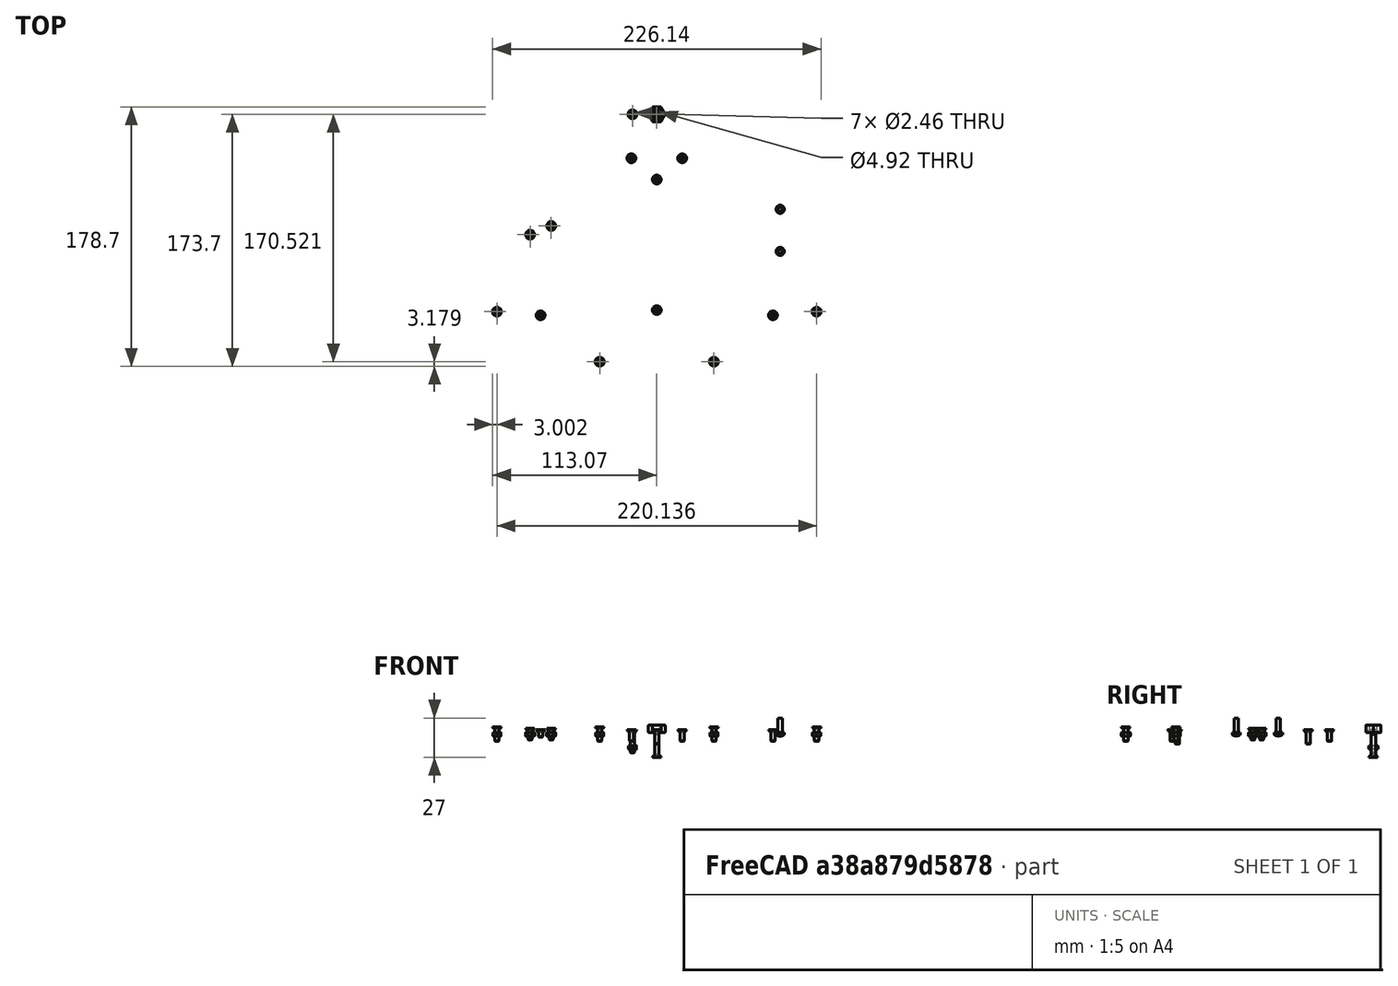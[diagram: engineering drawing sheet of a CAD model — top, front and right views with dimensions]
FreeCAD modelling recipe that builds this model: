
FCSTD DOCUMENT  (FreeCAD 1.0RUnknown)
Label: Sextant
License: All rights reserved
LicenseURL: https://en.wikipedia.org/wiki/All_rights_reserved
objects: Part::FeaturePython×24, App::Link×18, App::DocumentObjectGroup×10, PartDesign::CoordinateSystem×1, App::FeaturePython×1, App::Part×1
note: 25 computed .brp shape members not serialized (recipe doc carries the construction recipe); baked Part::Feature solids carry a one-line shape summary decoded from their .brp
EXTERNAL_REF file=Frame.FCStd obj=Local_CS003
EXTERNAL_REF file=Scale.FCStd obj=LCS_Origin002
EXTERNAL_REF file=Scale.FCStd obj=Part002
EXTERNAL_REF file=Frame.FCStd obj=Local_CS
EXTERNAL_REF file=HorizonMirror.FCStd obj=LCS_Origin
EXTERNAL_REF file=HorizonMirror.FCStd obj=Assembly
EXTERNAL_REF file=Frame.FCStd obj=Local_CS001
EXTERNAL_REF file=Viewscope.FCStd obj=LCS_Origin
EXTERNAL_REF file=Viewscope.FCStd obj=Assembly
EXTERNAL_REF file=Frame.FCStd obj=HoleAxis_1
EXTERNAL_REF file=Frame.FCStd obj=HoleAxis_2
EXTERNAL_REF file=HorizonMirror.FCStd obj=LCS_Screw1
EXTERNAL_REF file=HorizonMirror.FCStd obj=LCS_Screw2
EXTERNAL_REF file=Frame.FCStd obj=Local_CS002
EXTERNAL_REF file=Parts.FCStd obj=LCS_Top
EXTERNAL_REF file=Parts.FCStd obj=bEARING
EXTERNAL_REF file=Resources.FCStd obj=Spreadsheet
EXTERNAL_REF file=Scale.FCStd obj=LCS_Screw1
EXTERNAL_REF file=Scale.FCStd obj=LCS_Screw3
EXTERNAL_REF file=Frame.FCStd obj=LCS_Origin
EXTERNAL_REF file=Frame.FCStd obj=Body
EXTERNAL_REF file=IndexArm.FCStd obj=LCS_1
EXTERNAL_REF file=IndexArm.FCStd obj=Assembly
EXTERNAL_REF file=Parts.FCStd obj=LCS_Origin001
EXTERNAL_REF file=Parts.FCStd obj=BearingCover
EXTERNAL_REF file=Frame.FCStd obj=Local_CS004
EXTERNAL_REF file=Parts.FCStd obj=LCS_Bottom
EXTERNAL_REF file=Parts.FCStd obj=LCS_ClampTop
EXTERNAL_REF file=Parts.FCStd obj=BearingClamp
EXTERNAL_REF file=Parts.FCStd obj=LCS_Origin002
EXTERNAL_REF file=Frame.FCStd obj=LCS_Handle
EXTERNAL_REF file=Handle.FCStd obj=Local_CS
EXTERNAL_REF file=Handle.FCStd obj=Body002
EXTERNAL_REF file=Shadeset.FCStd obj=DatumPlane004
EXTERNAL_REF file=Shadeset.FCStd obj=LCS_Origin
EXTERNAL_REF file=Shadeset.FCStd obj=Assembly
EXTERNAL_REF file=Frame.FCStd obj=Local_CS005
EXTERNAL_REF file=Shadeset.FCStd obj=Local_CS004
EXTERNAL_REF file=Shadeset.FCStd obj=Body001
EXTERNAL_REF file=Shadeset.FCStd obj=DatumPlane003
EXTERNAL_REF file=Frame.FCStd obj=Local_CS006
EXTERNAL_REF file=Shadeset.FCStd obj=Local_CS005
EXTERNAL_REF file=Shadeset.FCStd obj=OffsetBlockHorizonShade
EXTERNAL_REF file=Frame.FCStd obj=DatumLine
EXTERNAL_REF file=Parts.FCStd obj=LCS_Bottom001
EXTERNAL_REF file=Parts.FCStd obj=Standoff
EXTERNAL_REF file=Frame.FCStd obj=DatumLine003
EXTERNAL_REF file=Frame.FCStd obj=DatumLine001
EXTERNAL_REF file=Frame.FCStd obj=DatumLine002
EXTERNAL_REF file=Parts.FCStd obj=LCS_Origin003
EXTERNAL_REF file=Frame.FCStd obj=DatumLine004
EXTERNAL_REF file=Frame.FCStd obj=DatumLine005
EXTERNAL_REF file=Scale.FCStd obj=LCS_Screw004
EXTERNAL_REF file=Scale.FCStd obj=LCS_Screw2

FEATURE [App::DocumentObjectGroup] Parts
FEATURE [PartDesign::CoordinateSystem] LCS_Origin
  AttacherType = Attacher::AttachEngine3D
  AttachmentSupport = -> [X_Axis]
  MapMode = 2
FEATURE [App::DocumentObjectGroup] Constraints
FEATURE [App::FeaturePython] Variables  # WARN: FeaturePython — macro-defined, semantics opaque (R4)
  Type = App::PropertyContainer
  angle = 60
FEATURE [App::DocumentObjectGroup] Configurations
FEATURE [App::Link] Scale
  AttachedBy = #LCS_Origin002
  AttachedTo = Frame#Local_CS003
  LinkPlacement = pos=(0,0,2) rot=(0,0,1;0rad)
  LinkedObject = -> <external Scale.FCStd>#Part002
  Placement = pos=(0,0,2) rot=(0,0,1;0rad)
  SolverId = Asm4EE
  expr: Placement = Frame.Placement * Frame#Local_CS003.Placement * AttachmentOffset * Scale#LCS_Origin002.Placement ^ -1
FEATURE [App::Link] HorizonMirror
  AttachedBy = #LCS_Origin
  AttachedTo = Frame#Local_CS
  AttachmentOffset = pos=(0,0,0) rot=(0,0,1;4.71239rad)
  LinkPlacement = pos=(-80,-80,2) rot=(0,0,-1;5.89049rad)
  LinkedObject = -> <external HorizonMirror.FCStd>#Assembly
  Placement = pos=(-80,-80,2) rot=(0,0,-1;5.89049rad)
  SolverId = Asm4EE
  expr: Placement = Frame.Placement * Frame#Local_CS.Placement * AttachmentOffset * HorizonMirror#LCS_Origin.Placement ^ -1
FEATURE [App::Link] Viewscope
  AttachedBy = #LCS_Origin
  AttachedTo = Frame#Local_CS001
  LinkPlacement = pos=(85,-80,2) rot=(0,0,1;0rad)
  LinkedObject = -> <external Viewscope.FCStd>#Assembly
  Placement = pos=(85,-80,2) rot=(0,0,1;0rad)
  SolverId = Asm4EE
  expr: Placement = Frame.Placement * Frame#Local_CS001.Placement * AttachmentOffset * Viewscope#LCS_Origin.Placement ^ -1
FEATURE [Part::FeaturePython] Screw  label="M3x10-Screw"  # WARN: FeaturePython — macro-defined, semantics opaque (R4)
  AttachedBy = Origin
  AttachedTo = Frame#HoleAxis_1
  Diameter = 3
  Invert = false
  LeftHanded = false
  Length = 1
  LengthCustom = 10
  MatchOuter = false
  OffsetAngle = 0
  Placement = pos=(0,-45,2) rot=(0,0,1;0rad)
  SolverId = Asm4EE
  Thread = false
  Type = 50
  expr: Placement = Frame.Placement * Frame#HoleAxis_1.Placement * AttachmentOffset
FEATURE [Part::FeaturePython] Screw001  label="M3x10-Screw080"  # WARN: FeaturePython — macro-defined, semantics opaque (R4)
  AttachedBy = Origin
  AttachedTo = Frame#HoleAxis_2
  Diameter = 3
  Invert = false
  LeftHanded = false
  Length = 1
  LengthCustom = 10
  MatchOuter = false
  OffsetAngle = 0
  Placement = pos=(0,-135,2) rot=(0,0,1;0rad)
  SolverId = Asm4EE
  Thread = false
  Type = 50
  expr: Placement = Frame.Placement * Frame#HoleAxis_2.Placement * AttachmentOffset
FEATURE [Part::FeaturePython] Screw002  label="M3x8-Screw"  # WARN: FeaturePython — macro-defined, semantics opaque (R4)
  AttachedBy = Origin
  AttachedTo = HorizonMirror#LCS_Screw1
  Diameter = 3
  Invert = false
  LeftHanded = false
  Length = 0
  LengthCustom = 8
  MatchOuter = false
  OffsetAngle = 0
  Placement = pos=(-87.2617,-83.0079,3) rot=(0,0,-1;4.31969rad)
  SolverId = Asm4EE
  Thread = false
  Type = 50
  expr: Placement = HorizonMirror.Placement * HorizonMirror#LCS_Screw1.Placement * AttachmentOffset
FEATURE [Part::FeaturePython] Screw003  label="M3x8-Screw388"  # WARN: FeaturePython — macro-defined, semantics opaque (R4)
  AttachedBy = Origin
  AttachedTo = HorizonMirror#LCS_Screw2
  Diameter = 3
  Invert = false
  LeftHanded = false
  Length = 0
  LengthCustom = 8
  MatchOuter = false
  OffsetAngle = 0
  Placement = pos=(-72.7383,-76.9921,3) rot=(0,0,-1;4.31969rad)
  SolverId = Asm4EE
  Thread = false
  Type = 50
  expr: Placement = HorizonMirror.Placement * HorizonMirror#LCS_Screw2.Placement * AttachmentOffset
FEATURE [Part::FeaturePython] Nut001  label="M3-Nut658"  # WARN: FeaturePython — macro-defined, semantics opaque (R4)
  AttachedBy = Origin
  AttachedTo = HorizonMirror#LCS_Screw2
  AttachmentOffset = pos=(0,0,-3) rot=(1,0,0;3.14159rad)
  Diameter = 4
  Invert = false
  LeftHanded = false
  MatchOuter = false
  OffsetAngle = 0
  Placement = pos=(-72.7383,-76.9921,0) rot=(-0.55557,-0.83147,0;3.14159rad)
  SolverId = Asm4EE
  Thread = false
  Type = 31
  expr: .AttachmentOffset.Base.z = -<<Dimensions>>.horizon_mirror_base_thickness - <<Dimensions>>.frame_thickness
  expr: Placement = HorizonMirror.Placement * HorizonMirror#LCS_Screw2.Placement * AttachmentOffset
FEATURE [Part::FeaturePython] Nut002  label="M3-Nut657"  # WARN: FeaturePython — macro-defined, semantics opaque (R4)
  AttachedBy = Origin
  AttachedTo = HorizonMirror#LCS_Screw1
  AttachmentOffset = pos=(0,0,-3) rot=(0,-1,0;3.14159rad)
  Diameter = 4
  Invert = false
  LeftHanded = false
  MatchOuter = false
  OffsetAngle = 0
  Placement = pos=(-87.2617,-83.0079,0) rot=(-0.83147,0.55557,0;3.14159rad)
  SolverId = Asm4EE
  Thread = false
  Type = 31
  expr: .AttachmentOffset.Base.z = -<<Dimensions>>.horizon_mirror_base_thickness - <<Dimensions>>.frame_thickness
  expr: Placement = HorizonMirror.Placement * HorizonMirror#LCS_Screw1.Placement * AttachmentOffset
FEATURE [App::Link] Bearing001
  AttachedBy = #LCS_Top
  AttachedTo = Frame#Local_CS002
  LinkPlacement = pos=(0,0,-3.5) rot=(0,0,1;0rad)
  LinkedObject = -> <external Parts.FCStd>#bEARING
  Placement = pos=(0,0,-3.5) rot=(0,0,1;0rad)
  SolverId = Asm4EE
  expr: Placement = Frame.Placement * Frame#Local_CS002.Placement * AttachmentOffset * Parts#LCS_Top.Placement ^ -1
FEATURE [App::Link] Link  label="Dimensions"
  LinkedObject = -> <external Resources.FCStd>#Spreadsheet
FEATURE [Part::FeaturePython] Screw004  label="M3x10-Screw078"  # WARN: FeaturePython — macro-defined, semantics opaque (R4)
  AttachedBy = Origin
  AttachedTo = Scale#LCS_Screw1
  Diameter = 3
  Invert = false
  LeftHanded = false
  Length = 1
  LengthCustom = 10
  MatchOuter = false
  OffsetAngle = 0
  Placement = pos=(-110.068,-136.052,4) rot=(0,0,1;1.5708rad)
  SolverId = Asm4EE
  Thread = false
  Type = 50
  expr: Placement = Scale.Placement * Scale#LCS_Screw1.Placement * AttachmentOffset
FEATURE [Part::FeaturePython] Screw005  label="M3x10-Screw079"  # WARN: FeaturePython — macro-defined, semantics opaque (R4)
  AttachedBy = Origin
  AttachedTo = Scale#LCS_Screw3
  Diameter = 3
  Invert = false
  LeftHanded = false
  Length = 1
  LengthCustom = 10
  MatchOuter = false
  OffsetAngle = 0
  Placement = pos=(-39.34,-170.521,4) rot=(0,0,1;1.5708rad)
  SolverId = Asm4EE
  Thread = false
  Type = 50
  expr: Placement = Scale.Placement * Scale#LCS_Screw3.Placement * AttachmentOffset
FEATURE [Part::FeaturePython] Nut  label="M3-Nut"  # WARN: FeaturePython — macro-defined, semantics opaque (R4)
  AttachedBy = Origin
  AttachedTo = Scale#LCS_Screw1
  AttachmentOffset = pos=(0,0,-4) rot=(0,1,0;3.14159rad)
  Diameter = 4
  Invert = false
  LeftHanded = false
  MatchOuter = false
  OffsetAngle = 0
  Placement = pos=(-110.068,-136.052,0) rot=(-0.707107,0.707107,0;3.14159rad)
  SolverId = Asm4EE
  Thread = false
  Type = 31
  expr: .AttachmentOffset.Base.z = -<<Dimensions>>.scale_thickness - <<Dimensions>>.frame_thickness
  expr: Placement = Scale.Placement * Scale#LCS_Screw1.Placement * AttachmentOffset
FEATURE [Part::FeaturePython] Nut003  label="M3-Nut656"  # WARN: FeaturePython — macro-defined, semantics opaque (R4)
  AttachedBy = Origin
  AttachedTo = Scale#LCS_Screw3
  AttachmentOffset = pos=(0,0,-4) rot=(0,1,0;3.14159rad)
  Diameter = 4
  Invert = false
  LeftHanded = false
  MatchOuter = false
  OffsetAngle = 0
  Placement = pos=(-39.34,-170.521,0) rot=(-0.707107,0.707107,0;3.14159rad)
  SolverId = Asm4EE
  Thread = false
  Type = 31
  expr: .AttachmentOffset.Base.z = -<<Dimensions>>.scale_thickness - <<Dimensions>>.frame_thickness
  expr: Placement = Scale.Placement * Scale#LCS_Screw3.Placement * AttachmentOffset
FEATURE [App::Link] Frame
  AttachedBy = #LCS_Origin
  AttachedTo = Parent Assembly#LCS_Origin
  LinkedObject = -> <external Frame.FCStd>#Body
  SolverId = Asm4EE
  expr: Placement = LCS_Origin.Placement * AttachmentOffset * Frame#LCS_Origin.Placement ^ -1
FEATURE [App::Link] IndexArm
  AttachedBy = #LCS_1
  AttachedTo = Frame#LCS_Origin
  AttachmentOffset = pos=(0,0,0) rot=(0,0,1;-1.0472rad)
  LinkPlacement = pos=(0,0,4) rot=(0,0,1;5.75959rad)
  LinkedObject = -> <external IndexArm.FCStd>#Assembly
  Placement = pos=(0,0,4) rot=(0,0,1;5.75959rad)
  SolverId = Asm4EE
  expr: .AttachmentOffset.Rotation.Angle = -Variables.angle
  expr: Placement = Frame.Placement * Frame#LCS_Origin.Placement * AttachmentOffset * IndexArm#LCS_1.Placement ^ -1
FEATURE [App::Link] BearingCover
  AttachedBy = #LCS_Origin001
  AttachedTo = Frame#Local_CS002
  LinkedObject = -> <external Parts.FCStd>#BearingCover
  SolverId = Asm4EE
  expr: Placement = Frame.Placement * Frame#Local_CS002.Placement * AttachmentOffset * Parts#LCS_Origin001.Placement ^ -1
FEATURE [Part::FeaturePython] Screw008  label="M3x16-Screw"  # WARN: FeaturePython — macro-defined, semantics opaque (R4)
  AttachedBy = Origin
  AttachedTo = Frame#Local_CS004
  Diameter = 3
  Invert = false
  LeftHanded = false
  Length = 3
  LengthCustom = 16
  MatchOuter = false
  OffsetAngle = 0
  Placement = pos=(-16.75,0,2) rot=(0,0,1;1.5708rad)
  SolverId = Asm4EE
  Thread = false
  Type = 50
  expr: Placement = Frame.Placement * Frame#Local_CS004.Placement * AttachmentOffset
FEATURE [Part::FeaturePython] Nut006  label="M3-Nut655"  # WARN: FeaturePython — macro-defined, semantics opaque (R4)
  AttachedBy = Origin
  AttachedTo = Frame#Local_CS004
  AttachmentOffset = pos=(0,0,-11) rot=(0,1,0;3.14159rad)
  Diameter = 4
  Invert = false
  LeftHanded = false
  MatchOuter = false
  OffsetAngle = 0
  Placement = pos=(-16.75,0,-9) rot=(-0.707107,0.707107,0;3.14159rad)
  SolverId = Asm4EE
  Thread = false
  Type = 31
  expr: Placement = Frame.Placement * Frame#Local_CS004.Placement * AttachmentOffset
FEATURE [App::Link] BearingClamp
  AttachedBy = #LCS_ClampTop
  AttachedTo = Bearing001#LCS_Bottom
  LinkPlacement = pos=(0,0,-17) rot=(0,0,1;0rad)
  LinkedObject = -> <external Parts.FCStd>#BearingClamp
  Placement = pos=(0,0,-17) rot=(0,0,1;0rad)
  SolverId = Asm4EE
  expr: Placement = Bearing001.Placement * Parts#LCS_Bottom.Placement * AttachmentOffset * Parts#LCS_ClampTop.Placement ^ -1
FEATURE [Part::FeaturePython] Screw009  label="M3x16-Screw001"  # WARN: FeaturePython — macro-defined, semantics opaque (R4)
  AttachedBy = Origin
  AttachedTo = BearingClamp#LCS_Origin002
  AttachmentOffset = pos=(0,0,0) rot=(0,1,0;3.14159rad)
  Diameter = 3
  Invert = false
  LeftHanded = false
  Length = 3
  LengthCustom = 16
  MatchOuter = false
  OffsetAngle = 0
  Placement = pos=(0,0,-17) rot=(0,1,0;3.14159rad)
  SolverId = Asm4EE
  Thread = false
  Type = 50
  expr: Placement = BearingClamp.Placement * Parts#LCS_Origin002.Placement * AttachmentOffset
FEATURE [App::Link] Handle
  AttachedBy = #Local_CS
  AttachedTo = Frame#LCS_Handle
  AttachmentOffset = pos=(0,0,0) rot=(1,0,0;4.71239rad)
  LinkPlacement = pos=(7.1e-15,-90,-2e-16) rot=(1,0,0;4.71239rad)
  LinkedObject = -> <external Handle.FCStd>#Body002
  Placement = pos=(7.1e-15,-90,-2e-16) rot=(1,0,0;4.71239rad)
  SolverId = Asm4EE
  expr: Placement = Frame.Placement * Frame#LCS_Handle.Placement * AttachmentOffset * Handle#Local_CS.Placement ^ -1
FEATURE [App::Link] Shadeset
  AttachedBy = #LCS_Origin
  AttachedTo = OffsetBlockHorizonShade#DatumPlane004
  AttachmentOffset = pos=(0,0,0) rot=(0,0,-1;3.14159rad)
  LinkPlacement = pos=(-105,-101.182,12) rot=(0,0,1;0rad)
  LinkedObject = -> <external Shadeset.FCStd>#Assembly
  Placement = pos=(-105,-101.182,12) rot=(0,0,1;0rad)
  SolverId = Asm4EE
  expr: Placement = OffsetBlockHorizonShade.Placement * Shadeset#DatumPlane004.Placement * AttachmentOffset * Shadeset#LCS_Origin.Placement ^ -1
FEATURE [App::Link] OffsetBlockIndexShade
  AttachedBy = #Local_CS004
  AttachedTo = Frame#Local_CS005
  LinkPlacement = pos=(-64.4754,-34.5196,2) rot=(0,0,1;0.785398rad)
  LinkedObject = -> <external Shadeset.FCStd>#Body001
  Placement = pos=(-64.4754,-34.5196,2) rot=(0,0,1;0.785398rad)
  SolverId = Asm4EE
  expr: Placement = Frame.Placement * Frame#Local_CS005.Placement * AttachmentOffset * Shadeset#Local_CS004.Placement ^ -1
FEATURE [App::Link] Shadeset001
  AttachedBy = #LCS_Origin
  AttachedTo = OffsetBlockIndexShade#DatumPlane003
  AttachmentOffset = pos=(0,0,0) rot=(0,0,1;3.14159rad)
  LinkPlacement = pos=(-64.4754,-34.5196,3) rot=(0,0,1;3.92699rad)
  LinkedObject = -> <external Shadeset.FCStd>#Assembly
  Placement = pos=(-64.4754,-34.5196,3) rot=(0,0,1;3.92699rad)
  SolverId = Asm4EE
  expr: Placement = OffsetBlockIndexShade.Placement * Shadeset#DatumPlane003.Placement * AttachmentOffset * Shadeset#LCS_Origin.Placement ^ -1
FEATURE [App::Link] OffsetBlockHorizonShade
  AttachedBy = #Local_CS005
  AttachedTo = Frame#Local_CS006
  AttachmentOffset = pos=(0,0,0) rot=(0,0,-1;3.14159rad)
  LinkPlacement = pos=(-105,-101.182,2) rot=(0,0,-1;3.14159rad)
  LinkedObject = -> <external Shadeset.FCStd>#OffsetBlockHorizonShade
  Placement = pos=(-105,-101.182,2) rot=(0,0,-1;3.14159rad)
  SolverId = Asm4EE
  expr: Placement = Frame.Placement * Frame#Local_CS006.Placement * AttachmentOffset * Shadeset#Local_CS005.Placement ^ -1
FEATURE [Part::FeaturePython] Screw010  label="M3x5-Screw"  # WARN: FeaturePython — macro-defined, semantics opaque (R4)
  AttachedBy = Origin
  AttachedTo = Frame#DatumLine
  Diameter = 3
  Invert = false
  LeftHanded = false
  Length = 7
  LengthCustom = 5
  MatchOuter = false
  OffsetAngle = 0
  Placement = pos=(-80,-138.564,2) rot=(0,0,1;0rad)
  SolverId = Asm4EE
  Thread = false
  Type = 50
  expr: Placement = Frame.Placement * Frame#DatumLine.Placement * AttachmentOffset
FEATURE [App::Link] Standoff
  AttachedBy = #LCS_Bottom001
  AttachedTo = Frame#DatumLine
  AttachmentOffset = pos=(0,0,-2) rot=(0,1,0;3.14159rad)
  LinkPlacement = pos=(-80,-138.564,0) rot=(0,1,0;3.14159rad)
  LinkedObject = -> <external Parts.FCStd>#Standoff
  Placement = pos=(-80,-138.564,0) rot=(0,1,0;3.14159rad)
  SolverId = Asm4EE
  expr: .AttachmentOffset.Base.z = -<<Dimensions>>.frame_thickness
  expr: Placement = Frame.Placement * Frame#DatumLine.Placement * AttachmentOffset * Parts#LCS_Bottom001.Placement ^ -1
FEATURE [Part::FeaturePython] Screw011  label="M3x8-Screw389"  # WARN: FeaturePython — macro-defined, semantics opaque (R4)
  AttachedBy = Origin
  AttachedTo = Frame#DatumLine003
  Diameter = 3
  Invert = false
  LeftHanded = false
  Length = 0
  LengthCustom = 8
  MatchOuter = false
  OffsetAngle = 0
  Placement = pos=(80,-138.564,2) rot=(0,0,1;0rad)
  SolverId = Asm4EE
  Thread = false
  Type = 50
  expr: Placement = Frame.Placement * Frame#DatumLine003.Placement * AttachmentOffset
FEATURE [Part::FeaturePython] Screw012  label="M3x8-Screw391"  # WARN: FeaturePython — macro-defined, semantics opaque (R4)
  AttachedBy = Origin
  AttachedTo = Frame#DatumLine001
  Diameter = 3
  Invert = false
  LeftHanded = false
  Length = 0
  LengthCustom = 8
  MatchOuter = false
  OffsetAngle = 0
  Placement = pos=(17.5,-30.3109,2) rot=(0,0,1;0rad)
  SolverId = Asm4EE
  Thread = false
  Type = 50
  expr: Placement = Frame.Placement * Frame#DatumLine001.Placement * AttachmentOffset
FEATURE [Part::FeaturePython] Screw013  label="M3x8-Screw390"  # WARN: FeaturePython — macro-defined, semantics opaque (R4)
  AttachedBy = Origin
  AttachedTo = Frame#DatumLine002
  Diameter = 3
  Invert = false
  LeftHanded = false
  Length = 0
  LengthCustom = 8
  MatchOuter = false
  OffsetAngle = 0
  Placement = pos=(-17.5,-30.3109,2) rot=(0,0,1;0rad)
  SolverId = Asm4EE
  Thread = false
  Type = 50
  expr: Placement = Frame.Placement * Frame#DatumLine002.Placement * AttachmentOffset
FEATURE [App::Link] Standoff001
  AttachedBy = #LCS_Origin003
  AttachedTo = Frame#DatumLine003
  AttachmentOffset = pos=(0,0,-2) rot=(0,1,0;3.14159rad)
  LinkPlacement = pos=(80,-138.564,0) rot=(0,1,0;3.14159rad)
  LinkedObject = -> <external Parts.FCStd>#Standoff
  Placement = pos=(80,-138.564,0) rot=(0,1,0;3.14159rad)
  SolverId = Asm4EE
  expr: .AttachmentOffset.Base.z = -<<Dimensions>>.frame_thickness
  expr: Placement = Frame.Placement * Frame#DatumLine003.Placement * AttachmentOffset * Parts#LCS_Origin003.Placement ^ -1
FEATURE [App::Link] Standoff_1  label="Standoff002"
  AttachedBy = #LCS_Bottom001
  AttachedTo = Frame#DatumLine001
  AttachmentOffset = pos=(0,0,-2) rot=(0,1,0;3.14159rad)
  LinkPlacement = pos=(17.5,-30.3109,0) rot=(0,1,0;3.14159rad)
  LinkedObject = -> <external Parts.FCStd>#Standoff
  Placement = pos=(17.5,-30.3109,0) rot=(0,1,0;3.14159rad)
  SolverId = Asm4EE
  expr: .AttachmentOffset.Base.z = -<<Dimensions>>.frame_thickness
  expr: Placement = Frame.Placement * Frame#DatumLine001.Placement * AttachmentOffset * Parts#LCS_Bottom001.Placement ^ -1
FEATURE [App::Link] Standoff_2  label="Standoff003"
  AttachedBy = #LCS_Bottom001
  AttachedTo = Frame#DatumLine002
  AttachmentOffset = pos=(0,0,-2) rot=(0,1,0;3.14159rad)
  LinkPlacement = pos=(-17.5,-30.3109,0) rot=(0,1,0;3.14159rad)
  LinkedObject = -> <external Parts.FCStd>#Standoff
  Placement = pos=(-17.5,-30.3109,0) rot=(0,1,0;3.14159rad)
  SolverId = Asm4EE
  expr: .AttachmentOffset.Base.z = -<<Dimensions>>.frame_thickness
  expr: Placement = Frame.Placement * Frame#DatumLine002.Placement * AttachmentOffset * Parts#LCS_Bottom001.Placement ^ -1
FEATURE [App::DocumentObjectGroup] IndexArm001
  Group = -> [IndexArm,BearingClamp,BearingCover,Bearing001,Screw009,Screw008,Nut006]
FEATURE [App::DocumentObjectGroup] Shades
  Group = -> [OffsetBlockIndexShade,OffsetBlockHorizonShade,Shadeset,Shadeset001]
FEATURE [App::DocumentObjectGroup] HorizonMirror001
  Group = -> [HorizonMirror,Screw003,Nut001,Screw002,Nut002]
FEATURE [App::DocumentObjectGroup] Standoff002  label="Standoffs"
  Group = -> [Standoff001,Standoff_1,Standoff_2,Standoff,Screw011,Screw013,Screw012,Screw010]
FEATURE [Part::FeaturePython] Screw014  label="M3x10-Screw081"  # WARN: FeaturePython — macro-defined, semantics opaque (R4)
  AttachedBy = Origin
  AttachedTo = Frame#DatumLine004
  AttachmentOffset = pos=(0,0,0) rot=(0,1,0;3.14159rad)
  Diameter = 4
  Invert = false
  LeftHanded = false
  Length = 4
  LengthCustom = 10
  MatchOuter = false
  OffsetAngle = 0
  Placement = pos=(85,-65.5,0) rot=(0,1,0;3.14159rad)
  SolverId = Asm4EE
  Thread = false
  Type = 76
  expr: Diameter = <<Dimensions>>.viewscope_screw_type
  expr: Placement = Frame.Placement * Frame#DatumLine004.Placement * AttachmentOffset
FEATURE [Part::FeaturePython] Screw015  label="M3x10-Screw082"  # WARN: FeaturePython — macro-defined, semantics opaque (R4)
  AttachedBy = Origin
  AttachedTo = Frame#DatumLine005
  AttachmentOffset = pos=(0,0,0) rot=(0,1,0;3.14159rad)
  Diameter = 4
  Invert = false
  LeftHanded = false
  Length = 4
  LengthCustom = 10
  MatchOuter = false
  OffsetAngle = 0
  Placement = pos=(85,-94.5,0) rot=(0,1,0;3.14159rad)
  SolverId = Asm4EE
  Thread = false
  Type = 76
  expr: Diameter = <<Dimensions>>.viewscope_screw_type
  expr: Placement = Frame.Placement * Frame#DatumLine005.Placement * AttachmentOffset
FEATURE [App::DocumentObjectGroup] ViewScope
  Group = -> [Viewscope,Screw014,Screw015]
FEATURE [Part::FeaturePython] Screw016  label="M3x10-Screw083"  # WARN: FeaturePython — macro-defined, semantics opaque (R4)
  AttachedBy = Origin
  AttachedTo = Scale#LCS_Screw004
  Diameter = 3
  Invert = false
  LeftHanded = false
  Length = 1
  LengthCustom = 10
  MatchOuter = false
  OffsetAngle = 0
  Placement = pos=(39.34,-170.521,4) rot=(0,0,1;1.5708rad)
  SolverId = Asm4EE
  Thread = false
  Type = 50
  expr: Placement = Scale.Placement * Scale#LCS_Screw004.Placement * AttachmentOffset
FEATURE [Part::FeaturePython] Screw017  label="M3x10-Screw084"  # WARN: FeaturePython — macro-defined, semantics opaque (R4)
  AttachedBy = Origin
  AttachedTo = Scale#LCS_Screw2
  Diameter = 3
  Invert = false
  LeftHanded = false
  Length = 1
  LengthCustom = 10
  MatchOuter = false
  OffsetAngle = 0
  Placement = pos=(110.068,-136.052,4) rot=(0,0,1;1.5708rad)
  SolverId = Asm4EE
  Thread = false
  Type = 50
  expr: Placement = Scale.Placement * Scale#LCS_Screw2.Placement * AttachmentOffset
FEATURE [Part::FeaturePython] Nut007  label="M3-Nut659"  # WARN: FeaturePython — macro-defined, semantics opaque (R4)
  AttachedBy = Origin
  AttachedTo = Scale#LCS_Screw004
  AttachmentOffset = pos=(0,0,-4) rot=(0,1,0;3.14159rad)
  Diameter = 4
  Invert = false
  LeftHanded = false
  MatchOuter = false
  OffsetAngle = 0
  Placement = pos=(39.34,-170.521,0) rot=(-0.707107,0.707107,0;3.14159rad)
  SolverId = Asm4EE
  Thread = false
  Type = 31
  expr: .AttachmentOffset.Base.z = -<<Dimensions>>.scale_thickness - <<Dimensions>>.frame_thickness
  expr: Placement = Scale.Placement * Scale#LCS_Screw004.Placement * AttachmentOffset
FEATURE [Part::FeaturePython] Nut008  label="M6-Nut"  # WARN: FeaturePython — macro-defined, semantics opaque (R4)
  Diameter = 8
  Invert = false
  LeftHanded = false
  MatchOuter = false
  OffsetAngle = 0
  Thread = false
  Type = 31
FEATURE [App::DocumentObjectGroup] Handle001
  Group = -> [Handle,Screw,Screw001,Nut008]
FEATURE [Part::FeaturePython] Nut009  label="M3-Nut660"  # WARN: FeaturePython — macro-defined, semantics opaque (R4)
  AttachedBy = Origin
  AttachedTo = Scale#LCS_Screw2
  AttachmentOffset = pos=(0,0,-4) rot=(0,1,0;3.14159rad)
  Diameter = 4
  Invert = false
  LeftHanded = false
  MatchOuter = false
  OffsetAngle = 0
  Placement = pos=(110.068,-136.052,0) rot=(-0.707107,0.707107,0;3.14159rad)
  SolverId = Asm4EE
  Thread = false
  Type = 31
  expr: .AttachmentOffset.Base.z = -<<Dimensions>>.scale_thickness - <<Dimensions>>.frame_thickness
  expr: Placement = Scale.Placement * Scale#LCS_Screw2.Placement * AttachmentOffset
FEATURE [App::DocumentObjectGroup] Scale001
  Group = -> [Scale,Nut,Nut003,Screw004,Screw005,Screw016,Screw017,Nut007,Nut009]
FEATURE [App::Part] Assembly
  AssemblyType = Part::Link
  Group = -> [LCS_Origin,Constraints,Variables,Configurations,Frame,Screw008,Nut006,Screw004,Screw005,Nut,Nut003,Screw,Screw001,Screw002,Nut002,Screw009,ViewScope,Screw003,Standoff,Screw010,Nut001,Screw011,Screw013,Screw012,Standoff001,Standoff_1,Standoff_2,IndexArm001,IndexArm,Viewscope,Shades,BearingClamp,BearingCover,Bearing001,OffsetBlockIndexShade,OffsetBlockHorizonShade,Shadeset,Shadeset001,Handle001,+13 more]
  Origin = -> Origin
  Type = Assembly

RESOLVED EXTERNAL PARTS (link-assembly join: the EXTERNAL_REF files above that resolve inside this repo's crawl, each included once):
---- part Frame.FCStd = doc fcstd_3e981a858956 ----
FCSTD DOCUMENT  (FreeCAD 1.0RUnknown)
Label: Frame
License: All rights reserved
LicenseURL: http://en.wikipedia.org/wiki/All_rights_reserved
objects: Sketcher::SketchObject×16, PartDesign::CoordinateSystem×9, PartDesign::Line×8, PartDesign::Pad×8, PartDesign::Hole×8, PartDesign::Plane×2, App::Link×1, PartDesign::SubShapeBinder×1, TechDraw::DrawSVGTemplate×1, PartDesign::Mirrored×1, PartDesign::Pocket×1, PartDesign::PolarPattern×1, PartDesign::Draft×1, PartDesign::Body×1, TechDraw::DrawViewPart×1, TechDraw::DrawPage×1
note: 111 computed .brp shape members not serialized (recipe doc carries the construction recipe); baked Part::Feature solids carry a one-line shape summary decoded from their .brp
EXTERNAL_REF file=Resources.FCStd obj=Spreadsheet
EXTERNAL_REF file=Scale.FCStd obj=Part002
EXTERNAL_REF file=HorizonMirror.FCStd obj=Sketch
EXTERNAL_REF file=Viewscope.FCStd obj=Sketch004
EXTERNAL_REF file=Shade.FCStd obj=Sketch010

FEATURE [App::Link] Link  label="Dimensions"
  LinkedObject = -> <external Resources.FCStd>#Spreadsheet
FEATURE [Sketcher::SketchObject] Sketch006
  ArcFitTolerance = 0
  AttachmentOffset = pos=(0,0,2) rot=(0,0,1;0rad)
  AttachmentSupport = -> [XY_Plane]
  FullyConstrained = true
  MakeInternals = false
  MapMode = 5
  Placement = pos=(0,0,2) rot=(0,0,1;0rad)
  expr: .AttachmentOffset.Base.z = <<Dimensions>>.frame_thickness
  expr: Constraints[3] = <<Dimensions>>.handle_connector_screw_diameter
  expr: Constraints[4] = <<Dimensions>>.handle_length - <<Dimensions>>.handle_outer_width
  expr: Constraints[6] = <<Dimensions>>.scale_outer_radius / 2
  sketch-geometry (3):
    g0: Circle CenterX=0 CenterY=-45 CenterZ=0 NormalX=0 NormalY=0 NormalZ=1 AngleXU=0 Radius=1.5
    g1: Circle CenterX=0 CenterY=-135 CenterZ=0 NormalX=0 NormalY=0 NormalZ=1 AngleXU=0 Radius=1.5
    g2: GeomPoint [constr] X=0 Y=-90 Z=0
  constraints (7):
    c: PointOnObject(g0,g-2)
    c: PointOnObject(g1,g-2)
    c: Equal(g1,g0)
    c: Diameter(g0) = 3
    c: Distance(g0,g1) = 90
    c: Symmetric(g0,g1,g2)
    c: DistanceY(g2,g-1) = 90
FEATURE [PartDesign::SubShapeBinder] Binder
  BindCopyOnChange = 0
  BindMode = 0
  ClaimChildren = false
  Context = -> Body [Hole.Binder.]
  Fuse = false
  MakeFace = true
  OffsetFill = false
  OffsetIntersection = false
  OffsetJoinType = 0
  OffsetOpenResult = false
  PartialLoad = false
  Placement = pos=(0,0,-4) rot=(0,0,1;0rad)
  Relative = true
  Support = -> [<external Scale.FCStd>#Part002[Body003.Sketch.]]
  _Version = 2
FEATURE [Sketcher::SketchObject] Sketch003
  ArcFitTolerance = 0
  AttachmentSupport = -> [XY_Plane]
  FullyConstrained = true
  MakeInternals = false
  MapMode = 5
  expr: Constraints[10] = <<Dimensions>>.view_center_offset_vert
  expr: Constraints[4] = <<Dimensions>>.viewscope_screw_diameter
  expr: Constraints[5] = <<Viewscope>>#Sketch004.Constraints.hole_distance
  sketch-geometry (6):
    g0: LineSegment [constr] StartX=85 StartY=-65.5 StartZ=0 EndX=85 EndY=-94.5 EndZ=0
    g1: Circle CenterX=85 CenterY=-65.5 CenterZ=0 NormalX=0 NormalY=0 NormalZ=1 AngleXU=0 Radius=1.5
    g2: Circle CenterX=85 CenterY=-94.5 CenterZ=0 NormalX=0 NormalY=0 NormalZ=1 AngleXU=0 Radius=1.5
    g3: GeomPoint [constr] X=85 Y=-80 Z=0
    g4: LineSegment [constr] StartX=85 StartY=-80 StartZ=0 EndX=0 EndY=-80 EndZ=0
    g5: GeomPoint [constr] X=0 Y=-80 Z=0
  constraints (14):
    c: Coincident(g1,g0)
    c: Coincident(g0,g2)
    c: Vertical(g0)
    c: Equal(g2,g1)
    c: Diameter(g1) = 3
    c: Distance(g0) = 29
    c: Symmetric(g1,g2,g3)
    c: Coincident(g4,g3)
    c: PointOnObject(g4,g-2)
    c: Horizontal(g4)
    c: DistanceY(g4,g-1) = 80
    c: PointOnObject(g5,g4)
    c: DistanceX(g5,g3) = 85
    c: PointOnObject(g5,g-2)
FEATURE [Sketcher::SketchObject] Sketch004
  ArcFitTolerance = 0
  AttachmentSupport = -> [XY_Plane]
  ExternalGeometry = -> [Sketch003]
  FullyConstrained = true
  MakeInternals = false
  MapMode = 5
  expr: Constraints[7] = <<Dimensions>>.viewscope_collar_thickness / 2
  expr: Constraints[8] = <<Dimensions>>.viewscope_collar_width / 2
  expr: Constraints[9] = <<Dimensions>>.viewscope_collar_width / 2
  sketch-geometry (6):
    g0: LineSegment StartX=35.7957 StartY=-62 StartZ=0 EndX=88.75 EndY=-62 EndZ=0
    g1: LineSegment StartX=88.75 StartY=-62 StartZ=0 EndX=88.75 EndY=-98 EndZ=0
    g2: LineSegment StartX=88.75 StartY=-98 StartZ=0 EndX=56.5803 EndY=-98 EndZ=0
    g3: LineSegment StartX=35.7957 StartY=-62 StartZ=0 EndX=56.5803 EndY=-98 EndZ=0
    g4: LineSegment [constr] StartX=0 StartY=0 StartZ=0 EndX=-35.7957 EndY=-62 EndZ=0
    g5: LineSegment [constr] StartX=0 StartY=0 StartZ=0 EndX=35.7957 EndY=-62 EndZ=0
  constraints (16):
    c: Horizontal(g0)
    c: Vertical(g1)
    c: Horizontal(g2)
    c: Coincident(g3,g0)
    c: Coincident(g3,g2)
    c: Coincident(g0,g1)
    c: Coincident(g2,g1)
    c: DistanceX(g-3,g0) = 3.75
    c: DistanceY(g-3,g0) = 3.5
    c: DistanceY(g1,g-4) = 3.5
    c: Coincident(g4,g-1)
    c: Coincident(g5,g4)
    c: Coincident(g0,g5)
    c: Parallel(g5,g3)
    c: Symmetric(g4,g0,g-2)
    c: Angle(g4,g5) = 1.0472
FEATURE [Sketcher::SketchObject] Sketch007
  ArcFitTolerance = 0
  AttachmentSupport = -> [XY_Plane]
  FullyConstrained = true
  MakeInternals = false
  MapMode = 5
  expr: Constraints[1] = <<Dimensions>>.bearing_Da
  sketch-geometry (1):
    g0: Circle CenterX=0 CenterY=0 CenterZ=0 NormalX=0 NormalY=0 NormalZ=1 AngleXU=0 Radius=10
  constraints (2):
    c: Coincident(g0,g-1)
    c: Diameter(g0) = 20
FEATURE [PartDesign::CoordinateSystem] LCS_Origin
  AttacherType = Attacher::AttachEngine3D
  AttachmentSupport = -> [X_Axis]
  MapMode = 2
FEATURE [PartDesign::CoordinateSystem] LCS_Handle
  AttacherType = Attacher::AttachEngine3D
  AttachmentOffset = pos=(0,0,-2) rot=(0,0,1;0rad)
  AttachmentSupport = -> [Sketch006]
  MapMode = 45
  Placement = pos=(7.1e-15,-90,-2e-16) rot=(0,0,1;0rad)
  expr: .AttachmentOffset.Base.z = -<<Dimensions>>.frame_thickness
FEATURE [PartDesign::Line] HoleAxis_1  label="HandleScrew1"
  AttacherType = Attacher::AttachEngineLine
  AttachmentSupport = -> [Sketch006]
  Length = 4.2272
  MapMode = 19
  Placement = pos=(0,-45,2) rot=(0,0,1;0rad)
  ResizeMode = 1
FEATURE [PartDesign::Line] HoleAxis_2  label="HandleScrew2"
  AttacherType = Attacher::AttachEngineLine
  AttachmentSupport = -> [Sketch006]
  Length = 4.2272
  MapMode = 19
  Placement = pos=(0,-135,2) rot=(0,0,1;0rad)
  ResizeMode = 1
FEATURE [PartDesign::CoordinateSystem] Local_CS001  label="LCS_Viewscope"
  AttacherType = Attacher::AttachEngine3D
  AttachmentOffset = pos=(0,0,2) rot=(0,0,1;0rad)
  AttachmentSupport = -> [Sketch003]
  MapMode = 45
  Placement = pos=(85,-80,2) rot=(0,0,1;0rad)
  expr: .AttachmentOffset.Base.z = <<Dimensions>>.frame_thickness
FEATURE [PartDesign::CoordinateSystem] Local_CS002  label="LCS_ShaftBot"
  AttacherType = Attacher::AttachEngine3D
  AttachmentOffset = pos=(0,0,0) rot=(0,0,-1;1.5708rad)
  AttachmentSupport = -> [Sketch007]
  MapMode = 11
FEATURE [PartDesign::CoordinateSystem] Local_CS003  label="LCS_Scale"
  AttacherType = Attacher::AttachEngine3D
  AttachmentOffset = pos=(0,0,2) rot=(0,0,1;0rad)
  AttachmentSupport = -> [X_Axis]
  MapMode = 2
  Placement = pos=(0,0,2) rot=(0,0,1;0rad)
  expr: .AttachmentOffset.Base.z = <<Dimensions>>.frame_thickness
FEATURE [TechDraw::DrawSVGTemplate] Template
  Height = 210
  Orientation = 1
  Template = /app/share/Mod/TechDraw/Templates/A4_Landscape_blank.svg
  Width = 297
FEATURE [PartDesign::Plane] DatumPlane  label="Plane_Bottom"
  AttachmentSupport = -> [XY_Plane]
  Length = 67.9716
  MapMode = 5
  ResizeMode = 0
  Width = 179.461
FEATURE [Sketcher::SketchObject] Sketch
  ArcFitTolerance = 0
  AttachmentSupport = -> [DatumPlane]
  ExternalGeometry = -> [Sketch006]
  FullyConstrained = true
  MakeInternals = false
  MapMode = 2
  expr: Constraints[11] = <<Dimensions>>.scale_width
  expr: Constraints[25] = <<Dimensions>>.frame_width
  expr: Constraints[26] = max(<<Dimensions>>.frame_width; <<Dimensions>>.handle_outer_width) / 2
  expr: Constraints[3] = <<Dimensions>>.scale_outer_radius
  expr: Constraints[4] = (<<Dimensions>>.scale_angle + 2 * <<Dimensions>>.scale_extra_angle) / 2
  expr: Constraints[5] = <<Dimensions>>.bearing_housing_diameter / 2
  sketch-geometry (11):
    g0: ArcOfCircle CenterX=0 CenterY=0 CenterZ=0 NormalX=0 NormalY=0 NormalZ=1 AngleXU=0 Radius=22.5 StartAngle=1.5708 EndAngle=3.84895
    g1: LineSegment StartX=-17.1018 StartY=-14.6212 StartZ=0 EndX=-91.4124 EndY=-143.331 EndZ=0
    g2: LineSegment StartX=-78.422 StartY=-150.831 StartZ=0 EndX=-7.5 EndY=-27.9904 EndZ=0
    g3: ArcOfCircle CenterX=0 CenterY=0 CenterZ=0 NormalX=0 NormalY=0 NormalZ=1 AngleXU=0 Radius=170 StartAngle=4.23292 EndAngle=4.66826
    g4: ArcOfCircle CenterX=0 CenterY=0 CenterZ=0 NormalX=0 NormalY=0 NormalZ=1 AngleXU=0 Radius=180 StartAngle=3.97062 EndAngle=4.71239
    g5: LineSegment StartX=-121.606 StartY=-132.71 StartZ=0 EndX=-114.85 EndY=-125.337 EndZ=0
    g6: ArcOfCircle CenterX=0 CenterY=0 CenterZ=0 NormalX=0 NormalY=0 NormalZ=1 AngleXU=0 Radius=170 StartAngle=3.97062 EndAngle=4.14466
    g7: LineSegment StartX=1.4e-15 StartY=22.5 StartZ=0 EndX=0 EndY=-180 EndZ=0
    g8: LineSegment StartX=-7.5 StartY=-27.9904 StartZ=0 EndX=-7.5 EndY=-169.834 EndZ=0
    g9: ArcOfCircle [constr] CenterX=0 CenterY=0 CenterZ=0 NormalX=0 NormalY=0 NormalZ=1 AngleXU=0 Radius=170 StartAngle=4.14466 EndAngle=4.23292
    g10: LineSegment [constr] StartX=0 StartY=0 StartZ=0 EndX=-84.9172 EndY=-147.081 EndZ=0
  constraints (32):
    c: Coincident(g3,g0)
    c: Coincident(g3,g2)
    c: Coincident(g0,g1)
    c: Radius(g4) = 180
    c: Angle(g4) = 0.741765
    c: Radius(g0) = 22.5
    c: PointOnObject(g4,g-1)
    c: Coincident(g5,g4)
    c: Coincident(g6,g5)
    c: Coincident(g6,g1)
    c: Perpendicular(g4,g5)
    c: Distance(g5) = 10
    c: Coincident(g6,g0)
    c: Parallel(g1,g2)
    c: PointOnObject(g4,g-2)
    c: Coincident(g7,g4)
    c: PointOnObject(g4,g-2)
    c: PointOnObject(g0,g-2)
    c: Coincident(g0,g4)
    c: Vertical(g8)
    c: Coincident(g2,g8)
    c: Coincident(g8,g3)
    c: Coincident(g0,g7)
    c: Coincident(g9,g1)
    c: Coincident(g9,g2)
    c: Distance(g1,g2) = 15
    c: DistanceX(g2,g0) = 7.5
    c: Coincident(g10,g0)
    c: Angle(g10,g7) = 0.523599
    c: Symmetric(g1,g2,g10)
    c: Parallel(g10,g1)
    c: Coincident(g9,g0)
FEATURE [Sketcher::SketchObject] Sketch002
  ArcFitTolerance = 0
  AttachmentSupport = -> [XY_Plane]
  ExternalGeometry = -> [Sketch]
  FullyConstrained = true
  MakeInternals = false
  MapMode = 5
  expr: Constraints[12] = <<Dimensions>>.view_center_offset_vert
  expr: Constraints[17] = HorizonMirror#Sketch.Constraints.hole_distance
  expr: Constraints[18] = <<Dimensions>>.horizon_mirror_offset
  expr: Constraints[9] = <<Dimensions>>.horizon_mirror_screw_diameter
  sketch-geometry (7):
    g0: LineSegment [constr] StartX=0 StartY=-80 StartZ=0 EndX=-80 EndY=-80 EndZ=0
    g1: LineSegment [constr] StartX=-87.2617 StartY=-83.0079 StartZ=0 EndX=-72.7383 EndY=-76.9921 EndZ=0
    g2: LineSegment [constr] StartX=-72.7383 StartY=-76.9921 StartZ=0 EndX=-72.7383 EndY=-80 EndZ=0
    g3: Circle CenterX=-87.2617 CenterY=-83.0079 CenterZ=0 NormalX=0 NormalY=0 NormalZ=1 AngleXU=0 Radius=1.5
    g4: Circle CenterX=-72.7383 CenterY=-76.9921 CenterZ=0 NormalX=0 NormalY=0 NormalZ=1 AngleXU=0 Radius=1.5
    g5: LineSegment [constr] StartX=-80 StartY=-80 StartZ=0 EndX=0 EndY=0 EndZ=0
    g6: LineSegment [constr] StartX=-72.7383 StartY=-76.9921 StartZ=0 EndX=-74.8652 EndY=-74.8652 EndZ=0
  constraints (19):
    c: PointOnObject(g0,g-2)
    c: Horizontal(g0)
    c: Symmetric(g1,g1,g0)
    c: Coincident(g2,g1)
    c: PointOnObject(g2,g0)
    c: Perpendicular(g2,g0)
    c: Coincident(g3,g1)
    c: Coincident(g4,g1)
    c: Equal(g4,g3)
    c: Diameter(g3) = 3
    c: Coincident(g5,g0)
    c: Coincident(g5,g-1)
    c: DistanceY(g0,g5) = 80
    c: Coincident(g6,g4)
    c: PointOnObject(g6,g5)
    c: Perpendicular(g6,g5)
    c: Equal(g6,g2)
    c: Distance(g1) = 15.72
    c: DistanceX(g0,g0) = 80
FEATURE [PartDesign::CoordinateSystem] Local_CS  label="LCS_HorizonMirror"
  AttacherType = Attacher::AttachEngine3D
  AttachmentOffset = pos=(0,0,2) rot=(0,0,1;0rad)
  AttachmentSupport = -> [Sketch002]
  MapMode = 45
  Placement = pos=(-80,-80,2) rot=(0,0,1;1.96349rad)
  expr: .AttachmentOffset.Base.z = <<Dimensions>>.frame_thickness
FEATURE [PartDesign::Plane] DatumPlane001  label="Plane_Top"
  AttachmentOffset = pos=(0,0,2) rot=(0,0,1;0rad)
  AttachmentSupport = -> [DatumPlane]
  Length = 67.9716
  MapMode = 5
  Placement = pos=(0,0,2) rot=(0,0,1;0rad)
  ResizeMode = 0
  Width = 179.461
  expr: .AttachmentOffset.Base.z = <<Dimensions>>.frame_thickness
FEATURE [PartDesign::Pad] Pad
  Direction = (0,0,1)
  Length = 2
  Length2 = 10
  Profile = -> Sketch
  ReferenceAxis = -> Sketch [N_Axis]
  Suppressed = false
  Type = 3
  UpToFace = -> DatumPlane001
  expr: Length = <<Dimensions>>.frame_thickness
FEATURE [Sketcher::SketchObject] Sketch008
  ArcFitTolerance = 0
  AttachmentSupport = -> [DatumPlane001]
  FullyConstrained = true
  MakeInternals = false
  MapMode = 5
  Placement = pos=(0,0,2) rot=(0,0,1;0rad)
  expr: Constraints[1] = <<Dimensions>>.bearing_D / 4 + <<Dimensions>>.bearing_housing_diameter / 4
  expr: Constraints[2] = <<Dimensions>>.bearing_housing_screw_diameter
  sketch-geometry (1):
    g0: Circle CenterX=-16.75 CenterY=0 CenterZ=0 NormalX=0 NormalY=0 NormalZ=1 AngleXU=0 Radius=1.5
  constraints (3):
    c: PointOnObject(g0,g-1)
    c: DistanceX(g0,g-1) = 16.75
    c: Diameter(g0) = 3
FEATURE [PartDesign::CoordinateSystem] Local_CS004  label="LCS_BearingHousingScrew"
  AttacherType = Attacher::AttachEngine3D
  AttachmentSupport = -> [Sketch008]
  MapMode = 11
  Placement = pos=(-16.75,0,2) rot=(0,0,1;1.5708rad)
FEATURE [Sketcher::SketchObject] Sketch009
  ArcFitTolerance = 0
  AttachmentSupport = -> [DatumPlane]
  FullyConstrained = true
  MakeInternals = false
  MapMode = 5
  expr: Constraints[23] = <<Dimensions>>.frame_width
  sketch-geometry (11):
    g0: ArcOfCircle CenterX=0 CenterY=0 CenterZ=0 NormalX=0 NormalY=0 NormalZ=1 AngleXU=0 Radius=150 StartAngle=4.18879 EndAngle=5.23599
    g1: ArcOfCircle CenterX=0 CenterY=0 CenterZ=0 NormalX=0 NormalY=0 NormalZ=1 AngleXU=0 Radius=135 StartAngle=4.18879 EndAngle=5.23599
    g2: ArcOfCircle CenterX=0 CenterY=0 CenterZ=0 NormalX=0 NormalY=0 NormalZ=1 AngleXU=0 Radius=80 StartAngle=4.18879 EndAngle=5.23599
    g3: ArcOfCircle CenterX=0 CenterY=0 CenterZ=0 NormalX=0 NormalY=0 NormalZ=1 AngleXU=0 Radius=95 StartAngle=4.18879 EndAngle=5.23599
    g4: LineSegment [constr] StartX=0 StartY=0 StartZ=0 EndX=-75 EndY=-129.904 EndZ=0
    g5: LineSegment [constr] StartX=0 StartY=0 StartZ=0 EndX=75 EndY=-129.904 EndZ=0
    g6: LineSegment StartX=-75 StartY=-129.904 StartZ=0 EndX=-67.5 EndY=-116.913 EndZ=0
    g7: LineSegment StartX=-47.5 StartY=-82.2724 StartZ=0 EndX=-40 EndY=-69.282 EndZ=0
    g8: LineSegment StartX=40 StartY=-69.282 StartZ=0 EndX=47.5 EndY=-82.2724 EndZ=0
    g9: LineSegment StartX=67.5 StartY=-116.913 StartZ=0 EndX=75 EndY=-129.904 EndZ=0
    g10: GeomPoint [constr] X=0 Y=-129.904 Z=0
  constraints (29):
    c: Coincident(g0,g-1)
    c: Coincident(g1,g0)
    c: Coincident(g2,g0)
    c: Coincident(g3,g0)
    c: Coincident(g4,g0)
    c: Coincident(g4,g0)
    c: PointOnObject(g1,g4)
    c: PointOnObject(g3,g4)
    c: PointOnObject(g2,g4)
    c: Coincident(g5,g0)
    c: Coincident(g5,g0)
    c: PointOnObject(g3,g5)
    c: PointOnObject(g2,g5)
    c: PointOnObject(g1,g5)
    c: Coincident(g6,g0)
    c: Coincident(g6,g1)
    c: Coincident(g7,g3)
    c: Coincident(g7,g2)
    c: Coincident(g8,g2)
    c: Coincident(g8,g3)
    c: Coincident(g9,g1)
    c: Coincident(g9,g0)
    c: Equal(g9,g8)
    c: Distance(g9) = 15
    c: Distance(g2,g0) = 80
    c: PointOnObject(g10,g-2)
    c: Symmetric(g0,g0,g10)
    c: Distance(g3,g1) = 40
    c: Angle(g4,g5) = 1.0472
FEATURE [Sketcher::SketchObject] Sketch010  label="Sketch_IndexShade"
  ArcFitTolerance = 0
  AttachmentSupport = -> [DatumPlane001]
  ExternalGeometry = -> [Sketch002]
  FullyConstrained = true
  MakeInternals = false
  MapMode = 5
  Placement = pos=(0,0,2) rot=(0,0,1;0rad)
  expr: Constraints[3] = 90 ° + 2 * <<Dimensions>>.horizon_mirror_angle
  expr: Constraints[9] = Shade#Sketch010.Constraints.total_width / 2
  sketch-geometry (6):
    g0: Circle CenterX=-71.5465 CenterY=-27.4485 CenterZ=0 NormalX=0 NormalY=0 NormalZ=1 AngleXU=0 Radius=1.5
    g1: Circle CenterX=-57.4043 CenterY=-41.5906 CenterZ=0 NormalX=0 NormalY=0 NormalZ=1 AngleXU=0 Radius=1.5
    g2: LineSegment [constr] StartX=-71.5465 StartY=-27.4485 StartZ=0 EndX=-57.4043 EndY=-41.5906 EndZ=0
    g3: LineSegment [constr] StartX=0 StartY=0 StartZ=0 EndX=-49.4975 EndY=-49.4975 EndZ=0
    g4: GeomPoint [constr] X=-64.4754 Y=-34.5196 Z=0
    g5: LineSegment [constr] StartX=-64.4754 StartY=-34.5196 StartZ=0 EndX=-49.4975 EndY=-49.4975 EndZ=0
  constraints (14):
    c: Coincident(g2,g0)
    c: Coincident(g2,g1)
    c: Coincident(g3,g-1)
    c: Angle(g-2,g3) = 2.35619
    c: Symmetric(g0,g1,g4)
    c: Distance(g0,g1) = 20
    c: Coincident(g5,g4)
    c: Coincident(g5,g3)
    c: Perpendicular(g3,g5)
    c: Distance(g5) = 21.182
    c: Distance(g3) = 70
    c: Equal(g1,g0)
    c: Diameter(g0) = 3
    c: PointOnObject(g1,g5)
FEATURE [PartDesign::CoordinateSystem] Local_CS005  label="LCS_IndexShade"
  AttacherType = Attacher::AttachEngine3D
  AttachmentSupport = -> [Sketch010]
  MapMode = 45
  Placement = pos=(-64.4754,-34.5196,2) rot=(0,0,1;0.785398rad)
FEATURE [Sketcher::SketchObject] Sketch013  label="Sketch_HorizonShade"
  ArcFitTolerance = 0
  AttachmentSupport = -> [DatumPlane001]
  ExternalGeometry = -> [Sketch002]
  FullyConstrained = true
  MakeInternals = false
  MapMode = 5
  Placement = pos=(0,0,2) rot=(0,0,1;0rad)
  expr: Constraints[7] = Shade#Sketch010.Constraints.total_width / 2
  sketch-geometry (4):
    g0: Circle CenterX=-105 CenterY=-111.182 CenterZ=0 NormalX=0 NormalY=0 NormalZ=1 AngleXU=0 Radius=1.5
    g1: Circle CenterX=-105 CenterY=-91.182 CenterZ=0 NormalX=0 NormalY=0 NormalZ=1 AngleXU=0 Radius=1.5
    g2: GeomPoint [constr] X=-80 Y=-80 Z=0
    g3: GeomPoint [constr] X=-105 Y=-101.182 Z=0
  constraints (8):
    c: Symmetric(g-3,g-4,g2)
    c: Equal(g0,g1)
    c: Diameter(g0) = 3
    c: Distance(g0,g1) = 20
    c: DistanceX(g1,g2) = 25
    c: Symmetric(g1,g0,g3)
    c: Vertical(g1,g0)
    c: DistanceY(g3,g2) = 21.182
FEATURE [Sketcher::SketchObject] Sketch001  label="Sketch_HorizonMirror"
  ArcFitTolerance = 0
  AttachmentSupport = -> [XY_Plane]
  ExternalGeometry = -> [Sketch002,Sketch010,Sketch013]
  FullyConstrained = true
  MakeInternals = false
  MapMode = 5
  expr: Constraints[10] = <<Dimensions>>.horizon_mirror_mirror_width + 2 * <<Dimensions>>.mirror_frame_width
  expr: Constraints[29] = 15
  sketch-geometry (15):
    g0: LineSegment StartX=-67.0777 StartY=-116.182 StartZ=0 EndX=-31.9642 EndY=-55.3635 EndZ=0
    g1: LineSegment [constr] StartX=-87.2617 StartY=-83.0079 StartZ=0 EndX=0 EndY=0 EndZ=0
    g2: LineSegment [constr] StartX=0 StartY=0 StartZ=0 EndX=-31.9642 EndY=-55.3635 EndZ=0
    g3: LineSegment [constr] StartX=0 StartY=0 StartZ=0 EndX=31.9642 EndY=-55.3635 EndZ=0
    g4: GeomPoint [constr] X=-80 Y=-80 Z=0
    g5: ArcOfCircle CenterX=-80 CenterY=-80 CenterZ=0 NormalX=0 NormalY=0 NormalZ=1 AngleXU=0 Radius=23 StartAngle=1.61062 EndAngle=2.50249
    g6: LineSegment StartX=-69.2484 StartY=-18.0793 StartZ=0 EndX=-31.9642 EndY=-55.3635 EndZ=0
    g7: LineSegment StartX=-69.2484 StartY=-18.0793 StartZ=0 EndX=-80.9156 EndY=-29.7466 EndZ=0
    g8: LineSegment [constr] StartX=-75.082 StartY=-23.913 StartZ=0 EndX=-57.4043 EndY=-41.5906 EndZ=0
    g9: LineSegment [constr] StartX=-64.4754 StartY=-34.5196 StartZ=0 EndX=-58.6418 EndY=-28.6859 EndZ=0
    g10: LineSegment StartX=-80.9156 StartY=-29.7466 StartZ=0 EndX=-80.9156 EndY=-57.0182 EndZ=0
    g11: LineSegment StartX=-113.25 StartY=-86.182 StartZ=0 EndX=-113.25 EndY=-116.182 EndZ=0
    g12: LineSegment StartX=-113.25 StartY=-116.182 StartZ=0 EndX=-67.0777 EndY=-116.182 EndZ=0
    g13: GeomPoint [constr] X=-105 Y=-101.182 Z=0
    g14: LineSegment StartX=-113.25 StartY=-86.182 StartZ=0 EndX=-98.4605 EndY=-66.281 EndZ=0
  constraints (36):
    c: Coincident(g1,g-1)
    c: Coincident(g2,g1)
    c: Coincident(g3,g1)
    c: Symmetric(g0,g3,g-2)
    c: Angle(g2,g3) = 1.0472
    c: Parallel(g0,g2)
    c: Coincident(g5,g4)
    c: Coincident(g5,g10) = 1.5708
    c: Coincident(g-3,g1)
    c: Symmetric(g-4,g1,g5)
    c: Diameter(g5) = 46
    c: Coincident(g7,g6)
    c: Perpendicular(g6,g7)
    c: Coincident(g8,g-6)
    c: Parallel(g8,g6)
    c: PointOnObject(g9,g6)
    c: Perpendicular(g8,g9)
    c: Coincident(g10,g7)
    c: Vertical(g10)
    c: Distance(g7) = 16.5
    c: PointOnObject(g-5,g8)
    c: Symmetric(g-5,g8,g9)
    c: Symmetric(g7,g6,g8)
    c: Distance(g6,g9) = 15
    c: Vertical(g11)
    c: Coincident(g12,g11)
    c: Coincident(g12,g0)
    c: Horizontal(g12)
    c: Symmetric(g-8,g-7,g13)
    c: DistanceY(g11,g13) = 15
    c: DistanceX(g11,g13) = 8.25
    c: Coincident(g14,g11)
    c: Tangent(g14,g5) = 1.5708
    c: Distance(g11) = 30
    c: Coincident(g0,g6)
    c: Coincident(g0,g2)
FEATURE [PartDesign::CoordinateSystem] Local_CS006  label="LCS_HorizonShade"
  AttacherType = Attacher::AttachEngine3D
  AttachmentSupport = -> [Sketch013]
  MapMode = 45
  Placement = pos=(-105,-101.182,2) rot=(0,0,1;0rad)
FEATURE [Sketcher::SketchObject] Sketch015
  ArcFitTolerance = 0
  AttachmentSupport = -> [DatumPlane]
  ExternalGeometry = -> [Sketch009]
  FullyConstrained = true
  MakeInternals = false
  MapMode = 5
  sketch-geometry (12):
    g0: ArcOfCircle CenterX=0 CenterY=0 CenterZ=0 NormalX=0 NormalY=0 NormalZ=1 AngleXU=0 Radius=84.5 StartAngle=4.18879 EndAngle=5.23599
    g1: ArcOfCircle CenterX=0 CenterY=0 CenterZ=0 NormalX=0 NormalY=0 NormalZ=1 AngleXU=0 Radius=90.5 StartAngle=4.18879 EndAngle=5.23599
    g2: ArcOfCircle CenterX=0 CenterY=0 CenterZ=0 NormalX=0 NormalY=0 NormalZ=1 AngleXU=0 Radius=139.5 StartAngle=4.18879 EndAngle=5.23599
    g3: ArcOfCircle CenterX=0 CenterY=0 CenterZ=0 NormalX=0 NormalY=0 NormalZ=1 AngleXU=0 Radius=145.5 StartAngle=4.18879 EndAngle=5.23599
    g4: LineSegment StartX=-42.25 StartY=-73.1791 StartZ=0 EndX=-45.25 EndY=-78.3753 EndZ=0
    g5: LineSegment StartX=42.25 StartY=-73.1791 StartZ=0 EndX=45.25 EndY=-78.3753 EndZ=0
    g6: LineSegment StartX=-69.75 StartY=-120.811 StartZ=0 EndX=-72.75 EndY=-126.007 EndZ=0
    g7: LineSegment StartX=69.75 StartY=-120.811 StartZ=0 EndX=72.75 EndY=-126.007 EndZ=0
    g8: LineSegment [constr] StartX=-40 StartY=-69.282 StartZ=0 EndX=-42.25 EndY=-73.1791 EndZ=0
    g9: LineSegment [constr] StartX=-45.25 StartY=-78.3753 StartZ=0 EndX=-47.5 EndY=-82.2724 EndZ=0
    g10: LineSegment [constr] StartX=-69.75 StartY=-120.811 StartZ=0 EndX=-67.5 EndY=-116.913 EndZ=0
    g11: LineSegment [constr] StartX=-72.75 StartY=-126.007 StartZ=0 EndX=-75 EndY=-129.904 EndZ=0
  constraints (32):
    c: Coincident(g0,g-9)
    c: PointOnObject(g0,g-3)
    c: PointOnObject(g0,g-6)
    c: Coincident(g1,g0)
    c: PointOnObject(g1,g-6)
    c: PointOnObject(g1,g-3)
    c: Coincident(g2,g0)
    c: PointOnObject(g2,g-10)
    c: PointOnObject(g2,g-7)
    c: Coincident(g3,g0)
    c: PointOnObject(g3,g-7)
    c: PointOnObject(g3,g-10)
    c: Coincident(g4,g0)
    c: Coincident(g4,g1)
    c: Coincident(g5,g0)
    c: Coincident(g5,g1)
    c: Coincident(g6,g2)
    c: Coincident(g6,g3)
    c: Coincident(g7,g2)
    c: Coincident(g7,g3)
    c: Coincident(g8,g-5)
    c: Coincident(g8,g0)
    c: Coincident(g9,g1)
    c: Coincident(g9,g-4)
    c: Equal(g9,g8)
    c: Distance(g4) = 6
    c: Coincident(g10,g2)
    c: Coincident(g10,g-10)
    c: Coincident(g11,g3)
    c: Coincident(g11,g-10)
    c: Equal(g10,g11)
    c: Distance(g6) = 6
FEATURE [Sketcher::SketchObject] Sketch016  label="Sketch_HolesStand"
  ArcFitTolerance = 0
  AttachmentSupport = -> [DatumPlane001]
  FullyConstrained = true
  MakeInternals = false
  MapMode = 5
  Placement = pos=(0,0,2) rot=(0,0,1;0rad)
  sketch-geometry (5):
    g0: Circle CenterX=-80 CenterY=-138.564 CenterZ=0 NormalX=0 NormalY=0 NormalZ=1 AngleXU=0 Radius=1.5
    g1: Circle CenterX=-17.5 CenterY=-30.3109 CenterZ=0 NormalX=0 NormalY=0 NormalZ=1 AngleXU=0 Radius=1.5
    g2: Circle CenterX=17.5 CenterY=-30.3109 CenterZ=0 NormalX=0 NormalY=0 NormalZ=1 AngleXU=0 Radius=1.5
    g3: Circle CenterX=80 CenterY=-138.564 CenterZ=0 NormalX=0 NormalY=0 NormalZ=1 AngleXU=0 Radius=1.5
    g4: LineSegment [constr] StartX=0 StartY=0 StartZ=0 EndX=-80 EndY=-138.564 EndZ=0
  constraints (12):
    c: Coincident(g4,g-1)
    c: Coincident(g4,g0)
    c: Equal(g1,g2)
    c: Equal(g2,g0)
    c: Equal(g0,g3)
    c: Symmetric(g1,g2,g-2)
    c: Diameter(g1) = 3
    c: Symmetric(g0,g3,g-2)
    c: Angle(g-2,g4) = 2.61799
    c: Distance(g1,g4) = 35
    c: Distance(g4,g0) = 160
    c: PointOnObject(g1,g4)
FEATURE [Sketcher::SketchObject] Sketch014
  ArcFitTolerance = 0
  AttachmentSupport = -> [DatumPlane]
  ExternalGeometry = -> [Sketch,Sketch016,Sketch006]
  FullyConstrained = true
  MakeInternals = false
  MapMode = 5
  expr: Constraints[10] = <<Dimensions>>.clearance_loose_fit
  expr: Constraints[21] = 22.5 mm + <<Dimensions>>.clearance_loose_fit
  sketch-geometry (30):
    g0: LineSegment StartX=-13.8737 StartY=-18.03 StartZ=0 EndX=-17.5 EndY=-24.3109 EndZ=0
    g1: LineSegment StartX=-8.67759 StartY=-21.03 StartZ=0 EndX=-12.3038 EndY=-27.3109 EndZ=0
    g2: LineSegment [constr] StartX=-91.4124 StartY=-143.331 StartZ=0 EndX=-87.4598 EndY=-145.485 EndZ=0
    g3: LineSegment [constr] StartX=-82.2637 StartY=-148.485 StartZ=0 EndX=-78.422 EndY=-150.831 EndZ=0
    g4: ArcOfCircle [constr] CenterX=1.581e-13 CenterY=-7.68e-14 CenterZ=0 NormalX=0 NormalY=0 NormalZ=1 AngleXU=0 Radius=170 StartAngle=4.14466 EndAngle=4.23292
    g5: GeomPoint [constr] X=-85 Y=-147.224 Z=0
    g6: LineSegment [constr] StartX=-85 StartY=-147.224 StartZ=0 EndX=-84.875 EndY=-147.008 EndZ=0
    g7: GeomPoint [constr] X=-84.9172 Y=-147.081 Z=0
    g8: LineSegment StartX=-3 StartY=-169.723 StartZ=0 EndX=-3 EndY=-140.196 EndZ=0
    g9: ArcOfCircle CenterX=1.581e-13 CenterY=-7.68e-14 CenterZ=0 NormalX=0 NormalY=0 NormalZ=1 AngleXU=0 Radius=169.75 StartAngle=4.69472 EndAngle=4.71239
    g10: ArcOfCircle CenterX=1.581e-13 CenterY=-7.68e-14 CenterZ=0 NormalX=0 NormalY=0 NormalZ=1 AngleXU=0 Radius=22.75 StartAngle=4.05654 EndAngle=4.32104
    g11: ArcOfCircle CenterX=1.581e-13 CenterY=-7.68e-14 CenterZ=0 NormalX=0 NormalY=0 NormalZ=1 AngleXU=0 Radius=169.75 StartAngle=4.17112 EndAngle=4.20646
    g12: LineSegment StartX=-7.7e-15 StartY=-22.75 StartZ=0 EndX=4e-16 EndY=-39 EndZ=0
    g13: ArcOfCircle CenterX=-80 CenterY=-138.564 CenterZ=0 NormalX=0 NormalY=0 NormalZ=1 AngleXU=0 Radius=6 StartAngle=0.523599 EndAngle=1.5708
    g14: ArcOfCircle CenterX=-80 CenterY=-138.564 CenterZ=0 NormalX=0 NormalY=0 NormalZ=1 AngleXU=0 Radius=6 StartAngle=3.66519 EndAngle=4.71239
    g15: LineSegment StartX=-85.1962 StartY=-141.564 StartZ=0 EndX=-87.4598 EndY=-145.485 EndZ=0
    g16: LineSegment StartX=-80 StartY=-144.564 StartZ=0 EndX=-82.2637 EndY=-148.485 EndZ=0
    g17: ArcOfCircle CenterX=-17.5 CenterY=-30.3109 CenterZ=0 NormalX=0 NormalY=0 NormalZ=1 AngleXU=0 Radius=6 StartAngle=0.523599 EndAngle=1.5708
    g18: ArcOfCircle CenterX=-17.5 CenterY=-30.3109 CenterZ=0 NormalX=0 NormalY=0 NormalZ=1 AngleXU=0 Radius=6 StartAngle=3.66519 EndAngle=4.71239
    g19: LineSegment StartX=-22.6962 StartY=-33.3109 StartZ=0 EndX=-80 EndY=-132.564 EndZ=0
    g20: LineSegment StartX=-17.5 StartY=-36.3109 StartZ=0 EndX=-74.8038 EndY=-135.564 EndZ=0
    g21: ArcOfCircle CenterX=0 CenterY=-45 CenterZ=0 NormalX=0 NormalY=0 NormalZ=1 AngleXU=0 Radius=6 StartAngle=1.5708 EndAngle=2.0944
    g22: ArcOfCircle CenterX=0 CenterY=-45 CenterZ=0 NormalX=0 NormalY=0 NormalZ=1 AngleXU=0 Radius=6 StartAngle=4.18879 EndAngle=4.71239
    g23: ArcOfCircle CenterX=0 CenterY=-135 CenterZ=0 NormalX=0 NormalY=0 NormalZ=1 AngleXU=0 Radius=6 StartAngle=1.5708 EndAngle=2.0944
    g24: ArcOfCircle CenterX=0 CenterY=-135 CenterZ=0 NormalX=0 NormalY=0 NormalZ=1 AngleXU=0 Radius=6 StartAngle=4.18879 EndAngle=4.71239
    g25: LineSegment StartX=-1.1e-15 StartY=-51 StartZ=0 EndX=4e-16 EndY=-129 EndZ=0
    g26: LineSegment StartX=-3 StartY=-39.8038 StartZ=0 EndX=-3 EndY=-22.5513 EndZ=0
    g27: LineSegment StartX=-1.1e-15 StartY=-141 StartZ=0 EndX=-2.39e-14 EndY=-169.75 EndZ=0
    g28: LineSegment StartX=-3 StartY=-129.804 StartZ=0 EndX=-3 EndY=-50.1962 EndZ=0
    g29: ArcOfCircle CenterX=1.581e-13 CenterY=-7.68e-14 CenterZ=0 NormalX=0 NormalY=0 NormalZ=1 AngleXU=0 Radius=22.75 StartAngle=4.58014 EndAngle=4.71239
  constraints (79):
    c: Coincident(g2,g-3)
    c: Coincident(g2,g15)
    c: Coincident(g3,g16)
    c: Coincident(g3,g-4)
    c: Equal(g3,g2)
    c: Coincident(g4,g2)
    c: Coincident(g4,g3)
    c: PointOnObject(g5,g4)
    c: Coincident(g6,g5)
    c: Perpendicular(g4,g6)
    c: Distance(g6) = 0.25
    c: Symmetric(g2,g3,g7)
    c: PointOnObject(g7,g6)
    c: Parallel(g-3,g0)
    c: Equal(g-6,g4)
    c: Coincident(g9,g8)
    c: PointOnObject(g9,g-2)
    c: Parallel(g8,g-7)
    c: DistanceX(g8,g9) = 3
    c: Coincident(g10,g9)
    c: Coincident(g10,g0)
    c: Radius(g10) = 22.75
    c: Coincident(g9,g4)
    c: Coincident(g11,g15)
    c: Coincident(g11,g16)
    c: PointOnObject(g6,g11)
    c: Coincident(g11,g9)
    c: Distance(g15,g16) = 6
    c: Equal(g11,g9)
    c: PointOnObject(g29,g-2)
    c: Coincident(g12,g29)
    c: Coincident(g27,g9)
    c: Coincident(g13,g-9)
    c: Coincident(g14,g13)
    c: Radius(g13) = 6
    c: Coincident(g19,g13)
    c: Coincident(g15,g14)
    c: Coincident(g20,g13)
    c: Coincident(g16,g14)
    c: Equal(g14,g13)
    c: Tangent(g15,g0)
    c: Coincident(g17,g-8)
    c: Coincident(g18,g17)
    c: Coincident(g0,g17)
    c: Coincident(g19,g18)
    c: Coincident(g1,g17)
    c: Coincident(g20,g18)
    c: Equal(g17,g18)
    c: Equal(g18,g13)
    c: Tangent(g20,g1)
    c: Tangent(g19,g0)
    c: Coincident(g21,g-10)
    c: Coincident(g22,g21)
    c: Coincident(g23,g-11)
    c: Coincident(g24,g23)
    c: Equal(g24,g23)
    c: Equal(g23,g22)
    c: Equal(g22,g21)
    c: Radius(g21) = 6
    c: Coincident(g12,g21)
    c: Coincident(g28,g22)
    c: Coincident(g26,g21)
    c: Coincident(g8,g24)
    c: Coincident(g28,g23)
    c: Coincident(g27,g24)
    c: PointOnObject(g24,g-2)
    c: Tangent(g8,g28)
    c: Coincident(g25,g23)
    c: PointOnObject(g23,g-2)
    c: Coincident(g22,g25)
    c: PointOnObject(g22,g-2)
    c: PointOnObject(g12,g-2)
    c: Tangent(g26,g28)
    c: Equal(g10,g29)
    c: Coincident(g10,g1)
    c: Coincident(g29,g26)
    c: Coincident(g10,g29)
    c: Tangent(g16,g20)
    c: Parallel(g20,g-4)
FEATURE [PartDesign::Pad] Pad006
  BaseFeature = -> Pad
  Direction = (0,0,1)
  Length = 3
  Length2 = 10
  Profile = -> Sketch014
  ReferenceAxis = -> Sketch014 [N_Axis]
  Reversed = true
  Suppressed = false
  Type = 0
FEATURE [PartDesign::Mirrored] Mirrored
  BaseFeature = -> Pad006
  MirrorPlane = -> Sketch [V_Axis]
  Originals = -> [Pad,Pad006]
  Refine = true
  Suppressed = false
  TransformMode = 0
FEATURE [PartDesign::Pad] Pad003
  BaseFeature = -> Mirrored
  Direction = (0,0,1)
  Length = 10
  Length2 = 10
  Profile = -> Sketch009
  ReferenceAxis = -> Sketch009 [N_Axis]
  Refine = true
  Suppressed = false
  Type = 3
  UpToFace = -> DatumPlane001 [Plane]
FEATURE [PartDesign::Pad] Pad007
  BaseFeature = -> Pad003
  Direction = (0,0,1)
  Length = 3
  Length2 = 10
  Profile = -> Sketch015
  ReferenceAxis = -> Sketch015 [N_Axis]
  Refine = true
  Reversed = true
  Suppressed = false
  Type = 0
FEATURE [PartDesign::Hole] Hole007  label="Holes_Stand"
  BaseFeature = -> Pad007
  CustomThreadClearance = 0
  Depth = 639.366
  DepthType = 1
  Diameter = 3.4
  DrillForDepth = false
  DrillPoint = 1
  DrillPointAngle = 118
  HoleCutCountersinkAngle = 90
  HoleCutCustomValues = false
  HoleCutDepth = 0
  HoleCutDiameter = 6.7
  HoleCutType = 5
  ModelThread = false
  Profile = -> Sketch016
  Suppressed = false
  Tapered = false
  TaperedAngle = 90
  ThreadClass = 0
  ThreadDepth = 639.366
  ThreadDepthType = 0
  ThreadDirection = 0
  ThreadFit = 0
  ThreadSize = 9
  ThreadType = 1
  Threaded = false
  UseCustomThreadClearance = false
FEATURE [PartDesign::Hole] Hole003  label="Hole_Handle"
  BaseFeature = -> Hole007
  CustomThreadClearance = 0
  Depth = 703.91
  DepthType = 1
  Diameter = 3.4
  DrillForDepth = false
  DrillPoint = 1
  DrillPointAngle = 118
  HoleCutCountersinkAngle = 90
  HoleCutCustomValues = false
  HoleCutDepth = 0
  HoleCutDiameter = 6.72
  HoleCutType = 2
  ModelThread = false
  Profile = -> Sketch006
  Suppressed = false
  Tapered = false
  TaperedAngle = 90
  ThreadClass = 0
  ThreadDepth = 639.366
  ThreadDepthType = 0
  ThreadDirection = 0
  ThreadFit = 0
  ThreadSize = 9
  ThreadType = 1
  Threaded = false
  UseCustomThreadClearance = false
  expr: HoleCutDiameter = <<Dimensions>>.handle_countersink_diameter
  expr: ThreadSize = <<Dimensions>>.handle_screw_type
FEATURE [PartDesign::Pad] Pad001  label="Pad_HorizonMirror"
  BaseFeature = -> Hole003
  Direction = (0,0,1)
  Length = 2
  Length2 = 10
  Profile = -> Sketch001
  ReferenceAxis = -> Sketch001 [N_Axis]
  Refine = true
  Suppressed = false
  Type = 0
  expr: Length = Pad.Length
FEATURE [Sketcher::SketchObject] Sketch018
  ArcFitTolerance = 0
  AttachmentSupport = -> [DatumPlane]
  ExternalGeometry = -> [Sketch004,Sketch003]
  FullyConstrained = true
  MakeInternals = false
  MapMode = 5
  expr: Constraints[15] = 4.5 + 1.5
  expr: Constraints[8] = 4.5 + 1.5
  sketch-geometry (6):
    g0: LineSegment StartX=38.3938 StartY=-66.5 StartZ=0 EndX=79.0839 EndY=-66.5 EndZ=0
    g1: ArcOfCircle CenterX=85 CenterY=-65.5 CenterZ=0 NormalX=0 NormalY=0 NormalZ=1 AngleXU=0 Radius=6 StartAngle=3.30904 EndAngle=4.58706
    g2: LineSegment StartX=84.25 StartY=-71.4529 StartZ=0 EndX=84.25 EndY=-88.5471 EndZ=0
    g3: LineSegment StartX=79.0839 StartY=-93.5 StartZ=0 EndX=53.9823 EndY=-93.5 EndZ=0
    g4: ArcOfCircle CenterX=85 CenterY=-94.5 CenterZ=0 NormalX=0 NormalY=0 NormalZ=1 AngleXU=0 Radius=6 StartAngle=1.69612 EndAngle=2.97414
    g5: LineSegment StartX=38.3938 StartY=-66.5 StartZ=0 EndX=53.9823 EndY=-93.5 EndZ=0
  constraints (18):
    c: PointOnObject(g0,g-4)
    c: Horizontal(g0)
    c: Parallel(g3,g-5)
    c: DistanceY(g0,g-4) = 4.5
    c: Coincident(g1,g-7)
    c: Coincident(g0,g1)
    c: Coincident(g2,g1)
    c: Parallel(g2,g-6)
    c: Radius(g1) = 6
    c: DistanceX(g1,g-6) = 4.5
    c: Coincident(g4,g-8)
    c: Coincident(g4,g2)
    c: Coincident(g4,g3)
    c: PointOnObject(g3,g-4)
    c: DistanceY(g-5,g3) = 4.5
    c: Radius(g4) = 6
    c: Coincident(g5,g0)
    c: Coincident(g5,g3)
FEATURE [Sketcher::SketchObject] Sketch019
  ArcFitTolerance = 0
  AttachmentSupport = -> [DatumPlane]
  ExternalGeometry = -> [Sketch001,Sketch013,Sketch002,Sketch010]
  FullyConstrained = true
  MakeInternals = false
  MapMode = 5
  sketch-geometry (19):
    g0: LineSegment StartX=-34.2935 StartY=-59.3981 StartZ=0 EndX=-51.4408 EndY=-42.2509 EndZ=0
    g1: LineSegment StartX=-76.4156 StartY=-30.9544 StartZ=0 EndX=-76.4156 EndY=-61.8506 EndZ=0
    g2: ArcOfCircle CenterX=-80 CenterY=-80 CenterZ=0 NormalX=0 NormalY=0 NormalZ=1 AngleXU=0 Radius=18.5 StartAngle=1.37581 EndAngle=2.50249
    g3: LineSegment StartX=-94.8486 StartY=-68.9651 StartZ=0 EndX=-107.215 EndY=-85.6059 EndZ=0
    g4: LineSegment StartX=-108.75 StartY=-95.8657 StartZ=0 EndX=-108.75 EndY=-106.498 EndZ=0
    g5: LineSegment StartX=-99.0209 StartY=-111.682 StartZ=0 EndX=-64.4796 EndY=-111.682 EndZ=0
    g6: LineSegment StartX=-64.4796 StartY=-111.682 StartZ=0 EndX=-34.2935 EndY=-59.3981 EndZ=0
    g7: ArcOfCircle CenterX=-71.5465 CenterY=-27.4485 CenterZ=0 NormalX=0 NormalY=0 NormalZ=1 AngleXU=0 Radius=6 StartAngle=3.76563 EndAngle=6.17292
    g8: LineSegment [constr] StartX=-76.4156 StartY=-30.9544 StartZ=0 EndX=-80.9156 EndY=-30.9544 EndZ=0
    g9: LineSegment [constr] StartX=-98.4605 StartY=-66.281 StartZ=0 EndX=-94.8486 EndY=-68.9651 EndZ=0
    g10: Circle CenterX=-72.7383 CenterY=-76.9921 CenterZ=0 NormalX=0 NormalY=0 NormalZ=1 AngleXU=0 Radius=6
    g11: Circle CenterX=-87.2617 CenterY=-83.0079 CenterZ=0 NormalX=0 NormalY=0 NormalZ=1 AngleXU=0 Radius=6
    g12: ArcOfCircle CenterX=-105 CenterY=-91.182 CenterZ=0 NormalX=0 NormalY=0 NormalZ=1 AngleXU=0 Radius=6 StartAngle=4.03726 EndAngle=8.23215
    g13: ArcOfCircle CenterX=-57.4043 CenterY=-41.5906 CenterZ=0 NormalX=0 NormalY=0 NormalZ=1 AngleXU=0 Radius=6 StartAngle=1.68106 EndAngle=6.17292
    g14: LineSegment StartX=-58.0646 StartY=-35.6271 StartZ=0 EndX=-65.5829 EndY=-28.1087 EndZ=0
    g15: ArcOfCircle CenterX=-105 CenterY=-111.182 CenterZ=0 NormalX=0 NormalY=0 NormalZ=1 AngleXU=0 Radius=6 StartAngle=6.19976 EndAngle=8.52911
    g16: LineSegment [constr] StartX=-51.4408 StartY=-42.2509 StartZ=0 EndX=-48.2588 EndY=-39.0689 EndZ=0
    g17: LineSegment [constr] StartX=-108.75 StartY=-95.8657 StartZ=0 EndX=-113.25 EndY=-95.8657 EndZ=0
    g18: LineSegment [constr] StartX=-99.0209 StartY=-111.682 StartZ=0 EndX=-99.0209 EndY=-116.182 EndZ=0
  constraints (53):
    c: PointOnObject(g0,g-3)
    c: PointOnObject(g5,g-3)
    c: Coincident(g5,g6)
    c: Coincident(g6,g0)
    c: Parallel(g0,g-4)
    c: Coincident(g7,g-16)
    c: Radius(g7) = 6
    c: Coincident(g14,g7)
    c: Coincident(g1,g7)
    c: Coincident(g8,g1)
    c: PointOnObject(g8,g-6)
    c: Perpendicular(g8,g1)
    c: Distance(g8) = 4.5
    c: Coincident(g-7,g2)
    c: Parallel(g-6,g1)
    c: Coincident(g2,g1)
    c: Coincident(g9,g-8)
    c: Coincident(g9,g2)
    c: Perpendicular(g9,g-8)
    c: Distance(g9) = 4.5
    c: Parallel(g-8,g3)
    c: Coincident(g10,g-15)
    c: Coincident(g11,g-13)
    c: Diameter(g10) = 12
    c: Diameter(g11) = 12
    c: Coincident(g12,g-12)
    c: Radius(g12) = 6
    c: Coincident(g13,g-14)
    c: Radius(g13) = 6
    c: Coincident(g0,g13)
    c: Coincident(g14,g13)
    c: Tangent(g14,g0)
    c: Coincident(g15,g-11)
    c: Radius(g15) = 6
    c: Coincident(g4,g15)
    c: Coincident(g5,g15)
    c: Coincident(g3,g12)
    c: Coincident(g4,g12)
    c: Parallel(g4,g-10)
    c: Coincident(g16,g0)
    c: PointOnObject(g16,g-4)
    c: Perpendicular(g0,g16)
    c: Distance(g16) = 4.5
    c: Coincident(g2,g3)
    c: Coincident(g17,g4)
    c: PointOnObject(g17,g-10)
    c: Perpendicular(g-10,g17)
    c: Distance(g17) = 4.5
    c: Coincident(g18,g5)
    c: PointOnObject(g18,g-9)
    c: Perpendicular(g-9,g18)
    c: Equal(g18,g17)
    c: Parallel(g5,g-9)
FEATURE [PartDesign::Pad] Pad009
  BaseFeature = -> Pad001
  Direction = (0,0,1)
  Length = 3
  Length2 = 10
  Profile = -> Sketch019
  ReferenceAxis = -> Sketch019 [N_Axis]
  Refine = true
  Reversed = true
  Suppressed = false
  Type = 0
FEATURE [PartDesign::Hole] Hole001  label="Holes_HorizonMirror"
  BaseFeature = -> Pad009
  CustomThreadClearance = 0
  Depth = 25
  DepthType = 0
  Diameter = 3.2
  DrillForDepth = false
  DrillPoint = 1
  DrillPointAngle = 118
  HoleCutCountersinkAngle = 90
  HoleCutCustomValues = false
  HoleCutDepth = 0
  HoleCutDiameter = 6.1
  HoleCutType = 0
  ModelThread = false
  Profile = -> Sketch002
  Reversed = true
  Suppressed = false
  Tapered = false
  TaperedAngle = 90
  ThreadClass = 0
  ThreadDepth = 25
  ThreadDepthType = 0
  ThreadDirection = 0
  ThreadFit = 1
  ThreadSize = 9
  ThreadType = 1
  Threaded = false
  UseCustomThreadClearance = false
  expr: ThreadSize = <<Dimensions>>.horizon_mirror_screw_type
FEATURE [PartDesign::Hole] Hole005  label="Holes_IndexShade"
  BaseFeature = -> Hole001
  CustomThreadClearance = 0
  Depth = 25
  DepthType = 0
  Diameter = 3.4
  DrillForDepth = false
  DrillPoint = 1
  DrillPointAngle = 118
  HoleCutCountersinkAngle = 90
  HoleCutCustomValues = false
  HoleCutDepth = 0
  HoleCutDiameter = 6.1
  HoleCutType = 0
  ModelThread = false
  Profile = -> Sketch010
  Suppressed = false
  Tapered = false
  TaperedAngle = 90
  ThreadClass = 0
  ThreadDepth = 25
  ThreadDepthType = 0
  ThreadDirection = 0
  ThreadFit = 0
  ThreadSize = 9
  ThreadType = 1
  Threaded = false
  UseCustomThreadClearance = false
FEATURE [PartDesign::Hole] Hole006  label="Holes_HorizonShade"
  BaseFeature = -> Hole005
  CustomThreadClearance = 0
  Depth = 711.3
  DepthType = 1
  Diameter = 3.4
  DrillForDepth = false
  DrillPoint = 1
  DrillPointAngle = 118
  HoleCutCountersinkAngle = 90
  HoleCutCustomValues = false
  HoleCutDepth = 0
  HoleCutDiameter = 6.1
  HoleCutType = 0
  ModelThread = false
  Profile = -> Sketch013
  Suppressed = false
  Tapered = false
  TaperedAngle = 90
  ThreadClass = 0
  ThreadDepth = 711.3
  ThreadDepthType = 0
  ThreadDirection = 0
  ThreadFit = 0
  ThreadSize = 9
  ThreadType = 1
  Threaded = false
  UseCustomThreadClearance = false
FEATURE [PartDesign::Pad] Pad002
  BaseFeature = -> Hole006
  Direction = (0,0,1)
  Length = 2
  Length2 = 10
  Profile = -> Sketch004
  ReferenceAxis = -> Sketch004 [N_Axis]
  Refine = true
  Suppressed = false
  Type = 0
  expr: Length = Pad.Length
FEATURE [PartDesign::Hole] Hole002
  BaseFeature = -> Pad002
  CustomThreadClearance = 0
  Depth = 639.366
  DepthType = 1
  Diameter = 3.4
  DrillForDepth = false
  DrillPoint = 1
  DrillPointAngle = 118
  HoleCutCountersinkAngle = 90
  HoleCutCustomValues = false
  HoleCutDepth = 0
  HoleCutDiameter = 6.1
  HoleCutType = 0
  ModelThread = false
  Profile = -> Sketch003
  Reversed = true
  Suppressed = false
  Tapered = false
  TaperedAngle = 90
  ThreadClass = 0
  ThreadDepth = 639.366
  ThreadDepthType = 0
  ThreadDirection = 0
  ThreadFit = 0
  ThreadSize = 9
  ThreadType = 1
  Threaded = false
  UseCustomThreadClearance = false
  expr: ThreadSize = <<Dimensions>>.viewscope_screw_type
FEATURE [PartDesign::Pad] Pad008
  BaseFeature = -> Hole002
  Direction = (0,0,1)
  Length = 3
  Length2 = 10
  Profile = -> Sketch018
  ReferenceAxis = -> Sketch018 [N_Axis]
  Refine = true
  Reversed = true
  Suppressed = false
  Type = 0
FEATURE [PartDesign::Hole] Hole
  BaseFeature = -> Pad008
  CustomThreadClearance = 0
  Depth = 641.896
  DepthType = 1
  Diameter = 3.4
  DrillForDepth = false
  DrillPoint = 1
  DrillPointAngle = 118
  HoleCutCountersinkAngle = 90
  HoleCutCustomValues = false
  HoleCutDepth = 0
  HoleCutDiameter = 6.1
  HoleCutType = 0
  ModelThread = false
  Profile = -> Binder
  Reversed = true
  Suppressed = false
  Tapered = false
  TaperedAngle = 90
  ThreadClass = 0
  ThreadDepth = 641.896
  ThreadDepthType = 0
  ThreadDirection = 0
  ThreadFit = 0
  ThreadSize = 9
  ThreadType = 1
  Threaded = false
  UseCustomThreadClearance = false
FEATURE [PartDesign::Pocket] Pocket
  BaseFeature = -> Hole
  Direction = (0,0,-1)
  Length = 5
  Length2 = 5
  Profile = -> Sketch007
  ReferenceAxis = -> Sketch007 [N_Axis]
  Reversed = true
  Suppressed = false
  Type = 1
FEATURE [PartDesign::Hole] Hole004
  BaseFeature = -> Pocket
  CustomThreadClearance = 0
  Depth = 703.91
  DepthType = 1
  Diameter = 3.4
  DrillForDepth = false
  DrillPoint = 1
  DrillPointAngle = 118
  HoleCutCountersinkAngle = 90
  HoleCutCustomValues = false
  HoleCutDepth = 0
  HoleCutDiameter = 6.7
  HoleCutType = 5
  ModelThread = false
  Profile = -> Sketch008
  Suppressed = false
  Tapered = false
  TaperedAngle = 90
  ThreadClass = 0
  ThreadDepth = 639.366
  ThreadDepthType = 0
  ThreadDirection = 0
  ThreadFit = 0
  ThreadSize = 9
  ThreadType = 1
  Threaded = false
  UseCustomThreadClearance = false
  expr: ThreadSize = <<Dimensions>>.bearing_housing_screw_type
FEATURE [PartDesign::PolarPattern] PolarPattern
  Angle = 360
  Axis = -> Z_Axis
  BaseFeature = -> Hole004
  Mode = 0
  Occurrences = 3
  Offset = 120
  Originals = -> [Hole004]
  Suppressed = false
  TransformMode = 0
FEATURE [PartDesign::Draft] Draft001
  Angle = 20
  Base = -> PolarPattern [Face52,Face54,Face56,Face58,Face24,Face60,Face25,Face27,Face62,Face64,Face66,Face68,Face40,Face41,Face43,Face70,Face72,Face74,Face75,Face73,Face71,Face69,Face65,Face61,Face59,Face57,Face55,Face98,Face96,Face51,Face53,Face49,Face47,Face46,Face48,Face50,Face143,Face144,Face77,Face79,+21 more]
  BaseFeature = -> PolarPattern
  NeutralPlane = -> DatumPlane
  Refine = true
  Reversed = true
  SupportTransform = false
  Suppressed = false
FEATURE [PartDesign::Line] DatumLine  label="Screw_Stand1"
  AttacherType = Attacher::AttachEngineLine
  AttachmentSupport = -> [Sketch016]
  Length = 20
  MapMode = 19
  Placement = pos=(-80,-138.564,2) rot=(0,0,1;0rad)
  ResizeMode = 0
FEATURE [PartDesign::Line] DatumLine001  label="Screw_Stand3"
  AttacherType = Attacher::AttachEngineLine
  AttachmentSupport = -> [Sketch016]
  Length = 20
  MapMode = 19
  Placement = pos=(17.5,-30.3109,2) rot=(0,0,1;0rad)
  ResizeMode = 0
FEATURE [PartDesign::Line] DatumLine002  label="Screw_Stand4"
  AttacherType = Attacher::AttachEngineLine
  AttachmentSupport = -> [Sketch016]
  Length = 20
  MapMode = 19
  Placement = pos=(-17.5,-30.3109,2) rot=(0,0,1;0rad)
  ResizeMode = 0
FEATURE [PartDesign::Line] DatumLine003  label="Screw_Stand2"
  AttacherType = Attacher::AttachEngineLine
  AttachmentSupport = -> [Sketch016]
  Length = 20
  MapMode = 19
  Placement = pos=(80,-138.564,2) rot=(0,0,1;0rad)
  ResizeMode = 0
FEATURE [PartDesign::Line] DatumLine004  label="Screw_Viewscope1"
  AttacherType = Attacher::AttachEngineLine
  AttachmentSupport = -> [Sketch003]
  Length = 20
  MapMode = 19
  Placement = pos=(85,-65.5,0) rot=(0,0,1;0rad)
  ResizeMode = 0
FEATURE [PartDesign::Line] DatumLine005  label="Screw_Viewscope2"
  AttacherType = Attacher::AttachEngineLine
  AttachmentSupport = -> [Sketch003]
  Length = 20
  MapMode = 19
  Placement = pos=(85,-94.5,0) rot=(0,0,1;0rad)
  ResizeMode = 0
FEATURE [PartDesign::Body] Body  label="Frame"
  AllowCompound = false
  Group = -> [DatumPlane,DatumPlane001,LCS_Origin,Pad,Pad006,Sketch014,Mirrored,Pad003,Sketch009,Sketch,Sketch006,Binder,Sketch001,Sketch002,Sketch015,Pad007,Sketch016,Hole007,DatumLine,DatumLine003,DatumLine001,DatumLine002,Hole003,LCS_Handle,HoleAxis_1,HoleAxis_2,Pad001,Sketch019,Pad009,Hole001,Local_CS,Hole005,Local_CS005,Hole006,Local_CS006,Sketch003,Sketch004,Pad002,Hole002,Local_CS001,Sketch018,+15 more]
  Origin = -> Origin
  Tip = -> Draft001
FEATURE [TechDraw::DrawViewPart] View
  CoarseView = false
  Direction = (0,0,1)
  Focus = 100
  HardHidden = false
  IsoCount = 0
  IsoHidden = false
  IsoVisible = false
  LockPosition = false
  Perspective = false
  Rotation = -45
  ScaleType = 0
  ScrubCount = 0
  SeamHidden = false
  SeamVisible = false
  SmoothHidden = false
  SmoothVisible = true
  Source = -> [Body]
  X = 173.52
  XDirection = (1,0,0)
  Y = 132.141
FEATURE [TechDraw::DrawPage] Page
  KeepUpdated = true
  NextBalloonIndex = 1
  ProjectionType = 0
  Template = -> Template
  Views = -> [View]
---- part Handle.FCStd = doc fcstd_d59618b661a9 ----
FCSTD DOCUMENT  (FreeCAD 0.21RUnknown)
Label: Handle
License: All rights reserved
LicenseURL: http://en.wikipedia.org/wiki/All_rights_reserved
objects: PartDesign::Body×4, Sketcher::SketchObject×3, PartDesign::FeatureBase×3, PartDesign::Hole×2, PartDesign::CoordinateSystem×2, PartDesign::SubShapeBinder×2, PartDesign::Pad×1, PartDesign::Mirrored×1, App::Link×1, PartDesign::Pocket×1
note: 23 computed .brp shape members not serialized (recipe doc carries the construction recipe); baked Part::Feature solids carry a one-line shape summary decoded from their .brp
EXTERNAL_REF file=Resources.FCStd obj=Spreadsheet

FEATURE [Sketcher::SketchObject] Sketch
  FullyConstrained = true
  MapMode = 5
  Support = -> [XY_Plane001]
  expr: Constraints[10] = <<Dimensions>>.handle_height * 0.75
  expr: Constraints[13] = <<Dimensions>>.handle_inner_width / 2
  expr: Constraints[7] = <<Dimensions>>.handle_height
  expr: Constraints[9] = <<Dimensions>>.handle_outer_width / 2
  sketch-geometry (5):
    g0: ArcOfCircle CenterX=-21.0417 CenterY=7.5 CenterZ=0 NormalX=0 NormalY=0 NormalZ=1 AngleXU=0 Radius=17.7083 StartAngle=5.84585 EndAngle=6.72052
    g1: ArcOfCircle CenterX=0 CenterY=15 CenterZ=0 NormalX=0 NormalY=0 NormalZ=1 AngleXU=0 Radius=5 StartAngle=1.5708 EndAngle=3.14159
    g2: LineSegment StartX=-5 StartY=8.35e-14 StartZ=0 EndX=0 EndY=0 EndZ=0
    g3: LineSegment StartX=0 StartY=0 StartZ=0 EndX=3e-16 EndY=20 EndZ=0
    g4: GeomPoint X=-3.33333 Y=7.5 Z=0
  constraints (15):
    c: Coincident(g1,g0)
    c: PointOnObject(g0,g-1)
    c: PointOnObject(g1,g-2)
    c: Coincident(g2,g0)
    c: Coincident(g2,g-1)
    c: Coincident(g3,g2)
    c: Coincident(g3,g1)
    c: DistanceY(g3,g3) = 20
    c: Vertical(g0,g0)
    c: DistanceX(g2,g2) = 5
    c: DistanceY(g0) = 15
    c: PointOnObject(g4,g0)
    c: Horizontal(g0,g4)
    c: DistanceX(g4,g2) = 3.33333
    c: PointOnObject(g1,g3)
FEATURE [PartDesign::Pad] Pad
  Direction = (0,0,1)
  Length = 100
  Length2 = 10
  Midplane = true
  Profile = -> Sketch
  ReferenceAxis = -> Sketch [N_Axis]
  Type = 0
  expr: Length = <<Dimensions>>.handle_length
FEATURE [PartDesign::Mirrored] Mirrored
  BaseFeature = -> Pad
  MirrorPlane = -> Sketch [V_Axis]
  Originals = -> [Pad]
  Refine = true
FEATURE [Sketcher::SketchObject] Sketch001
  FullyConstrained = true
  MapMode = 5
  Placement = pos=(0,0,0) rot=(1,0,0;1.5708rad)
  Support = -> [XZ_Plane001]
  expr: Constraints[2] = <<Dimensions>>.handle_connector_screw_diameter
  expr: Constraints[4] = <<Dimensions>>.handle_length - <<Dimensions>>.handle_outer_width
  sketch-geometry (2):
    g0: Circle CenterX=0 CenterY=45 CenterZ=0 NormalX=0 NormalY=0 NormalZ=1 AngleXU=0 Radius=1.5
    g1: Circle CenterX=0 CenterY=-45 CenterZ=0 NormalX=0 NormalY=0 NormalZ=1 AngleXU=0 Radius=1.5
  constraints (5):
    c: PointOnObject(g0,g-2)
    c: Equal(g0,g1)
    c: Diameter(g0) = 3
    c: Symmetric(g0,g1,g-1)
    c: Distance(g0,g1) = 90
FEATURE [PartDesign::Hole] Hole
  BaseFeature = -> Mirrored
  CustomThreadClearance = 0
  Depth = 10
  DepthType = 0
  Diameter = 3.4
  DrillForDepth = false
  DrillPoint = 1
  DrillPointAngle = 118
  HoleCutCountersinkAngle = 90
  HoleCutCustomValues = false
  HoleCutDepth = 0
  HoleCutDiameter = 6.1
  HoleCutType = 0
  ModelThread = false
  Profile = -> Sketch001
  Tapered = false
  TaperedAngle = 90
  ThreadClass = 0
  ThreadDepth = 10
  ThreadDepthType = 0
  ThreadDirection = 0
  ThreadFit = 0
  ThreadSize = 9
  ThreadType = 1
  Threaded = false
  UseCustomThreadClearance = false
  expr: Depth = <<Dimensions>>.handle_screw_hole_depth
  expr: ThreadSize = <<Dimensions>>.handle_screw_type
FEATURE [App::Link] Link  label="Dimensions"
  LinkedObject = -> <external Resources.FCStd>#Spreadsheet
FEATURE [PartDesign::CoordinateSystem] LCS_Origin
  AttacherType = Attacher::AttachEngine3D
  MapMode = 2
  Support = -> [X_Axis001]
FEATURE [PartDesign::Body] Body  label="Base"
  Group = -> [LCS_Origin,Sketch,Pad,Mirrored,Sketch001,Hole]
  Origin = -> Origin001
  Tip = -> Hole
FEATURE [PartDesign::FeatureBase] Clone
  BaseFeature = -> Body
FEATURE [PartDesign::SubShapeBinder] Binder
  BindCopyOnChange = 0
  BindMode = 0
  ClaimChildren = false
  Context = -> Body001 [Binder.]
  Fuse = false
  MakeFace = true
  OffsetFill = false
  OffsetIntersection = false
  OffsetJoinType = 0
  OffsetOpenResult = false
  PartialLoad = false
  Relative = true
  Support = -> [Body[Hole.Sketch001.]]
  _Version = 2
FEATURE [Sketcher::SketchObject] Sketch002
  AttachmentOffset = pos=(0,0,-4) rot=(0,0,1;0rad)
  ExternalGeometry = -> [Binder]
  FullyConstrained = true
  MapMode = 5
  Placement = pos=(0,4,9e-16) rot=(1,0,0;1.5708rad)
  Support = -> [XZ_Plane]
  expr: Constraints[38] = <<Dimensions>>.handle_nut_S + 2 * <<Dimensions>>.clearance_tight_fit
  sketch-geometry (14):
    g0: LineSegment StartX=0 StartY=48.4064 StartZ=0 EndX=-2.95 EndY=46.7032 EndZ=0
    g1: LineSegment StartX=-2.95 StartY=46.7032 StartZ=0 EndX=-2.95 EndY=43.2968 EndZ=0
    g2: LineSegment StartX=-2.95 StartY=43.2968 StartZ=0 EndX=4.6976e-12 EndY=41.5936 EndZ=0
    g3: LineSegment StartX=4.6976e-12 StartY=41.5936 StartZ=0 EndX=2.95 EndY=43.2968 EndZ=0
    g4: LineSegment StartX=2.95 StartY=43.2968 StartZ=0 EndX=2.95 EndY=46.7032 EndZ=0
    g5: LineSegment StartX=2.95 StartY=46.7032 StartZ=0 EndX=0 EndY=48.4064 EndZ=0
    g6: Circle CenterX=0 CenterY=45 CenterZ=0 NormalX=0 NormalY=0 NormalZ=1 AngleXU=0 Radius=3.40637
    g7: LineSegment StartX=-1.7164e-12 StartY=-48.4064 StartZ=0 EndX=2.95 EndY=-46.7032 EndZ=0
    g8: LineSegment StartX=2.95 StartY=-46.7032 StartZ=0 EndX=2.95 EndY=-43.2968 EndZ=0
    g9: LineSegment StartX=2.95 StartY=-43.2968 StartZ=0 EndX=0 EndY=-41.5936 EndZ=0
    g10: LineSegment StartX=0 StartY=-41.5936 StartZ=0 EndX=-2.95 EndY=-43.2968 EndZ=0
    g11: LineSegment StartX=-2.95 StartY=-43.2968 StartZ=0 EndX=-2.95 EndY=-46.7032 EndZ=0
    g12: LineSegment StartX=-2.95 StartY=-46.7032 StartZ=0 EndX=-1.7164e-12 EndY=-48.4064 EndZ=0
    g13: Circle CenterX=0 CenterY=-45 CenterZ=0 NormalX=0 NormalY=0 NormalZ=1 AngleXU=0 Radius=3.40637
  constraints (32):
    c: Coincident(g0,g1)
    c: Coincident(g1,g2)
    c: Coincident(g2,g3)
    c: Coincident(g3,g4)
    c: Coincident(g4,g5)
    c: Coincident(g5,g0)
    c: Equal(g0, g1-g5) x5
    c: PointOnObject(g0,g6)
    c: PointOnObject(g1,g6)
    c: PointOnObject(g2,g6)
    c: PointOnObject(g3,g6)
    c: PointOnObject(g4,g6)
    c: PointOnObject(g5,g6)
    c: Coincident(g6,g-3)
    c: PointOnObject(g5,g-2)
    c: Coincident(g7,g8)
    c: Coincident(g8,g9)
    c: Coincident(g9,g10)
    c: Coincident(g10,g11)
    c: Coincident(g11,g12)
    c: Coincident(g12,g7)
    c: Equal(g7, g8-g12) x5
    c: PointOnObject(g7,g13)
    c: PointOnObject(g8,g13)
    c: PointOnObject(g9,g13)
    c: PointOnObject(g10,g13)
    c: PointOnObject(g11,g13)
    c: PointOnObject(g12,g13)
    c: Coincident(g13,g-4)
    c: PointOnObject(g9,g-2)
    c: DistanceX(g10,g8) = 5.9
    c: Equal(g8,g4)
FEATURE [PartDesign::Pocket] Pocket
  BaseFeature = -> Clone
  Direction = (0,1,2e-16)
  Length = 2.8
  Length2 = 5
  Profile = -> Sketch002
  ReferenceAxis = -> Sketch002 [N_Axis]
  Type = 0
  expr: Length = <<Dimensions>>.handle_nut_M + 2 * <<Dimensions>>.clearance_tight_fit
FEATURE [PartDesign::Body] Body001  label="Handle_EmbeddedNut"
  Group = -> [Clone,Sketch002,Binder,Pocket]
  Origin = -> Origin
  Tip = -> Pocket
FEATURE [PartDesign::CoordinateSystem] Local_CS  label="LCS_Origin001"
  AttacherType = Attacher::AttachEngine3D
  MapMode = 2
  Support = -> [X_Axis002]
FEATURE [PartDesign::FeatureBase] BaseFeature
  BaseFeature = -> Body
FEATURE [PartDesign::SubShapeBinder] Binder001
  BindCopyOnChange = 0
  BindMode = 0
  ClaimChildren = false
  Context = -> Body003 [Binder001.]
  Fuse = false
  MakeFace = true
  OffsetFill = false
  OffsetIntersection = false
  OffsetJoinType = 0
  OffsetOpenResult = false
  PartialLoad = false
  Relative = true
  Support = -> [Body[Hole.Sketch001.]]
  _Version = 2
FEATURE [PartDesign::Hole] Hole001
  BaseFeature = -> BaseFeature
  CustomThreadClearance = 0
  Depth = 4
  DepthType = 0
  Diameter = 3.9
  DrillForDepth = false
  DrillPoint = 1
  DrillPointAngle = 118
  HoleCutCountersinkAngle = 90
  HoleCutCustomValues = false
  HoleCutDepth = 0
  HoleCutDiameter = 6.1
  HoleCutType = 0
  ModelThread = false
  Profile = -> Binder001
  Reversed = true
  Tapered = false
  TaperedAngle = 90
  ThreadClass = 0
  ThreadDepth = 4
  ThreadDepthType = 0
  ThreadDirection = 0
  ThreadFit = 0
  ThreadSize = 0
  ThreadType = 0
  Threaded = false
  UseCustomThreadClearance = false
  expr: Depth = <<Dimensions>>.handle_ti_L
  expr: Diameter = <<Dimensions>>.handle_ti_D
FEATURE [PartDesign::Body] Body003  label="Handle_ThreadedInsert"
  BaseFeature = -> Body
  Group = -> [BaseFeature,Binder001,Hole001]
  Origin = -> Origin003
  Tip = -> Hole001
FEATURE [PartDesign::FeatureBase] BaseFeature001
  BaseFeature = -> Body003
FEATURE [PartDesign::Body] Body002  label="Handle"
  BaseFeature = -> Body003
  Group = -> [BaseFeature001,Local_CS]
  Origin = -> Origin002
  Tip = -> BaseFeature001
---- part HorizonMirror.FCStd = doc fcstd_4bcd52251b00 ----
FCSTD DOCUMENT  (FreeCAD 1.0RUnknown)
Label: HorizonMirror
License: All rights reserved
LicenseURL: http://en.wikipedia.org/wiki/All_rights_reserved
objects: PartDesign::CoordinateSystem×9, Sketcher::SketchObject×8, PartDesign::SubShapeBinder×7, PartDesign::Plane×7, App::Link×6, PartDesign::Pocket×4, App::DocumentObjectGroup×3, App::Part×3, Part::Box×2, Part::FeaturePython×2, PartDesign::Pad×2, PartDesign::Hole×2, PartDesign::Draft×2, App::FeaturePython×1, Part::Cut×1, PartDesign::AdditiveLoft×1, PartDesign::Body×1
note: 78 computed .brp shape members not serialized (recipe doc carries the construction recipe); baked Part::Feature solids carry a one-line shape summary decoded from their .brp
EXTERNAL_REF file=Sextant.FCStd obj=Assembly
EXTERNAL_REF file=Resources.FCStd obj=Spreadsheet
EXTERNAL_REF file=Parts.FCStd obj=LCS_Attachment
EXTERNAL_REF file=Parts.FCStd obj=Part
EXTERNAL_REF file=Parts.FCStd obj=LCS_Screw

FEATURE [PartDesign::CoordinateSystem] LCS_Origin
  AttacherType = Attacher::AttachEngine3D
  AttachmentSupport = -> [X_Axis]
  MapMode = 2
FEATURE [App::DocumentObjectGroup] Constraints
FEATURE [App::FeaturePython] Variables  # WARN: FeaturePython — macro-defined, semantics opaque (R4)
  Type = App::PropertyContainer
FEATURE [App::DocumentObjectGroup] Configurations
FEATURE [PartDesign::CoordinateSystem] LCS_Connector
  AttacherType = Attacher::AttachEngine3D
  AttachmentSupport = -> [X_Axis003]
  MapMode = 2
FEATURE [PartDesign::CoordinateSystem] LCS_Origin001
  AttacherType = Attacher::AttachEngine3D
  AttachmentOffset = pos=(20,0,0) rot=(0,0,1;0rad)
  AttachmentSupport = -> [X_Axis001]
  MapMode = 2
  Placement = pos=(20,0,0) rot=(0,0,1;0rad)
  expr: .AttachmentOffset.Base.x = <<Dimensions>>.horizon_mirror_mirror_width / 2
FEATURE [App::Link] Base  label="Base001"
  AttachedBy = #LCS_Connector
  AttachedTo = Parent Assembly#LCS_Origin
  LinkedObject = -> Part001
  SolverId = Asm4EE
  expr: Placement = LCS_Origin.Placement * AttachmentOffset * LCS_Connector.Placement ^ -1
FEATURE [App::Link] Mirror  label="Mirror001"
  AttachedBy = #LCS_Origin001
  AttachedTo = Base#LCS_Mirror
  LinkPlacement = pos=(0,-20,5) rot=(0.57735,0.57735,0.57735;2.0944rad)
  LinkedObject = -> Part
  Placement = pos=(0,-20,5) rot=(0.57735,0.57735,0.57735;2.0944rad)
  SolverId = Asm4EE
  expr: Placement = Base.Placement * LCS_Mirror.Placement * AttachmentOffset * LCS_Origin001.Placement ^ -1
FEATURE [Part::Box] Box  label="Cube"
  AttacherType = Attacher::AttachEngine3D
  Height = 0.1
  Length = 40
  Width = 25
  expr: Length = <<Dimensions>>.horizon_mirror_mirror_width
  expr: Width = <<Dimensions>>.horizon_mirror_mirror_height / 2
FEATURE [Part::Box] Box001  label="Cube001"
  AttacherType = Attacher::AttachEngine3D
  Height = 3
  Length = 40
  Width = 50
  expr: Height = <<Dimensions>>.horizon_mirror_mirror_thickness
  expr: Length = <<Dimensions>>.horizon_mirror_mirror_width
  expr: Width = <<Dimensions>>.horizon_mirror_mirror_height
FEATURE [PartDesign::SubShapeBinder] Binder
  BindCopyOnChange = 0
  BindMode = 0
  ClaimChildren = false
  Context = -> <external Sextant.FCStd>#Assembly [HorizonMirror.Mirror.Binder.]
  Fuse = false
  MakeFace = true
  OffsetFill = false
  OffsetIntersection = false
  OffsetJoinType = 0
  OffsetOpenResult = false
  PartialLoad = false
  Relative = true
  Support = -> [Box]
  _Version = 2
FEATURE [Part::Cut] Cut
  Base = -> Box001
  Tool = -> Binder
FEATURE [App::Part] Part  label="Mirror"
  Group = -> [LCS_Origin001,Box,Box001,Binder,Cut]
  Origin = -> Origin001
FEATURE [App::Link] Link  label="Dimensions"
  LinkedObject = -> <external Resources.FCStd>#Spreadsheet
FEATURE [PartDesign::Plane] DatumPlane  label="Plane_BaseBottom"
  AttachmentSupport = -> [XY_Plane004]
  Length = 60
  MapMode = 5
  ResizeMode = 0
  Width = 60
FEATURE [PartDesign::Plane] DatumPlane001  label="Plane_BaseTop"
  AttachmentOffset = pos=(0,0,1) rot=(0,0,1;0rad)
  AttachmentSupport = -> [DatumPlane]
  Length = 60
  MapMode = 5
  Placement = pos=(0,0,1) rot=(0,0,1;0rad)
  ResizeMode = 0
  Width = 60
  expr: .AttachmentOffset.Base.z = <<Dimensions>>.horizon_mirror_base_thickness
FEATURE [Sketcher::SketchObject] Sketch
  ArcFitTolerance = 0
  AttachmentSupport = -> [DatumPlane001]
  FullyConstrained = true
  MakeInternals = false
  MapMode = 5
  Placement = pos=(0,0,1) rot=(0,0,1;0rad)
  expr: Constraints[0] = <<Dimensions>>.horizon_mirror_screw_diameter
  expr: Constraints[5] = <<Dimensions>>.horizon_mirror_countersink_diameter * 0.5 + <<Dimensions>>.horizon_mirror_base_width + <<Dimensions>>.horizon_mirror_mirror_thickness * 0.5
  sketch-geometry (2):
    g0: Circle CenterX=-7.86 CenterY=0 CenterZ=0 NormalX=0 NormalY=0 NormalZ=1 AngleXU=0 Radius=1.5
    g1: Circle CenterX=7.86 CenterY=0 CenterZ=0 NormalX=0 NormalY=0 NormalZ=1 AngleXU=0 Radius=1.5
  constraints (6):
    c: Diameter(g0) = 3
    c: Equal(g0,g1)
    c: PointOnObject(g0,g-1)
    c: Symmetric(g0,g1,g-1)
    c: Distance(g0,g1) = 15.72  'hole_distance'
    c: Distance(g-1,g0) = 7.86
FEATURE [PartDesign::CoordinateSystem] LCS_Screw1
  AttacherType = Attacher::AttachEngine3D
  AttachmentSupport = -> [Sketch]
  MapMode = 11
  Placement = pos=(-7.86,0,1) rot=(0,0,1;1.5708rad)
FEATURE [PartDesign::CoordinateSystem] LCS_Screw2
  AttacherType = Attacher::AttachEngine3D
  AttachmentSupport = -> [Sketch]
  MapMode = 11
  Placement = pos=(7.86,0,1) rot=(0,0,1;1.5708rad)
FEATURE [PartDesign::Plane] DatumPlane002  label="Plane_MirrorBack"
  AttachmentSupport = -> [YZ_Plane004]
  Length = 60
  MapMode = 2
  Placement = pos=(0,0,0) rot=(0.57735,0.57735,0.57735;2.0944rad)
  ResizeMode = 0
  Width = 60
FEATURE [PartDesign::CoordinateSystem] LCS_Mirror
  AttacherType = Attacher::AttachEngine3D
  AttachmentOffset = pos=(0,5,0) rot=(0,0,1;0rad)
  AttachmentSupport = -> [DatumPlane002]
  MapMode = 5
  Placement = pos=(0,0,5) rot=(0.57735,0.57735,0.57735;2.0944rad)
  expr: .AttachmentOffset.Base.y = <<Dimensions>>.view_center_offset_hor - <<Dimensions>>.horizon_mirror_mirror_height / 2
FEATURE [PartDesign::Plane] DatumPlane003  label="Plane_FrameFront"
  AttachmentOffset = pos=(0,0,3) rot=(0,0,1;0rad)
  AttachmentSupport = -> [DatumPlane002]
  Length = 60
  MapMode = 5
  Placement = pos=(3,0,0) rot=(0.57735,0.57735,0.57735;2.0944rad)
  ResizeMode = 0
  Width = 60
  expr: .AttachmentOffset.Base.z = <<Dimensions>>.horizon_mirror_mirror_thickness
FEATURE [PartDesign::Plane] DatumPlane004  label="Plane_FrameBack"
  AttachmentOffset = pos=(0,0,-7) rot=(0,0,1;0rad)
  AttachmentSupport = -> [DatumPlane003]
  Length = 60
  MapMode = 5
  Placement = pos=(-4,0,0) rot=(0.57735,0.57735,0.57735;2.0944rad)
  ResizeMode = 0
  Width = 60
  expr: .AttachmentOffset.Base.z = -<<Dimensions>>.mirror_frame_thickness
FEATURE [Sketcher::SketchObject] Sketch001  label="Sketch_Base"
  ArcFitTolerance = 0
  AttachmentSupport = -> [DatumPlane]
  ExternalGeometry = -> [Sketch,DatumPlane004,DatumPlane003]
  FullyConstrained = true
  MakeInternals = false
  MapMode = 5
  expr: Constraints[10] = <<Dimensions>>.horizon_mirror_mirror_width + 2 * <<Dimensions>>.mirror_frame_width
  expr: Constraints[15] = <<Dimensions>>.horizon_mirror_countersink_diameter / 2 + <<Dimensions>>.horizon_mirror_base_width
  expr: Constraints[19] = <<Dimensions>>.horizon_mirror_countersink_diameter / 2 + <<Dimensions>>.horizon_mirror_base_width
  sketch-geometry (11):
    g0: LineSegment StartX=14.22 StartY=11.78 StartZ=0 EndX=14.22 EndY=-11.78 EndZ=0
    g1: GeomPoint [constr] X=-4 Y=23 Z=0
    g2: LineSegment StartX=-4 StartY=-23 StartZ=0 EndX=3 EndY=-23 EndZ=0
    g3: LineSegment StartX=-4 StartY=23 StartZ=0 EndX=3 EndY=23 EndZ=0
    g4: ArcOfCircle CenterX=3 CenterY=-11.78 CenterZ=0 NormalX=0 NormalY=0 NormalZ=1 AngleXU=0 Radius=11.22 StartAngle=4.71239 EndAngle=6.28319
    g5: ArcOfCircle CenterX=3 CenterY=11.78 CenterZ=0 NormalX=0 NormalY=0 NormalZ=1 AngleXU=0 Radius=11.22 StartAngle=0 EndAngle=1.5708
    g6: LineSegment StartX=-14.22 StartY=12.78 StartZ=0 EndX=-14.22 EndY=-12.78 EndZ=0
    g7: ArcOfCircle CenterX=-4 CenterY=12.78 CenterZ=0 NormalX=0 NormalY=0 NormalZ=1 AngleXU=0 Radius=10.22 StartAngle=1.5708 EndAngle=3.14159
    g8: ArcOfCircle CenterX=-4 CenterY=-12.78 CenterZ=0 NormalX=0 NormalY=0 NormalZ=1 AngleXU=0 Radius=10.22 StartAngle=3.14159 EndAngle=4.71239
    g9: LineSegment StartX=3 StartY=23 StartZ=0 EndX=3 EndY=-23 EndZ=0
    g10: LineSegment StartX=-4 StartY=23 StartZ=0 EndX=-4 EndY=-23 EndZ=0
  constraints (24):
    c: Horizontal(g2)
    c: Coincident(g3,g1)
    c: PointOnObject(g3,g-5)
    c: PointOnObject(g2,g-5)
    c: Tangent(g0,g4) = 1.5708
    c: Tangent(g2,g4) = -1.5708
    c: Tangent(g0,g5) = 1.5708
    c: Tangent(g3,g5) = 1.5708
    c: Vertical(g0)
    c: Equal(g5,g4)
    c: DistanceY(g2,g3) = 46
    c: PointOnObject(g2,g-6)
    c: Vertical(g6)
    c: Tangent(g6,g7) = -1.5708
    c: Tangent(g6,g8) = -1.5708
    c: DistanceX(g6,g-3) = 6.36
    c: Symmetric(g3,g2,g-1)
    c: Tangent(g7,g3) = 1.5708
    c: Tangent(g8,g2) = -1.5708
    c: DistanceX(g-4,g0) = 6.36
    c: Coincident(g9,g3)
    c: Coincident(g9,g2)
    c: Coincident(g10,g3)
    c: Coincident(g10,g2)
FEATURE [PartDesign::SubShapeBinder] Binder001  label="Binder_AdjustmentScrew"
  BindCopyOnChange = 0
  BindMode = 0
  ClaimChildren = false
  Context = -> Part001 [Body001.Hole001.Binder001.]
  Fuse = false
  MakeFace = true
  OffsetFill = false
  OffsetIntersection = false
  OffsetJoinType = 0
  OffsetOpenResult = false
  PartialLoad = false
  Relative = true
  Support = -> [Sketch006]
  _Version = 2
FEATURE [App::Link] MirrorClip
  AttachedBy = #LCS_Attachment
  AttachedTo = Base#LCS_Clip1
  AttachmentOffset = pos=(0,0,0) rot=(0,0,1;4.71239rad)
  LinkPlacement = pos=(-4,17.5,51) rot=(-0.57735,-0.57735,-0.57735;4.18879rad)
  LinkedObject = -> <external Parts.FCStd>#Part
  Placement = pos=(-4,17.5,51) rot=(-0.57735,-0.57735,-0.57735;4.18879rad)
  SolverId = Asm4EE
  expr: Placement = Base.Placement * LCS_Clip1.Placement * AttachmentOffset * Parts#LCS_Attachment.Placement ^ -1
FEATURE [App::Link] MirrorClip001
  AttachedBy = #LCS_Attachment
  AttachedTo = Base#LCS_Clip2
  AttachmentOffset = pos=(0,0,0) rot=(0,0,1;1.5708rad)
  LinkPlacement = pos=(-4,-17.5,51) rot=(0.57735,-0.57735,0.57735;4.18879rad)
  LinkedObject = -> <external Parts.FCStd>#Part
  Placement = pos=(-4,-17.5,51) rot=(0.57735,-0.57735,0.57735;4.18879rad)
  SolverId = Asm4EE
  expr: Placement = Base.Placement * LCS_Clip2.Placement * AttachmentOffset * Parts#LCS_Attachment.Placement ^ -1
FEATURE [App::Link] MirrorClip002
  AttachedBy = #LCS_Attachment
  AttachedTo = Base#LCS_Clip3
  AttachmentOffset = pos=(0,0,0) rot=(0,0,1;1.5708rad)
  LinkPlacement = pos=(-4,-17.5,9) rot=(0.57735,-0.57735,0.57735;4.18879rad)
  LinkedObject = -> <external Parts.FCStd>#Part
  Placement = pos=(-4,-17.5,9) rot=(0.57735,-0.57735,0.57735;4.18879rad)
  SolverId = Asm4EE
  expr: Placement = Base.Placement * LCS_Clip3.Placement * AttachmentOffset * Parts#LCS_Attachment.Placement ^ -1
FEATURE [Part::FeaturePython] Screw  label="M3x4-Screw"  # WARN: FeaturePython — macro-defined, semantics opaque (R4)
  AttachedBy = Origin
  AttachedTo = MirrorClip#LCS_Screw
  AttachmentOffset = pos=(0,0,0) rot=(0,-1,0;3.14159rad)
  Diameter = 6
  Invert = false
  LeftHanded = false
  Length = 2
  LengthCustom = 4
  MatchOuter = false
  OffsetAngle = 0
  Placement = pos=(-6,17.5,51) rot=(-0.57735,0.57735,0.57735;4.18879rad)
  SolverId = Asm4EE
  Thread = false
  Type = 69
  expr: Placement = MirrorClip.Placement * Parts#LCS_Screw.Placement * AttachmentOffset
FEATURE [Part::FeaturePython] Screw001  label="M2x4-Screw"  # WARN: FeaturePython — macro-defined, semantics opaque (R4)
  AttachedBy = Origin
  AttachedTo = MirrorClip002#LCS_Screw
  AttachmentOffset = pos=(0,0,0) rot=(0,1,0;3.14159rad)
  Diameter = 4
  Invert = false
  LeftHanded = false
  Length = 2
  LengthCustom = 4
  MatchOuter = false
  OffsetAngle = 0
  Placement = pos=(-6,-17.5,9) rot=(-0.57735,-0.57735,0.57735;2.0944rad)
  SolverId = Asm4EE
  Thread = false
  Type = 69
  expr: Placement = MirrorClip002.Placement * Parts#LCS_Screw.Placement * AttachmentOffset
FEATURE [App::Part] Assembly
  AssemblyType = Part::Link
  Group = -> [LCS_Origin,Constraints,Variables,Configurations,Base,Mirror,LCS_Screw1,LCS_Screw2,MirrorClip,MirrorClip001,MirrorClip002,Screw,Screw001]
  Origin = -> Origin
  Type = Assembly
FEATURE [PartDesign::Plane] DatumPlane006  label="Plane_Top"
  AttachmentOffset = pos=(0,0,58) rot=(0,0,1;0rad)
  AttachmentSupport = -> [XY_Plane004]
  Length = 60
  MapMode = 5
  Placement = pos=(0,0,58) rot=(0,0,1;0rad)
  ResizeMode = 0
  Width = 60
  expr: .AttachmentOffset.Base.z = <<Dimensions>>.horizon_mirror_mirror_offset + <<Dimensions>>.horizon_mirror_mirror_height + <<Dimensions>>.mirror_frame_width
FEATURE [Sketcher::SketchObject] Sketch010  label="Sketch_ScrewAccess"
  ArcFitTolerance = 0
  AttachmentSupport = -> [DatumPlane001]
  ExternalGeometry = -> [Sketch]
  FullyConstrained = true
  MakeInternals = false
  MapMode = 5
  Placement = pos=(0,0,1) rot=(0,0,1;0rad)
  expr: Constraints[5] = <<Dimensions>>.horizon_mirror_countersink_diameter / 2 + <<Dimensions>>.clearance_loose_fit
  sketch-geometry (4):
    g0: LineSegment StartX=-26.6253 StartY=10.6717 StartZ=0 EndX=-6.62531 EndY=3.39229 EndZ=0
    g1: ArcOfCircle CenterX=-7.86 CenterY=0 CenterZ=0 NormalX=0 NormalY=0 NormalZ=1 AngleXU=0 Radius=3.61 StartAngle=5.06145 EndAngle=7.50492
    g2: LineSegment StartX=-6.62531 StartY=-3.39229 StartZ=0 EndX=-26.6253 EndY=-10.6717 EndZ=0
    g3: LineSegment StartX=-26.6253 StartY=-10.6717 StartZ=0 EndX=-26.6253 EndY=10.6717 EndZ=0
  constraints (9):
    c: Tangent(g0,g1) = 1.5708
    c: Tangent(g1,g2) = 1.5708
    c: Coincident(g2,g3)
    c: Coincident(g3,g0)
    c: Coincident(g1,g-3)
    c: Radius(g1) = 3.61
    c: DistanceX(g0,g0) = 20
    c: Symmetric(g2,g0,g-1)
    c: Angle(g0,g2) = 0.698132
FEATURE [PartDesign::SubShapeBinder] Binder005  label="Binder_BaseFront"
  BindCopyOnChange = 0
  BindMode = 0
  ClaimChildren = false
  Context = -> <external Sextant.FCStd>#Assembly [HorizonMirror.Base.Body001.Binder005.]
  Fuse = false
  MakeFace = true
  OffsetFill = false
  OffsetIntersection = false
  OffsetJoinType = 0
  OffsetOpenResult = false
  PartialLoad = false
  Relative = true
  Support = -> [Sketch001[Edge3,Edge2,Edge1,Edge9]]
  _Version = 2
FEATURE [PartDesign::Plane] DatumPlane007  label="Plane_ViewCenter"
  AttachmentOffset = pos=(0,0,30) rot=(0,0,1;0rad)
  AttachmentSupport = -> [XY_Plane004]
  Length = 60
  MapMode = 5
  Placement = pos=(0,0,30) rot=(0,0,1;0rad)
  ResizeMode = 0
  Width = 60
  expr: .AttachmentOffset.Base.z = <<Dimensions>>.view_center_offset_hor
FEATURE [Sketcher::SketchObject] Sketch009  label="Sketch_LoftTop"
  ArcFitTolerance = 0
  AttachmentSupport = -> [DatumPlane007]
  ExternalGeometry = -> [DatumPlane004,DatumPlane003]
  FullyConstrained = true
  MakeInternals = false
  MapMode = 5
  Placement = pos=(0,0,30) rot=(0,0,1;0rad)
  expr: Constraints[2] = <<Dimensions>>.horizon_mirror_mirror_width + 2 * <<Dimensions>>.mirror_frame_width
  sketch-geometry (4):
    g0: LineSegment StartX=-4 StartY=23 StartZ=0 EndX=-4 EndY=-23 EndZ=0
    g1: LineSegment StartX=-6 StartY=10 StartZ=0 EndX=-6 EndY=-10 EndZ=0
    g2: ArcOfCircle CenterX=37.25 CenterY=10 CenterZ=0 NormalX=0 NormalY=0 NormalZ=1 AngleXU=0 Radius=43.25 StartAngle=2.83629 EndAngle=3.14159
    g3: ArcOfCircle CenterX=37.25 CenterY=-10 CenterZ=0 NormalX=0 NormalY=0 NormalZ=1 AngleXU=0 Radius=43.25 StartAngle=3.14159 EndAngle=3.44689
  constraints (10):
    c: PointOnObject(g2,g-3)
    c: Symmetric(g2,g3,g-1)
    c: Distance(g0) = 46
    c: Symmetric(g1,g1,g-1)
    c: Tangent(g2,g1) = -1.5708
    c: Tangent(g3,g1) = -1.5708
    c: DistanceY(g1,g1) = 20
    c: DistanceX(g1,g3) = 2
    c: Coincident(g0,g3)
    c: Coincident(g2,g0)
FEATURE [PartDesign::SubShapeBinder] Binder006  label="Binder_FrameBase"
  BindCopyOnChange = 0
  BindMode = 0
  ClaimChildren = false
  Context = -> <external Sextant.FCStd>#Assembly [HorizonMirror.Base.Body001.Binder006.]
  Fuse = false
  MakeFace = true
  OffsetFill = false
  OffsetIntersection = false
  OffsetJoinType = 0
  OffsetOpenResult = false
  PartialLoad = false
  Relative = true
  Support = -> [Sketch001[Edge10,Edge8,Edge9,Edge4]]
  _Version = 2
FEATURE [PartDesign::Pad] Pad006  label="Pad_Frame"
  Direction = (0,0,1)
  Length = 10
  Length2 = 10
  Profile = -> Binder006 [Face1]
  Suppressed = false
  Type = 3
  UpToFace = -> DatumPlane006
FEATURE [PartDesign::Pad] Pad007  label="Pad_BaseFront"
  BaseFeature = -> Pad006
  Direction = (0,0,1)
  Length = 10
  Length2 = 10
  Profile = -> Binder005 [Face1]
  Suppressed = false
  Type = 3
  UpToFace = -> DatumPlane001
FEATURE [PartDesign::SubShapeBinder] Binder004  label="Binder_BaseBack"
  BindCopyOnChange = 0
  BindMode = 0
  ClaimChildren = false
  Context = -> Part001 [Body001.Binder004.]
  Fuse = false
  MakeFace = true
  OffsetFill = false
  OffsetIntersection = false
  OffsetJoinType = 0
  OffsetOpenResult = false
  PartialLoad = false
  Relative = true
  Support = -> [Sketch001[Edge7,Edge10,Edge6,Edge5]]
  _Version = 2
FEATURE [PartDesign::AdditiveLoft] AdditiveLoft  label="Loft_BackSupport"
  BaseFeature = -> Pad007
  Closed = false
  Profile = -> Binder004 [Face1]
  Ruled = false
  Sections = -> [Sketch009]
  Suppressed = false
FEATURE [PartDesign::Pocket] Pocket002  label="Pocket_ScrewAccess"
  BaseFeature = -> AdditiveLoft
  Direction = (0,0,-1)
  Length = 5
  Length2 = 5
  Profile = -> Sketch010
  ReferenceAxis = -> Sketch010 [N_Axis]
  Reversed = true
  Suppressed = false
  Type = 1
FEATURE [PartDesign::Hole] Hole  label="Hole_Attachment"
  BaseFeature = -> Pocket002
  CustomThreadClearance = 0
  Depth = 86.1294
  DepthType = 1
  Diameter = 3.4
  DrillForDepth = false
  DrillPoint = 1
  DrillPointAngle = 118
  HoleCutCountersinkAngle = 90
  HoleCutCustomValues = false
  HoleCutDepth = 0
  HoleCutDiameter = 6.72
  HoleCutType = 2
  ModelThread = false
  Profile = -> Sketch
  Suppressed = false
  Tapered = false
  TaperedAngle = 90
  ThreadClass = 0
  ThreadDepth = 86.1294
  ThreadDepthType = 0
  ThreadDirection = 0
  ThreadFit = 0
  ThreadSize = 9
  ThreadType = 1
  Threaded = false
  UseCustomThreadClearance = false
  expr: HoleCutDiameter = <<Dimensions>>.horizon_mirror_countersink_diameter
  expr: ThreadSize = <<Dimensions>>.horizon_mirror_screw_type
FEATURE [Sketcher::SketchObject] Sketch015  label="Sketch_Mirror"
  ArcFitTolerance = 0
  AttachmentSupport = -> [DatumPlane002]
  ExternalGeometry = -> [DatumPlane007]
  FullyConstrained = true
  MakeInternals = false
  MapMode = 5
  Placement = pos=(0,0,0) rot=(0.57735,0.57735,0.57735;2.0944rad)
  expr: Constraints[5] = <<Dimensions>>.horizon_mirror_mirror_offset
  expr: Constraints[8] = <<Dimensions>>.horizon_mirror_mirror_width
  expr: Constraints[9] = <<Dimensions>>.horizon_mirror_mirror_height
  sketch-geometry (7):
    g0: LineSegment StartX=-20 StartY=55 StartZ=0 EndX=20 EndY=55 EndZ=0
    g1: LineSegment StartX=20 StartY=5 StartZ=0 EndX=-20 EndY=5 EndZ=0
    g2: LineSegment StartX=-20 StartY=30 StartZ=0 EndX=20 EndY=30 EndZ=0
    g3: LineSegment StartX=-20 StartY=5 StartZ=0 EndX=-20 EndY=30 EndZ=0
    g4: LineSegment StartX=-20 StartY=30 StartZ=0 EndX=-20 EndY=55 EndZ=0
    g5: LineSegment StartX=20 StartY=55 StartZ=0 EndX=20 EndY=30 EndZ=0
    g6: LineSegment StartX=20 StartY=30 StartZ=0 EndX=20 EndY=5 EndZ=0
  constraints (19):
    c: Coincident(g0,g5)
    c: Coincident(g6,g1)
    c: Coincident(g1,g3)
    c: Coincident(g4,g0)
    c: Horizontal(g1)
    c: DistanceY(g-1,g6) = 5
    c: PointOnObject(g2,g-3)
    c: Symmetric(g0,g0,g-2)
    c: DistanceX(g0,g0) = 40
    c: DistanceY(g3,g4) = 50
    c: Coincident(g3,g4)
    c: Vertical(g3)
    c: Vertical(g4)
    c: Coincident(g5,g6)
    c: Vertical(g5)
    c: Vertical(g6)
    c: Coincident(g3,g2)
    c: Coincident(g5,g2)
    c: PointOnObject(g2,g-3)
FEATURE [Sketcher::SketchObject] Sketch006  label="Sketch_Clips"
  ArcFitTolerance = 0
  AttachmentSupport = -> [DatumPlane004]
  ExternalGeometry = -> [Sketch015]
  FullyConstrained = true
  MakeInternals = false
  MapMode = 5
  Placement = pos=(-4,0,0) rot=(0.57735,0.57735,0.57735;2.0944rad)
  expr: Constraints[0] = <<Dimensions>>.mirror_adjustment_screw_diameter
  expr: Constraints[22] = <<Dimensions>>.mirror_clip_edge_distance + <<Dimensions>>.mirror_clip_width / 2
  expr: Constraints[28] = <<Dimensions>>.mirror_clip_edge_distance
  sketch-geometry (10):
    g0: Circle CenterX=17.5 CenterY=51 CenterZ=0 NormalX=0 NormalY=0 NormalZ=1 AngleXU=0 Radius=1.5
    g1: Circle CenterX=-17.5 CenterY=9 CenterZ=0 NormalX=0 NormalY=0 NormalZ=1 AngleXU=0 Radius=1.5
    g2: Circle CenterX=-17.5 CenterY=51 CenterZ=0 NormalX=0 NormalY=0 NormalZ=1 AngleXU=0 Radius=1.5
    g3: LineSegment [constr] StartX=17.5 StartY=51 StartZ=0 EndX=17.5 EndY=55 EndZ=0
    g4: LineSegment [constr] StartX=17.5 StartY=51 StartZ=0 EndX=20 EndY=51 EndZ=0
    g5: LineSegment [constr] StartX=-17.5 StartY=51 StartZ=0 EndX=-20 EndY=51 EndZ=0
    g6: LineSegment [constr] StartX=-17.5 StartY=51 StartZ=0 EndX=-17.5 EndY=55 EndZ=0
    g7: LineSegment [constr] StartX=-17.5 StartY=9 StartZ=0 EndX=-17.5 EndY=5 EndZ=0
    g8: LineSegment [constr] StartX=-17.5 StartY=9 StartZ=0 EndX=-20 EndY=9 EndZ=0
    g9: GeomPoint [constr] X=19 Y=51 Z=0
  constraints (29):
    c: Diameter(g0) = 3
    c: Equal(g0,g1)
    c: Equal(g2,g0)
    c: Coincident(g3,g0)
    c: PointOnObject(g3,g-8)
    c: Vertical(g3)
    c: Coincident(g4,g0)
    c: Horizontal(g4)
    c: Coincident(g5,g2)
    c: PointOnObject(g5,g-3)
    c: Horizontal(g5)
    c: Coincident(g6,g2)
    c: PointOnObject(g6,g-8)
    c: Vertical(g6)
    c: Coincident(g7,g1)
    c: PointOnObject(g7,g-5)
    c: Coincident(g8,g1)
    c: PointOnObject(g8,g-4)
    c: Horizontal(g8)
    c: Vertical(g7)
    c: Equal(g7,g3)
    c: Equal(g3,g6)
    c: DistanceY(g6,g6) = 4
    c: Equal(g4,g5)
    c: Equal(g5,g8)
    c: PointOnObject(g4,g-7)
    c: PointOnObject(g9,g4)
    c: PointOnObject(g9,g0)
    c: Distance(g9,g4) = 1
FEATURE [PartDesign::CoordinateSystem] LCS_Clip1
  AttacherType = Attacher::AttachEngine3D
  AttachmentSupport = -> [Sketch006]
  MapMode = 11
  Placement = pos=(-4,17.5,51) rot=(0.707107,0,0.707107;3.14159rad)
FEATURE [PartDesign::CoordinateSystem] LCS_Clip2
  AttacherType = Attacher::AttachEngine3D
  AttachmentSupport = -> [Sketch006]
  MapMode = 11
  Placement = pos=(-4,-17.5,51) rot=(0.707107,0,0.707107;3.14159rad)
FEATURE [PartDesign::CoordinateSystem] LCS_Clip3
  AttacherType = Attacher::AttachEngine3D
  AttachmentSupport = -> [Sketch006]
  MapMode = 11
  Placement = pos=(-4,-17.5,9) rot=(0.707107,0,0.707107;3.14159rad)
FEATURE [Sketcher::SketchObject] Sketch011
  ArcFitTolerance = 0
  AttachmentSupport = -> [DatumPlane004]
  ExternalGeometry = -> [Sketch006]
  FullyConstrained = true
  MakeInternals = false
  MapMode = 5
  Placement = pos=(-4,0,0) rot=(0.57735,0.57735,0.57735;2.0944rad)
  expr: Constraints[12] = <<Dimensions>>.mirror_clip_width + 2 * <<Dimensions>>.clearance_loose_fit
  expr: Constraints[13] = <<Dimensions>>.mirror_clip_width / 2 + <<Dimensions>>.clearance_loose_fit
  sketch-geometry (6):
    g0: LineSegment StartX=-44.25 StartY=12.25 StartZ=0 EndX=-14.25 EndY=12.25 EndZ=0
    g1: LineSegment StartX=-14.25 StartY=12.25 StartZ=0 EndX=-14.25 EndY=5.75 EndZ=0
    g2: LineSegment StartX=-14.25 StartY=5.75 StartZ=0 EndX=-44.25 EndY=5.75 EndZ=0
    g3: LineSegment StartX=-44.25 StartY=5.75 StartZ=0 EndX=-44.25 EndY=12.25 EndZ=0
    g4: GeomPoint [constr] X=-14.25 Y=9 Z=0
    g5: LineSegment [constr] StartX=-17.5 StartY=9 StartZ=0 EndX=-14.25 EndY=9 EndZ=0
  constraints (15):
    c: Coincident(g2,g3)
    c: Coincident(g0,g3)
    c: Coincident(g1,g2)
    c: Coincident(g0,g1)
    c: Coincident(g5,g-3)
    c: Coincident(g5,g4)
    c: Symmetric(g1,g0,g4)
    c: Horizontal(g5)
    c: Vertical(g1)
    c: Horizontal(g0)
    c: Horizontal(g2)
    c: Vertical(g3)
    c: DistanceY(g1,g1) = 6.5
    c: DistanceX(g5,g5) = 3.25
    c: DistanceX(g2,g2) = 30
FEATURE [PartDesign::SubShapeBinder] Binder007  label="Binder_Mirror"
  BindCopyOnChange = 0
  BindMode = 0
  ClaimChildren = false
  Context = -> Part001 [Body001.Binder007.]
  Fuse = false
  MakeFace = true
  OffsetFill = false
  OffsetIntersection = false
  OffsetJoinType = 0
  OffsetOpenResult = false
  PartialLoad = false
  Relative = true
  Support = -> [Sketch015[Edge7,Edge1,Edge2,Edge4,Edge5,Edge6]]
  _Version = 2
FEATURE [PartDesign::Pocket] Pocket  label="Pocket_Mirror"
  BaseFeature = -> Hole
  Direction = (-1,0,0)
  Length = 5
  Length2 = 5
  Profile = -> Binder007
  Reversed = true
  Suppressed = false
  Type = 1
FEATURE [PartDesign::Draft] Draft
  Angle = 10
  Base = -> Pocket [Face21,Face27,Face22,Face25]
  BaseFeature = -> Pocket
  NeutralPlane = -> DatumPlane002
  SupportTransform = false
  Suppressed = false
FEATURE [PartDesign::SubShapeBinder] Binder008  label="Binder_MirrorOnlyGlass"
  BindCopyOnChange = 0
  BindMode = 0
  ClaimChildren = false
  Context = -> <external Sextant.FCStd>#Assembly [HorizonMirror.Base.Body001.Binder008.]
  Fuse = false
  MakeFace = true
  OffsetFill = false
  OffsetIntersection = false
  OffsetJoinType = 0
  OffsetOpenResult = false
  PartialLoad = false
  Relative = true
  Support = -> [Sketch015[Edge7,Edge1,Edge3,Edge2]]
  _Version = 2
FEATURE [Sketcher::SketchObject] Sketch003  label="Sketch_Window"
  ArcFitTolerance = 0
  AttachmentSupport = -> [DatumPlane002]
  ExternalGeometry = -> [Sketch006,Binder008]
  FullyConstrained = true
  MakeInternals = false
  MapMode = 5
  Placement = pos=(0,0,0) rot=(0.57735,0.57735,0.57735;2.0944rad)
  expr: Constraints[13] = <<Dimensions>>.horizon_mirror_frame_lip_width
  expr: Constraints[14] = <<Dimensions>>.horizon_mirror_frame_lip_width
  expr: Constraints[15] = <<Dimensions>>.horizon_mirror_frame_lip_width
  sketch-geometry (11):
    g0: LineSegment StartX=-19 StartY=30 StartZ=0 EndX=-19 EndY=47 EndZ=0
    g1: LineSegment StartX=-13.5 StartY=54 StartZ=0 EndX=13.5 EndY=54 EndZ=0
    g2: LineSegment StartX=19 StartY=47 StartZ=0 EndX=19 EndY=30 EndZ=0
    g3: GeomPoint [constr] X=19 Y=54 Z=0
    g4: ArcOfCircle CenterX=-17.5 CenterY=51 CenterZ=0 NormalX=0 NormalY=0 NormalZ=1 AngleXU=0 Radius=4 StartAngle=4.71239 EndAngle=6.28319
    g5: ArcOfCircle CenterX=17.5 CenterY=51 CenterZ=0 NormalX=0 NormalY=0 NormalZ=1 AngleXU=0 Radius=4 StartAngle=3.14159 EndAngle=4.71239
    g6: LineSegment StartX=-19 StartY=30 StartZ=0 EndX=19 EndY=30 EndZ=0
    g7: LineSegment StartX=-13.5 StartY=51 StartZ=0 EndX=-13.5 EndY=54 EndZ=0
    g8: LineSegment StartX=13.5 StartY=51 StartZ=0 EndX=13.5 EndY=54 EndZ=0
    g9: LineSegment StartX=-17.5 StartY=47 StartZ=0 EndX=-19 EndY=47 EndZ=0
    g10: LineSegment StartX=17.5 StartY=47 StartZ=0 EndX=19 EndY=47 EndZ=0
  constraints (28):
    c: Coincident(g4,g-3)
    c: Coincident(g5,g-4)
    c: Vertical(g0)
    c: Horizontal(g1)
    c: Vertical(g2)
    c: Vertical(g3,g2)
    c: Horizontal(g1,g3)
    c: Equal(g5,g4)
    c: Radius(g4) = 4
    c: PointOnObject(g0,g-6)
    c: PointOnObject(g2,g-6)
    c: Coincident(g6,g0)
    c: Coincident(g6,g2)
    c: DistanceX(g2,g-8) = 1
    c: DistanceX(g-6,g0) = 1
    c: DistanceY(g1,g-7) = 1
    c: Vertical(g7)
    c: Coincident(g7,g1)
    c: Tangent(g7,g4) = -1.5708
    c: Vertical(g8)
    c: Coincident(g1,g8)
    c: Tangent(g8,g5) = 1.5708
    c: Horizontal(g9)
    c: Coincident(g0,g9)
    c: Tangent(g9,g4) = 1.5708
    c: Horizontal(g10)
    c: Coincident(g2,g10)
    c: Tangent(g10,g5) = -1.5708
FEATURE [PartDesign::Pocket] Pocket004  label="Pocket_Window"
  BaseFeature = -> Draft
  Direction = (-1,0,0)
  Length = 5
  Length2 = 5
  Profile = -> Sketch003
  ReferenceAxis = -> Sketch003 [N_Axis]
  Suppressed = false
  Type = 1
FEATURE [PartDesign::Pocket] Pocket003
  BaseFeature = -> Pocket004
  Direction = (-1,0,0)
  Length = 5
  Length2 = 5
  Profile = -> Sketch011
  ReferenceAxis = -> Sketch011 [N_Axis]
  Refine = true
  Suppressed = false
  Type = 1
FEATURE [PartDesign::Draft] Draft001
  Angle = 45
  Base = -> Pocket003 [Face25]
  BaseFeature = -> Pocket003
  NeutralPlane = -> DatumPlane004
  Reversed = true
  SupportTransform = false
  Suppressed = false
FEATURE [PartDesign::Hole] Hole001  label="Holes_AdjustmentScrew"
  BaseFeature = -> Draft001
  CustomThreadClearance = 0
  Depth = 160.19
  DepthType = 1
  Diameter = 3.4
  DrillForDepth = false
  DrillPoint = 1
  DrillPointAngle = 118
  HoleCutCountersinkAngle = 90
  HoleCutCustomValues = false
  HoleCutDepth = 4
  HoleCutDiameter = 3.9
  HoleCutType = 1
  ModelThread = false
  Profile = -> Binder001
  Reversed = true
  Suppressed = false
  Tapered = false
  TaperedAngle = 90
  ThreadClass = 0
  ThreadDepth = 160.19
  ThreadDepthType = 0
  ThreadDirection = 0
  ThreadFit = 0
  ThreadSize = 9
  ThreadType = 1
  Threaded = false
  UseCustomThreadClearance = false
  expr: HoleCutDepth = <<Dimensions>>.mirror_adjustment_ti_L
  expr: HoleCutDiameter = <<Dimensions>>.mirror_adjustment_ti_D
  expr: ThreadSize = <<Dimensions>>.mirror_adjustment_screw_type
FEATURE [PartDesign::Body] Body001  label="HorizonMirrorFrameBody"
  AllowCompound = false
  Group = -> [DatumPlane,DatumPlane001,DatumPlane007,DatumPlane002,DatumPlane003,DatumPlane004,DatumPlane006,Sketch001,Binder006,Pad006,Binder005,Sketch,Sketch009,Sketch010,Pad007,Binder004,AdditiveLoft,Pocket002,Hole,Sketch015,Sketch006,Binder007,Pocket,Draft,Binder008,Sketch003,Binder001,Sketch011,Pocket004,Pocket003,Draft001,Hole001]
  Origin = -> Origin004
  Tip = -> Hole001
FEATURE [App::Part] Part001  label="HorizonMirrorFrame"
  Group = -> [Body001,LCS_Connector]
  Origin = -> Origin003
FEATURE [App::DocumentObjectGroup] Parts
  Group = -> [Part,Part001]
---- part IndexArm.FCStd = doc fcstd_9cedaf97cd92 ----
FCSTD DOCUMENT  (FreeCAD 1.0RUnknown)
Label: IndexArm
License: All rights reserved
LicenseURL: http://en.wikipedia.org/wiki/All_rights_reserved
objects: PartDesign::CoordinateSystem×10, Part::FeaturePython×10, Sketcher::SketchObject×6, App::Link×5, PartDesign::Plane×4, App::DocumentObjectGroup×3, PartDesign::Pad×2, PartDesign::Pocket×2, PartDesign::SubShapeBinder×1, App::FeaturePython×1, App::Part×1, PartDesign::Draft×1, PartDesign::Hole×1, PartDesign::Body×1
note: 56 computed .brp shape members not serialized (recipe doc carries the construction recipe); baked Part::Feature solids carry a one-line shape summary decoded from their .brp
EXTERNAL_REF file=Resources.FCStd obj=Spreadsheet
EXTERNAL_REF file=Scale.FCStd obj=Body
EXTERNAL_REF file=IndexMirror.FCStd obj=LCS_Origin
EXTERNAL_REF file=Shaft.FCStd obj=DatumPlane
EXTERNAL_REF file=IndexMirror.FCStd obj=Assembly
EXTERNAL_REF file=Scale.FCStd obj=LCS_Origin
EXTERNAL_REF file=Scale.FCStd obj=Part
EXTERNAL_REF file=Shaft.FCStd obj=DatumPlane001
EXTERNAL_REF file=Shaft.FCStd obj=Body
EXTERNAL_REF file=Shaft.FCStd obj=DatumPlane002
EXTERNAL_REF file=Shaft.FCStd obj=DatumPlane003

FEATURE [App::Link] Link  label="Dimensions"
  LinkedObject = -> <external Resources.FCStd>#Spreadsheet
FEATURE [PartDesign::SubShapeBinder] Binder
  BindCopyOnChange = 0
  BindMode = 0
  ClaimChildren = false
  Context = -> Body001 [Hole.Binder.]
  Fuse = false
  MakeFace = true
  OffsetFill = false
  OffsetIntersection = false
  OffsetJoinType = 0
  OffsetOpenResult = false
  PartialLoad = false
  Placement = pos=(0,0,2) rot=(0,0,1;0rad)
  Relative = true
  Support = -> [<external Scale.FCStd>#Body[Hole001.Sketch005.]]
  _Version = 2
  expr: .Placement.Base.z = <<Dimensions>>.index_arm_thickness
FEATURE [PartDesign::CoordinateSystem] Local_CS  label="LCS_ShaftBottom"
  AttacherType = Attacher::AttachEngine3D
  AttachmentSupport = -> [X_Axis004]
  MapMode = 2
FEATURE [PartDesign::CoordinateSystem] Local_CS001  label="LCS_ShaftTop"
  AttacherType = Attacher::AttachEngine3D
  AttachmentOffset = pos=(0,0,2) rot=(0,0,1;0rad)
  AttachmentSupport = -> [X_Axis004]
  MapMode = 2
  Placement = pos=(0,0,2) rot=(0,0,1;0rad)
  expr: .AttachmentOffset.Base.z = <<Dimensions>>.index_arm_thickness
FEATURE [PartDesign::CoordinateSystem] LCS_Origin
  AttacherType = Attacher::AttachEngine3D
  AttachmentSupport = -> [X_Axis]
  MapMode = 2
FEATURE [App::DocumentObjectGroup] Constraints
FEATURE [App::FeaturePython] Variables  # WARN: FeaturePython — macro-defined, semantics opaque (R4)
  Type = App::PropertyContainer
FEATURE [App::DocumentObjectGroup] Configurations
FEATURE [App::Link] IndexMirror
  AttachedBy = #LCS_Origin
  AttachedTo = Shaft#DatumPlane
  LinkPlacement = pos=(0,0,3) rot=(0,0,-1;0.1309rad)
  LinkedObject = -> <external IndexMirror.FCStd>#Assembly
  Placement = pos=(0,0,3) rot=(0,0,-1;0.1309rad)
  SolverId = Asm4EE
  expr: Placement = Shaft.Placement * Shaft#DatumPlane.Placement * AttachmentOffset * IndexMirror#LCS_Origin.Placement ^ -1
FEATURE [App::Link] IndexArm  label="IndexArm001"
  AttachedBy = #Local_CS
  AttachedTo = Parent Assembly#LCS_Origin
  LinkedObject = -> Body001
  SolverId = Asm4EE
  expr: Placement = LCS_Origin.Placement * AttachmentOffset * Local_CS.Placement ^ -1
FEATURE [Part::FeaturePython] Screw  label="M3x8-Screw"  # WARN: FeaturePython — macro-defined, semantics opaque (R4)
  AttachedBy = Origin
  AttachedTo = IndexArm#Local_CS003
  AttachmentOffset = pos=(0,0,0) rot=(0,1,0;3.14159rad)
  Diameter = 3
  Invert = false
  LeftHanded = false
  Length = 0
  LengthCustom = 8
  MatchOuter = false
  OffsetAngle = 0
  Placement = pos=(-6.8883,16.6298,0) rot=(-0.707107,0.707107,0;3.14159rad)
  SolverId = Asm4EE
  Thread = false
  Type = 50
  expr: Placement = IndexArm.Placement * Local_CS003.Placement * AttachmentOffset
FEATURE [Part::FeaturePython] Screw001  label="M3x8-Screw655"  # WARN: FeaturePython — macro-defined, semantics opaque (R4)
  AttachedBy = Origin
  AttachedTo = IndexArm#Local_CS004
  AttachmentOffset = pos=(0,0,0) rot=(0,1,0;3.14159rad)
  Diameter = 3
  Invert = false
  LeftHanded = false
  Length = 0
  LengthCustom = 8
  MatchOuter = false
  OffsetAngle = 0
  Placement = pos=(17.846,-2.34947,0) rot=(-0.707107,0.707107,0;3.14159rad)
  SolverId = Asm4EE
  Thread = false
  Type = 50
  expr: Placement = IndexArm.Placement * Local_CS004.Placement * AttachmentOffset
FEATURE [Part::FeaturePython] Screw002  label="M3x8-Screw656"  # WARN: FeaturePython — macro-defined, semantics opaque (R4)
  AttachedBy = Origin
  AttachedTo = IndexArm#Local_CS005
  AttachmentOffset = pos=(0,0,0) rot=(0,1,0;3.14159rad)
  Diameter = 3
  Invert = false
  LeftHanded = false
  Length = 0
  LengthCustom = 8
  MatchOuter = false
  OffsetAngle = 0
  Placement = pos=(-10.9577,-14.2804,0) rot=(-0.707107,0.707107,0;3.14159rad)
  SolverId = Asm4EE
  Thread = false
  Type = 50
  expr: Placement = IndexArm.Placement * Local_CS005.Placement * AttachmentOffset
FEATURE [Part::FeaturePython] Nut  label="M3-Nut1361"  # WARN: FeaturePython — macro-defined, semantics opaque (R4)
  AttachedBy = Origin
  AttachedTo = IndexArm#Local_CS003
  AttachmentOffset = pos=(0,0,4) rot=(0,0,1;0rad)
  Diameter = 4
  Invert = false
  LeftHanded = false
  MatchOuter = false
  OffsetAngle = 0
  Placement = pos=(-6.8883,16.6298,4) rot=(0,0,1;1.5708rad)
  SolverId = Asm4EE
  Thread = false
  Type = 31
  expr: .AttachmentOffset.Base.z = <<Dimensions>>.index_arm_thickness + <<Dimensions>>.index_mirror_base_thickness + <<Dimensions>>.shaft_base_thickness
  expr: Placement = IndexArm.Placement * Local_CS003.Placement * AttachmentOffset
FEATURE [Part::FeaturePython] Nut001  label="M3-Nut"  # WARN: FeaturePython — macro-defined, semantics opaque (R4)
  AttachedBy = Origin
  AttachedTo = IndexArm#Local_CS004
  AttachmentOffset = pos=(0,0,4) rot=(0,0,1;0rad)
  Diameter = 4
  Invert = false
  LeftHanded = false
  MatchOuter = false
  OffsetAngle = 0
  Placement = pos=(17.846,-2.34947,4) rot=(0,0,1;1.5708rad)
  SolverId = Asm4EE
  Thread = false
  Type = 31
  expr: .AttachmentOffset.Base.z = <<Dimensions>>.index_arm_thickness + <<Dimensions>>.index_mirror_base_thickness + <<Dimensions>>.shaft_base_thickness
  expr: Placement = IndexArm.Placement * Local_CS004.Placement * AttachmentOffset
FEATURE [Part::FeaturePython] Nut002  label="M3-Nut1362"  # WARN: FeaturePython — macro-defined, semantics opaque (R4)
  AttachedBy = Origin
  AttachedTo = IndexArm#Local_CS005
  AttachmentOffset = pos=(0,0,4) rot=(0,0,1;0rad)
  Diameter = 4
  Invert = false
  LeftHanded = false
  MatchOuter = false
  OffsetAngle = 0
  Placement = pos=(-10.9577,-14.2804,4) rot=(0,0,1;1.5708rad)
  SolverId = Asm4EE
  Thread = false
  Type = 31
  expr: .AttachmentOffset.Base.z = <<Dimensions>>.index_arm_thickness + <<Dimensions>>.index_mirror_base_thickness + <<Dimensions>>.shaft_base_thickness
  expr: Placement = IndexArm.Placement * Local_CS005.Placement * AttachmentOffset
FEATURE [Part::FeaturePython] Screw004  label="M3x10-Screw001"  # WARN: FeaturePython — macro-defined, semantics opaque (R4)
  AttachedBy = Origin
  AttachedTo = IndexArm#Local_CS007
  Diameter = 4
  Invert = false
  LeftHanded = false
  Length = 3
  LengthCustom = 10
  MatchOuter = false
  OffsetAngle = 0
  Placement = pos=(-19.1818,-184.003,2) rot=(0,0,1;0rad)
  SolverId = Asm4EE
  Thread = false
  Type = 74
  expr: Placement = IndexArm.Placement * Local_CS007.Placement * AttachmentOffset
FEATURE [Part::FeaturePython] Screw005  label="M3x10-Screw"  # WARN: FeaturePython — macro-defined, semantics opaque (R4)
  AttachedBy = Origin
  AttachedTo = IndexArm#Local_CS008
  Diameter = 4
  Invert = false
  LeftHanded = false
  Length = 3
  LengthCustom = 10
  MatchOuter = false
  OffsetAngle = 0
  Placement = pos=(19.1818,-184.003,2) rot=(0,0,1;0rad)
  SolverId = Asm4EE
  Thread = false
  Type = 74
  expr: Placement = IndexArm.Placement * Local_CS008.Placement * AttachmentOffset
FEATURE [Part::FeaturePython] Nut004  label="M3-Nut1363"  # WARN: FeaturePython — macro-defined, semantics opaque (R4)
  AttachedBy = Origin
  AttachedTo = IndexArm#Local_CS007
  AttachmentOffset = pos=(0,0,-4) rot=(0,1,0;3.14159rad)
  Diameter = 4
  Invert = false
  LeftHanded = false
  MatchOuter = false
  OffsetAngle = 0
  Placement = pos=(-19.1818,-184.003,-2) rot=(0,1,0;3.14159rad)
  SolverId = Asm4EE
  Thread = false
  Type = 31
  expr: .AttachmentOffset.Base.z = -<<Dimensions>>.index_arm_thickness - <<Dimensions>>.scale_thickness
  expr: Placement = IndexArm.Placement * Local_CS007.Placement * AttachmentOffset
FEATURE [Part::FeaturePython] Nut005  label="M3-Nut1364"  # WARN: FeaturePython — macro-defined, semantics opaque (R4)
  AttachedBy = Origin
  AttachedTo = IndexArm#Local_CS008
  AttachmentOffset = pos=(0,0,-4) rot=(0,1,0;3.14159rad)
  Diameter = 4
  Invert = false
  LeftHanded = false
  MatchOuter = false
  OffsetAngle = 0
  Placement = pos=(19.1818,-184.003,-2) rot=(0,1,0;3.14159rad)
  SolverId = Asm4EE
  Thread = false
  Type = 31
  expr: .AttachmentOffset.Base.z = -<<Dimensions>>.index_arm_thickness - <<Dimensions>>.scale_thickness
  expr: Placement = IndexArm.Placement * Local_CS008.Placement * AttachmentOffset
FEATURE [App::Link] VernierScale
  AttachedBy = #LCS_Origin
  AttachedTo = IndexArm#Local_CS
  LinkPlacement = pos=(0,0,-2) rot=(0,0,1;0rad)
  LinkedObject = -> <external Scale.FCStd>#Part
  Placement = pos=(0,0,-2) rot=(0,0,1;0rad)
  SolverId = Asm4EE
  expr: Placement = IndexArm.Placement * Local_CS.Placement * AttachmentOffset * Scale#LCS_Origin.Placement ^ -1
FEATURE [PartDesign::CoordinateSystem] LCS_IndexMirrorAttachment
  AttacherType = Attacher::AttachEngine3D
  AttachmentOffset = pos=(0,0,0) rot=(0,0,-1;0.1309rad)
  AttachmentSupport = -> [Local_CS001]
  MapMode = 2
  Placement = pos=(0,0,2) rot=(0,0,-1;0.1309rad)
  expr: .AttachmentOffset.Rotation.Yaw = <<Dimensions>>.horizon_mirror_angle - 30 °
FEATURE [App::Link] Shaft
  AttachedBy = #DatumPlane001
  AttachedTo = IndexArm#LCS_IndexMirrorAttachment
  LinkPlacement = pos=(0,0,3) rot=(0,0,-1;0.1309rad)
  LinkedObject = -> <external Shaft.FCStd>#Body
  Placement = pos=(0,0,3) rot=(0,0,-1;0.1309rad)
  SolverId = Asm4EE
  expr: Placement = IndexArm.Placement * LCS_IndexMirrorAttachment.Placement * AttachmentOffset * Shaft#DatumPlane001.Placement ^ -1
FEATURE [PartDesign::Plane] Shaft_Plane_Spacer
  AttachedBy = Origin
  Length = 67.3183
  Placement = pos=(0,0,-4) rot=(0,0,-1;0.1309rad)
  ResizeMode = 0
  SolverId = Asm4EE
  Width = 67.3183
  expr: Placement = Shaft.Placement * Shaft#DatumPlane002.Placement
FEATURE [PartDesign::CoordinateSystem] LCS_1  label="LCS_Attachment"
  AttacherType = Attacher::AttachEngine3D
  AttachmentOffset = pos=(0,0,0) rot=(0,0,-1;0.392699rad)
  AttachmentSupport = -> [Shaft_Plane_Spacer]
  MapMode = 5
  Placement = pos=(0,0,-4) rot=(0,0,-1;0.523599rad)
  expr: .AttachmentOffset.Rotation.Angle = <<Dimensions>>.horizon_mirror_angle
FEATURE [PartDesign::Plane] Shaft_Plane_ShaftEnd
  AttachedBy = Origin
  Length = 67.3183
  Placement = pos=(0,0,-10) rot=(0,0,-1;0.1309rad)
  ResizeMode = 0
  SolverId = Asm4EE
  Width = 67.3183
  expr: Placement = Shaft.Placement * Shaft#DatumPlane003.Placement
FEATURE [App::Part] Assembly
  AssemblyType = Part::Link
  Group = -> [LCS_Origin,Constraints,Variables,Configurations,IndexMirror,IndexArm,Screw,Screw001,Screw002,Nut,Nut001,Nut002,Screw004,Screw005,Nut004,Nut005,VernierScale,LCS_1,Shaft,Shaft_Plane_Spacer,Shaft_Plane_ShaftEnd]
  Origin = -> Origin
  Type = Assembly
FEATURE [PartDesign::Plane] DatumPlane  label="Plane_Bottom"
  AttachmentSupport = -> [XY_Plane004]
  Length = 60
  MapMode = 5
  ResizeMode = 0
  Width = 60
FEATURE [Sketcher::SketchObject] Sketch
  ArcFitTolerance = 0
  AttachmentSupport = -> [DatumPlane]
  FullyConstrained = true
  MakeInternals = false
  MapMode = 5
  expr: Constraints[0] = <<Dimensions>>.index_mirror_screw_center_distance
  expr: Constraints[14] = <<Dimensions>>.horizon_mirror_angle
  expr: Constraints[3] = <<Dimensions>>.index_mirror_screw_diameter
  sketch-geometry (6):
    g0: Circle CenterX=-6.8883 CenterY=16.6298 CenterZ=0 NormalX=0 NormalY=0 NormalZ=1 AngleXU=0 Radius=1.5
    g1: LineSegment [constr] StartX=-6.8883 StartY=16.6298 StartZ=0 EndX=0 EndY=0 EndZ=0
    g2: Circle CenterX=17.846 CenterY=-2.34947 CenterZ=0 NormalX=0 NormalY=0 NormalZ=1 AngleXU=0 Radius=1.5
    g3: Circle CenterX=-10.9577 CenterY=-14.2804 CenterZ=0 NormalX=0 NormalY=0 NormalZ=1 AngleXU=0 Radius=1.5
    g4: LineSegment [constr] StartX=0 StartY=0 StartZ=0 EndX=17.846 EndY=-2.34947 EndZ=0
    g5: LineSegment [constr] StartX=0 StartY=0 StartZ=0 EndX=-10.9577 EndY=-14.2804 EndZ=0
  constraints (15):
    c: Distance(g-1,g0) = 18
    c: Coincident(g1,g0)
    c: Coincident(g1,g-1)
    c: Diameter(g0) = 3
    c: Equal(g0,g3)
    c: Equal(g0,g2)
    c: Coincident(g4,g1)
    c: Coincident(g4,g2)
    c: Coincident(g5,g1)
    c: Coincident(g5,g3)
    c: Equal(g5,g1)
    c: Equal(g4,g1)
    c: Angle(g1,g5) = 2.0944
    c: Angle(g5,g4) = 2.0944
    c: Angle(g-2,g1) = 0.392699
FEATURE [PartDesign::CoordinateSystem] Local_CS003  label="LCS_BoltIndexmirror1"
  AttacherType = Attacher::AttachEngine3D
  AttachmentSupport = -> [Sketch]
  MapMode = 11
  Placement = pos=(-6.8883,16.6298,0) rot=(0,0,1;1.5708rad)
FEATURE [PartDesign::CoordinateSystem] Local_CS004  label="LCS_BoltIndexmirror2"
  AttacherType = Attacher::AttachEngine3D
  AttachmentSupport = -> [Sketch]
  MapMode = 11
  Placement = pos=(17.846,-2.34947,0) rot=(0,0,1;1.5708rad)
FEATURE [PartDesign::CoordinateSystem] Local_CS005  label="LCS_BoltIndexmirror3"
  AttacherType = Attacher::AttachEngine3D
  AttachmentSupport = -> [Sketch]
  MapMode = 11
  Placement = pos=(-10.9577,-14.2804,0) rot=(0,0,1;1.5708rad)
FEATURE [PartDesign::Plane] DatumPlane001  label="Plane_Top"
  AttachmentOffset = pos=(0,0,2) rot=(0,0,1;0rad)
  AttachmentSupport = -> [DatumPlane]
  Length = 60
  MapMode = 5
  Placement = pos=(0,0,2) rot=(0,0,1;0rad)
  ResizeMode = 0
  Width = 60
  expr: .AttachmentOffset.Base.z = <<Dimensions>>.index_arm_thickness
FEATURE [Sketcher::SketchObject] Sketch001
  ArcFitTolerance = 0
  AttachmentSupport = -> [DatumPlane001]
  FullyConstrained = true
  MakeInternals = false
  MapMode = 5
  Placement = pos=(0,0,2) rot=(0,0,1;0rad)
  expr: Constraints[13] = <<Dimensions>>.scale_outer_radius
  expr: Constraints[4] = <<Dimensions>>.index_arm_window_width
  expr: Constraints[5] = <<Dimensions>>.index_arm_window_height
  sketch-geometry (10):
    g0: ArcOfCircle CenterX=-1.8e-15 CenterY=0 CenterZ=0 NormalX=0 NormalY=0 NormalZ=1 AngleXU=0 Radius=190.029 StartAngle=4.63583 EndAngle=4.78895
    g1: ArcOfCircle CenterX=-1.8e-15 CenterY=0 CenterZ=0 NormalX=0 NormalY=0 NormalZ=1 AngleXU=0 Radius=169.971 StartAngle=4.63583 EndAngle=4.78895
    g2: LineSegment StartX=-13 StartY=-169.473 StartZ=0 EndX=-14.5342 EndY=-189.473 EndZ=0
    g3: LineSegment StartX=13 StartY=-169.473 StartZ=0 EndX=14.5342 EndY=-189.473 EndZ=0
    g4: GeomPoint [constr] X=0 Y=-169.473 Z=0
    g5: GeomPoint [constr] X=0 Y=-190.029 Z=0
    g6: GeomPoint [constr] X=0 Y=-169.971 Z=0
    g7: GeomPoint [constr] X=0 Y=-180 Z=0
    g8: LineSegment [constr] StartX=-1.8e-15 StartY=0 StartZ=0 EndX=-13 EndY=-169.473 EndZ=0
    g9: LineSegment [constr] StartX=13 StartY=-169.473 StartZ=0 EndX=-1.8e-15 EndY=0 EndZ=0
  constraints (22):
    c: Coincident(g2,g1)
    c: Coincident(g2,g0)
    c: Coincident(g3,g1)
    c: Coincident(g3,g0)
    c: DistanceX(g1,g1) = 26
    c: DistanceY(g2,g2) = 20
    c: PointOnObject(g4,g-2)
    c: Symmetric(g1,g1,g4)
    c: PointOnObject(g5,g0)
    c: PointOnObject(g5,g-2)
    c: PointOnObject(g6,g1)
    c: PointOnObject(g6,g-2)
    c: Symmetric(g5,g6,g7)
    c: Distance(g7,g0) = 180
    c: Coincident(g0,g-1)
    c: Coincident(g1,g0)
    c: Coincident(g8,g0)
    c: Coincident(g8,g1)
    c: Parallel(g8,g2)
    c: Coincident(g9,g1)
    c: Coincident(g9,g0)
    c: Parallel(g9,g3)
FEATURE [Sketcher::SketchObject] Sketch003
  ArcFitTolerance = 0
  AttachmentSupport = -> [DatumPlane]
  ExternalGeometry = -> [Sketch001]
  FullyConstrained = true
  MakeInternals = false
  MapMode = 5
  expr: Constraints[23] = <<Dimensions>>.index_mirror_base_diameter / 2
  expr: Constraints[3] = <<Dimensions>>.index_arm_width
  expr: Constraints[4] = 5 mm
  expr: Constraints[6] = <<Dimensions>>.bearing_da + 2 * <<Dimensions>>.clearance_loose_fit
  sketch-geometry (20):
    g0: LineSegment StartX=-7.5 StartY=-26.9768 StartZ=0 EndX=-7.5 EndY=-164.8 EndZ=0
    g1: LineSegment StartX=7.5 StartY=-26.9768 StartZ=0 EndX=7.5 EndY=-164.8 EndZ=0
    g2: GeomPoint [constr] X=0 Y=-190.029 Z=0
    g3: GeomPoint [constr] X=0 Y=-195.029 Z=0
    g4: Circle CenterX=0 CenterY=0 CenterZ=0 NormalX=0 NormalY=0 NormalZ=1 AngleXU=0 Radius=5.25
    g5: ArcOfCircle CenterX=-13.7671 CenterY=-179.473 CenterZ=0 NormalX=0 NormalY=0 NormalZ=1 AngleXU=0 Radius=15.0294 StartAngle=1.49424 EndAngle=4.63583
    g6: ArcOfCircle CenterX=13.7671 CenterY=-179.473 CenterZ=0 NormalX=0 NormalY=0 NormalZ=1 AngleXU=0 Radius=15.0294 StartAngle=4.78895 EndAngle=7.93054
    g7: ArcOfCircle CenterX=0 CenterY=0 CenterZ=0 NormalX=0 NormalY=0 NormalZ=1 AngleXU=0 Radius=164.971 StartAngle=4.63583 EndAngle=4.66691
    g8: ArcOfCircle CenterX=0 CenterY=0 CenterZ=0 NormalX=0 NormalY=0 NormalZ=1 AngleXU=0 Radius=164.971 StartAngle=4.75787 EndAngle=4.78895
    g9: ArcOfCircle CenterX=0 CenterY=0 CenterZ=0 NormalX=0 NormalY=0 NormalZ=1 AngleXU=0 Radius=28 StartAngle=4.98356 EndAngle=10.7244
    g10: LineSegment [constr] StartX=-7.5 StartY=-26.9768 StartZ=0 EndX=0 EndY=-26.9768 EndZ=0
    g11: LineSegment [constr] StartX=0 StartY=-26.9768 StartZ=0 EndX=7.5 EndY=-26.9768 EndZ=0
    g12: ArcOfCircle CenterX=-3 CenterY=-213.029 CenterZ=0 NormalX=0 NormalY=0 NormalZ=1 AngleXU=0 Radius=2 StartAngle=2.61227 EndAngle=4.71239
    g13: LineSegment StartX=-3 StartY=-215.029 StartZ=0 EndX=3 EndY=-215.029 EndZ=0
    g14: ArcOfCircle CenterX=3 CenterY=-213.029 CenterZ=0 NormalX=0 NormalY=0 NormalZ=1 AngleXU=0 Radius=2 StartAngle=4.71239 EndAngle=6.8125
    g15: ArcOfCircle CenterX=22.5 CenterY=-201.622 CenterZ=0 NormalX=0 NormalY=0 NormalZ=1 AngleXU=0 Radius=20.5916 StartAngle=2.81452 EndAngle=3.67091
    g16: ArcOfCircle CenterX=-22.5 CenterY=-201.622 CenterZ=0 NormalX=0 NormalY=0 NormalZ=1 AngleXU=0 Radius=20.5916 StartAngle=5.75387 EndAngle=6.61026
    g17: ArcOfCircle CenterX=0 CenterY=0 CenterZ=0 NormalX=0 NormalY=0 NormalZ=1 AngleXU=0 Radius=195.029 StartAngle=4.63583 EndAngle=4.69701
    g18: ArcOfCircle [constr] CenterX=0 CenterY=0 CenterZ=0 NormalX=0 NormalY=0 NormalZ=1 AngleXU=0 Radius=195.029 StartAngle=4.69701 EndAngle=4.72777
    g19: ArcOfCircle CenterX=0 CenterY=0 CenterZ=0 NormalX=0 NormalY=0 NormalZ=1 AngleXU=0 Radius=195.029 StartAngle=4.72777 EndAngle=4.78895
  constraints (50):
    c: Vertical(g0)
    c: Vertical(g1)
    c: Equal(g0,g1)
    c: DistanceX(g0,g1) = 15
    c: Distance(g3,g2) = 5
    c: PointOnObject(g3,g-2)
    c: Diameter(g4) = 10.5
    c: Tangent(g6,g19) = -1.5708
    c: Tangent(g5,g17) = -1.5708
    c: Coincident(g7,g0)
    c: Tangent(g7,g5) = 1.5708
    c: Coincident(g8,g1)
    c: Tangent(g8,g6) = 1.5708
    c: Coincident(g9,g4)
    c: Coincident(g9,g0)
    c: Coincident(g1,g9)
    c: Coincident(g4,g-1)
    c: Coincident(g7,g4)
    c: Coincident(g10,g0)
    c: PointOnObject(g10,g-2)
    c: Horizontal(g10)
    c: Coincident(g11,g10)
    c: Coincident(g11,g1)
    c: Radius(g9) = 28
    c: Symmetric(g-4,g-5,g5)
    c: Coincident(g17,g4)
    c: Symmetric(g-6,g-6,g6)
    c: Coincident(g8,g17)
    c: PointOnObject(g2,g-5)
    c: PointOnObject(g2,g-2)
    c: Tangent(g12,g13) = -1.5708
    c: Tangent(g13,g14) = -1.5708
    c: Tangent(g14,g15) = 1.5708
    c: Coincident(g17,g18)
    c: Coincident(g17,g18)
    c: Coincident(g18,g19)
    c: Coincident(g18,g19)
    c: PointOnObject(g3,g18)
    c: Coincident(g17,g16)
    c: Coincident(g18,g15)
    c: Symmetric(g13,g12,g-2)
    c: Radius(g12) = 2
    c: Equal(g12,g14)
    c: DistanceY(g12,g3) = 20
    c: Vertical(g13,g15)
    c: Vertical(g12,g16)
    c: DistanceX(g13,g13) = 6
    c: Tangent(g16,g12) = 1.5708
    c: DistanceX(g16,g15) = 45
    c: Equal(g16,g15)
FEATURE [PartDesign::Pad] Pad
  Direction = (0,0,1)
  Length = 2
  Length2 = 10
  Profile = -> Sketch003
  ReferenceAxis = -> Sketch003 [N_Axis]
  Suppressed = false
  Type = 3
  UpToFace = -> DatumPlane001 [Plane]
  expr: Length = <<Dimensions>>.index_arm_thickness
FEATURE [Sketcher::SketchObject] Sketch004
  ArcFitTolerance = 0
  AttachmentSupport = -> [DatumPlane001]
  ExternalGeometry = -> [Sketch001]
  FullyConstrained = true
  MakeInternals = false
  MapMode = 5
  Placement = pos=(0,0,2) rot=(0,0,1;0rad)
  expr: Constraints[7] = <<Dimensions>>.index_mirror_base_diameter / 2 + 1 mm
  sketch-geometry (4):
    g0: LineSegment StartX=3 StartY=-28.8444 StartZ=0 EndX=3 EndY=-164.473 EndZ=0
    g1: LineSegment StartX=3 StartY=-164.473 StartZ=0 EndX=-3 EndY=-164.473 EndZ=0
    g2: LineSegment StartX=-3 StartY=-164.473 StartZ=0 EndX=-3 EndY=-28.8444 EndZ=0
    g3: ArcOfCircle CenterX=0 CenterY=0 CenterZ=0 NormalX=0 NormalY=0 NormalZ=1 AngleXU=0 Radius=29 StartAngle=4.60876 EndAngle=4.81602
  constraints (11):
    c: Coincident(g0,g1)
    c: Coincident(g1,g2)
    c: Vertical(g0)
    c: Vertical(g2)
    c: Coincident(g3,g-1)
    c: Coincident(g3,g2)
    c: Coincident(g3,g0)
    c: Radius(g3) = 29
    c: Symmetric(g1,g0,g-2)
    c: Distance(g1) = 6
    c: DistanceY(g-3,g1) = 5
FEATURE [PartDesign::Pad] Pad001
  BaseFeature = -> Pad
  Direction = (0,0,1)
  Length = 3
  Length2 = 10
  Profile = -> Sketch004
  ReferenceAxis = -> Sketch004 [N_Axis]
  Suppressed = false
  Type = 0
FEATURE [PartDesign::Draft] Draft
  Angle = 20
  Base = -> Pad001 [Face19,Face20,Face21]
  BaseFeature = -> Pad001
  NeutralPlane = -> DatumPlane001
  SupportTransform = false
  Suppressed = false
FEATURE [PartDesign::Pocket] Pocket  label="WindowPocket"
  BaseFeature = -> Draft
  Direction = (0,0,-1)
  Length = 5
  Length2 = 5
  Profile = -> Sketch001
  ReferenceAxis = -> Sketch001 [N_Axis]
  Suppressed = false
  Type = 1
FEATURE [PartDesign::Hole] Hole001  label="AttachmentHoles"
  BaseFeature = -> Pocket
  CustomThreadClearance = 0
  Depth = 478.321
  DepthType = 1
  Diameter = 3.4
  DrillForDepth = false
  DrillPoint = 1
  DrillPointAngle = 118
  HoleCutCountersinkAngle = 90
  HoleCutCustomValues = false
  HoleCutDepth = 0
  HoleCutDiameter = 6.72
  HoleCutType = 2
  ModelThread = false
  Profile = -> Sketch
  Reversed = true
  Suppressed = false
  Tapered = false
  TaperedAngle = 90
  ThreadClass = 0
  ThreadDepth = 478.321
  ThreadDepthType = 0
  ThreadDirection = 0
  ThreadFit = 0
  ThreadSize = 9
  ThreadType = 1
  Threaded = false
  UseCustomThreadClearance = false
  expr: HoleCutDiameter = <<Dimensions>>.index_mirror_countersink_diameter
  expr: ThreadSize = <<Dimensions>>.index_mirror_screw_type
FEATURE [Sketcher::SketchObject] Sketch005
  ArcFitTolerance = 0
  AttachmentSupport = -> [DatumPlane001]
  ExternalGeometry = -> [Binder]
  FullyConstrained = true
  MakeInternals = false
  MapMode = 5
  Placement = pos=(0,0,2) rot=(0,0,1;0rad)
  sketch-geometry (10):
    g0: ArcOfCircle CenterX=-19.1818 CenterY=-182.503 CenterZ=0 NormalX=0 NormalY=0 NormalZ=1 AngleXU=0 Radius=1.7 StartAngle=-4.4e-15 EndAngle=3.14159
    g1: ArcOfCircle CenterX=-19.1818 CenterY=-185.503 CenterZ=0 NormalX=0 NormalY=0 NormalZ=1 AngleXU=0 Radius=1.7 StartAngle=3.14159 EndAngle=6.28319
    g2: LineSegment StartX=-20.8818 StartY=-182.503 StartZ=0 EndX=-20.8818 EndY=-185.503 EndZ=0
    g3: LineSegment StartX=-17.4818 StartY=-185.503 StartZ=0 EndX=-17.4818 EndY=-182.503 EndZ=0
    g4: ArcOfCircle CenterX=19.1818 CenterY=-182.503 CenterZ=0 NormalX=0 NormalY=0 NormalZ=1 AngleXU=0 Radius=1.7 StartAngle=-9e-16 EndAngle=3.14159
    g5: ArcOfCircle CenterX=19.1818 CenterY=-185.503 CenterZ=0 NormalX=0 NormalY=0 NormalZ=1 AngleXU=0 Radius=1.7 StartAngle=3.14159 EndAngle=6.28319
    g6: LineSegment StartX=17.4818 StartY=-182.503 StartZ=0 EndX=17.4818 EndY=-185.503 EndZ=0
    g7: LineSegment StartX=20.8818 StartY=-185.503 StartZ=0 EndX=20.8818 EndY=-182.503 EndZ=0
    g8: GeomPoint X=-19.1818 Y=-184.003 Z=0
    g9: GeomPoint X=19.1818 Y=-184.003 Z=0
  constraints (20):
    c: Tangent(g0,g2) = -1.5708
    c: Tangent(g2,g1) = -1.5708
    c: Tangent(g1,g3) = -1.5708
    c: Tangent(g3,g0) = -1.5708
    c: Equal(g0,g1)
    c: Tangent(g4,g6) = -1.5708
    c: Tangent(g6,g5) = -1.5708
    c: Tangent(g5,g7) = -1.5708
    c: Tangent(g7,g4) = -1.5708
    c: Equal(g4,g5)
    c: Symmetric(g0,g1,g-3)
    c: Vertical(g3)
    c: Symmetric(g4,g5,g-4)
    c: Vertical(g7)
    c: Diameter(g0) = 3.4
    c: Equal(g0,g4)
    c: Equal(g6,g3)
    c: Distance(g2) = 3
    c: Coincident(g8,g-3)
    c: Coincident(g9,g-4)
FEATURE [PartDesign::CoordinateSystem] Local_CS007  label="LCS_BoltScale1"
  AttacherType = Attacher::AttachEngine3D
  AttachmentSupport = -> [Sketch005]
  MapMode = 1
  Placement = pos=(-19.1818,-184.003,2) rot=(0,0,1;0rad)
FEATURE [PartDesign::CoordinateSystem] Local_CS008  label="LCS_BoltScale2"
  AttacherType = Attacher::AttachEngine3D
  AttachmentSupport = -> [Sketch005]
  MapMode = 1
  Placement = pos=(19.1818,-184.003,2) rot=(0,0,1;0rad)
FEATURE [PartDesign::Pocket] Pocket001
  BaseFeature = -> Hole001
  Direction = (0,0,-1)
  Length = 5
  Length2 = 5
  Profile = -> Sketch005
  ReferenceAxis = -> Sketch005 [N_Axis]
  Suppressed = false
  Type = 1
FEATURE [PartDesign::Body] Body001  label="IndexArm"
  AllowCompound = false
  Group = -> [DatumPlane001,DatumPlane,Pad,Sketch001,Sketch,Sketch003,Sketch004,Pad001,Draft,Sketch005,Pocket,Hole001,Binder,Local_CS003,Local_CS004,Local_CS005,Local_CS007,Local_CS008,Local_CS,Local_CS001,LCS_IndexMirrorAttachment,Pocket001]
  Origin = -> Origin004
  Tip = -> Pocket001
FEATURE [Sketcher::SketchObject] Sketch002
  ArcFitTolerance = 0
  AttachmentSupport = -> [Body001]
  FullyConstrained = true
  MakeInternals = false
  MapMode = 2
FEATURE [App::DocumentObjectGroup] Parts
  Group = -> [Body001,Sketch002]
---- part Parts.FCStd = doc fcstd_c1b2f8807fc6 ----
FCSTD DOCUMENT  (FreeCAD 1.0RUnknown)
Label: Parts
License: All rights reserved
LicenseURL: https://en.wikipedia.org/wiki/All_rights_reserved
objects: Part::Feature×18, PartDesign::CoordinateSystem×10, Sketcher::SketchObject×7, App::Part×6, PartDesign::Hole×3, PartDesign::Body×3, PartDesign::Plane×2, PartDesign::Revolution×2, App::Link×1, PartDesign::AdditivePipe×1, PartDesign::PolarPattern×1, Part::FeaturePython×1
note: 68 computed .brp shape members not serialized (recipe doc carries the construction recipe); baked Part::Feature solids carry a one-line shape summary decoded from their .brp
EXTERNAL_REF file=Resources.FCStd obj=Spreadsheet

FEATURE [PartDesign::CoordinateSystem] LCS_Origin
  AttacherType = Attacher::AttachEngine3D
  AttachmentSupport = -> [X_Axis]
  MapMode = 2
FEATURE [Part::Feature] Part__Feature  label="6661K82_Ball Bearing"
  shape: bbox 22 x 22 x 7 mm, 14 faces (baked)
FEATURE [Part::Feature] Part__Feature001  label="6661K82_Ball Bearing001"
  shape: bbox 16.24 x 16.24 x 7 mm, 16 faces (baked)
FEATURE [Part::Feature] Part__Feature002  label="6661K82_Ball Bearing002"
  shape: bbox 3.379 x 3.379 x 3.379 mm, 2 faces (baked)
FEATURE [Part::Feature] Part__Feature003  label="6661K82_Ball Bearing003"
  shape: bbox 3.379 x 3.379 x 3.379 mm, 2 faces (baked)
FEATURE [Part::Feature] Part__Feature004  label="6661K82_Ball Bearing004"
  shape: bbox 3.379 x 3.379 x 3.379 mm, 2 faces (baked)
FEATURE [Part::Feature] Part__Feature005  label="6661K82_Ball Bearing005"
  shape: bbox 3.379 x 3.379 x 3.379 mm, 2 faces (baked)
FEATURE [Part::Feature] Part__Feature006  label="6661K82_Ball Bearing006"
  shape: bbox 3.379 x 3.379 x 3.379 mm, 2 faces (baked)
FEATURE [Part::Feature] Part__Feature007  label="6661K82_Ball Bearing007"
  shape: bbox 3.379 x 3.379 x 3.379 mm, 2 faces (baked)
FEATURE [Part::Feature] Part__Feature008  label="6661K82_Ball Bearing008"
  shape: bbox 3.379 x 3.379 x 3.379 mm, 2 faces (baked)
FEATURE [Part::Feature] Part__Feature009  label="6661K82_Ball Bearing009"
  shape: bbox 3.379 x 3.379 x 3.379 mm, 2 faces (baked)
FEATURE [Part::Feature] Part__Feature010  label="6661K82_Ball Bearing010"
  shape: bbox 3.379 x 3.379 x 3.379 mm, 2 faces (baked)
FEATURE [Part::Feature] Part__Feature011  label="6661K82_Ball Bearing011"
  shape: bbox 3.379 x 3.379 x 3.379 mm, 2 faces (baked)
FEATURE [Part::Feature] Part__Feature012  label="6661K82_Ball Bearing012"
  shape: bbox 3.379 x 3.379 x 3.379 mm, 2 faces (baked)
FEATURE [Part::Feature] Part__Feature013  label="6661K82_Ball Bearing013"
  shape: bbox 3.379 x 3.379 x 3.379 mm, 2 faces (baked)
FEATURE [Part::Feature] Part__Feature014  label="6661K82_Ball Bearing014"
  shape: bbox 3.379 x 3.379 x 3.379 mm, 2 faces (baked)
FEATURE [Part::Feature] Part__Feature015  label="6661K82_Ball Bearing015"
  shape: bbox 3.379 x 3.379 x 3.379 mm, 2 faces (baked)
FEATURE [Part::Feature] Part__Feature016  label="6661K82_Ball Bearing016"
  shape: bbox 16.32 x 16.32 x 1.635 mm, 6 faces (baked)
FEATURE [Part::Feature] Part__Feature017  label="6661K82_Ball Bearing017"
  shape: bbox 16.32 x 16.32 x 1.635 mm, 6 faces (baked)
FEATURE [App::Part] _661K82_Ball_Bearing  label="6661K82_Ball Bearing018"
  Group = -> [Part__Feature,Part__Feature001,Part__Feature002,Part__Feature003,Part__Feature004,Part__Feature005,Part__Feature006,Part__Feature007,Part__Feature008,Part__Feature009,Part__Feature010,Part__Feature011,Part__Feature012,Part__Feature013,Part__Feature014,Part__Feature015,Part__Feature016,Part__Feature017]
  Origin = -> Origin001
FEATURE [PartDesign::CoordinateSystem] LCS_Top
  AttacherType = Attacher::AttachEngine3D
  AttachmentOffset = pos=(0,0,3.5) rot=(0,0,1;0rad)
  AttachmentSupport = -> [X_Axis]
  MapMode = 2
  Placement = pos=(0,0,3.5) rot=(0,0,1;0rad)
  expr: .AttachmentOffset.Base.z = <<Dimensions>>.bearing_B / 2
FEATURE [PartDesign::CoordinateSystem] LCS_Bottom
  AttacherType = Attacher::AttachEngine3D
  AttachmentOffset = pos=(0,0,-3.5) rot=(0,0,1;0rad)
  AttachmentSupport = -> [X_Axis]
  MapMode = 2
  Placement = pos=(0,0,-3.5) rot=(0,0,1;0rad)
  expr: .AttachmentOffset.Base.z = -<<Dimensions>>.bearing_B / 2
FEATURE [App::Part] bEARING  label="Bearing"
  Group = -> [_661K82_Ball_Bearing,LCS_Top,LCS_Origin,LCS_Bottom]
  Origin = -> Origin
FEATURE [App::Link] Link  label="Dimensions"
  LinkedObject = -> <external Resources.FCStd>#Spreadsheet
FEATURE [Sketcher::SketchObject] Sketch
  ArcFitTolerance = 0
  AttachmentSupport = -> [XZ_Plane003]
  FullyConstrained = true
  MakeInternals = false
  MapMode = 5
  Placement = pos=(0,0,0) rot=(1,0,0;1.5708rad)
  expr: Constraints[10] = <<Dimensions>>.mirror_frame_thickness + 2 * <<Dimensions>>.clearance_loose_fit
  expr: Constraints[13] = <<Dimensions>>.mirror_frame_width + <<Dimensions>>.clearance_tight_fit
  expr: Constraints[19] = 0.5 mm
  expr: Constraints[23] = <<Dimensions>>.mirror_adjustment_screw_diameter / 2 + <<Dimensions>>.mirror_clip_edge_distance
  expr: Constraints[5] = <<Dimensions>>.mirror_clip_width / 2
  expr: Constraints[6] = <<Dimensions>>.mirror_clip_minimum_bend_radius
  sketch-geometry (9):
    g0: LineSegment StartX=-3 StartY=0 StartZ=0 EndX=5.65 EndY=0 EndZ=0
    g1: LineSegment StartX=5.65 StartY=7.5 StartZ=0 EndX=2.5 EndY=7.5 EndZ=0
    g2: ArcOfCircle CenterX=0 CenterY=13 CenterZ=0 NormalX=0 NormalY=0 NormalZ=1 AngleXU=0 Radius=6 StartAngle=4.3176 EndAngle=5.10718
    g3: ArcOfCircle CenterX=5.65 CenterY=7 CenterZ=0 NormalX=0 NormalY=0 NormalZ=1 AngleXU=0 Radius=0.5 StartAngle=5.97789 EndAngle=7.85398
    g4: ArcOfCircle CenterX=5.65 CenterY=0.5 CenterZ=0 NormalX=0 NormalY=0 NormalZ=1 AngleXU=0 Radius=0.5 StartAngle=4.71239 EndAngle=6.58848
    g5: GeomPoint [constr] X=0 Y=7 Z=0
    g6: ArcOfCircle CenterX=15.9625 CenterY=3.75 CenterZ=0 NormalX=0 NormalY=0 NormalZ=1 AngleXU=0 Radius=10.3125 StartAngle=2.83629 EndAngle=3.44689
    g7: GeomPoint [constr] X=5.65 Y=3.75 Z=0
    g8: ArcOfCircle CenterX=2.5 CenterY=7 CenterZ=0 NormalX=0 NormalY=0 NormalZ=1 AngleXU=0 Radius=0.5 StartAngle=1.5708 EndAngle=1.96559
  constraints (25):
    c: Horizontal(g0)
    c: Horizontal(g1)
    c: Tangent(g1,g3) = -1.5708
    c: Tangent(g0,g4) = -1.5708
    c: PointOnObject(g0,g-1)
    c: DistanceX(g0,g-1) = 3
    c: Radius(g4) = 0.5
    c: Equal(g3,g4)
    c: PointOnObject(g5,g2)
    c: Vertical(g5,g2)
    c: DistanceY(g0,g1) = 7.5
    c: PointOnObject(g5,g-2)
    c: PointOnObject(g7,g6)
    c: DistanceX(g1,g1) = 3.15
    c: Tangent(g6,g3) = 1.5708
    c: Tangent(g6,g4) = 1.5708
    c: Vertical(g1,g7)
    c: Vertical(g7,g0)
    c: Horizontal(g7,g6)
    c: DistanceY(g5,g1) = 0.5
    c: Horizontal(g2,g2)
    c: Tangent(g8,g1) = -1.5708
    c: Tangent(g8,g2) = 1.5708
    c: DistanceX(g5,g1) = 2.5
    c: Equal(g8,g3)
FEATURE [PartDesign::Plane] DatumPlane  label="Plane_Bottom"
  AttachmentOffset = pos=(0,0,-2) rot=(0,0,1;0rad)
  AttachmentSupport = -> [XY_Plane003]
  Length = 60
  MapMode = 5
  Placement = pos=(0,0,-2) rot=(0,0,1;0rad)
  ResizeMode = 0
  Width = 60
  expr: .AttachmentOffset.Base.z = -<<Dimensions>>.mirror_clip_thickness
FEATURE [Sketcher::SketchObject] Sketch002
  ArcFitTolerance = 0
  AttachmentSupport = -> [DatumPlane]
  FullyConstrained = true
  MakeInternals = false
  MapMode = 5
  Placement = pos=(0,0,-2) rot=(0,0,1;0rad)
  expr: Constraints[1] = <<Dimensions>>.mirror_adjustment_screw_diameter
  sketch-geometry (1):
    g0: Circle CenterX=0 CenterY=0 CenterZ=0 NormalX=0 NormalY=0 NormalZ=1 AngleXU=0 Radius=1.5
  constraints (2):
    c: Coincident(g0,g-1)
    c: Diameter(g0) = 3
FEATURE [PartDesign::Plane] DatumPlane001  label="Plane_Top"
  AttachmentSupport = -> [XY_Plane003]
  Length = 60
  MapMode = 5
  ResizeMode = 0
  Width = 60
FEATURE [Sketcher::SketchObject] Sketch001  label="Profile"
  ArcFitTolerance = 0
  AttachmentSupport = -> [YZ_Plane003]
  ExternalGeometry = -> [DatumPlane,DatumPlane001]
  FullyConstrained = true
  MakeInternals = false
  MapMode = 5
  Placement = pos=(0,0,0) rot=(0.57735,0.57735,0.57735;2.0944rad)
  expr: Constraints[7] = <<Dimensions>>.mirror_clip_width
  sketch-geometry (4):
    g0: LineSegment StartX=-3 StartY=9e-16 StartZ=0 EndX=3 EndY=9e-16 EndZ=0
    g1: LineSegment StartX=3 StartY=9e-16 StartZ=0 EndX=3 EndY=-2 EndZ=0
    g2: LineSegment StartX=3 StartY=-2 StartZ=0 EndX=-3 EndY=-2 EndZ=0
    g3: LineSegment StartX=-3 StartY=-2 StartZ=0 EndX=-3 EndY=9e-16 EndZ=0
  constraints (11):
    c: Coincident(g0,g1)
    c: Coincident(g1,g2)
    c: Coincident(g2,g3)
    c: Coincident(g3,g0)
    c: Horizontal(g0)
    c: Vertical(g1)
    c: Vertical(g3)
    c: DistanceX(g0,g0) = 6
    c: PointOnObject(g0,g-4)
    c: Symmetric(g2,g1,g-2)
    c: PointOnObject(g1,g-3)
FEATURE [PartDesign::AdditivePipe] AdditivePipe
  AuxilleryCurvelinear = true
  AuxillerySpineTangent = false
  Binormal = (0,0,0)
  Mode = 0
  Placement = pos=(0,0,0) rot=(1,1,1;2.0944rad)
  Profile = -> Sketch001
  Refine = true
  Spine = -> Sketch
  SpineTangent = false
  Suppressed = false
  Transformation = 0
  Transition = 0
FEATURE [PartDesign::Hole] Hole
  BaseFeature = -> AdditivePipe
  CustomThreadClearance = 0
  Depth = 2
  DepthType = 0
  Diameter = 3.2
  DrillForDepth = false
  DrillPoint = 1
  DrillPointAngle = 118
  HoleCutCountersinkAngle = 90
  HoleCutCustomValues = false
  HoleCutDepth = 0
  HoleCutDiameter = 6.1
  HoleCutType = 0
  ModelThread = false
  Placement = pos=(0,0,0) rot=(1,1,1;2.0944rad)
  Profile = -> Sketch002
  Reversed = true
  Suppressed = false
  Tapered = false
  TaperedAngle = 90
  ThreadClass = 0
  ThreadDepth = 2
  ThreadDepthType = 0
  ThreadDirection = 0
  ThreadFit = 1
  ThreadSize = 9
  ThreadType = 1
  Threaded = false
  UseCustomThreadClearance = false
  expr: Depth = <<Dimensions>>.mirror_clip_thickness
  expr: ThreadSize = <<Dimensions>>.mirror_adjustment_screw_type
FEATURE [PartDesign::Body] Body  label="MirrorClipBody"
  AllowCompound = false
  Group = -> [DatumPlane001,DatumPlane,Sketch,Sketch001,AdditivePipe,Sketch002,Hole]
  Origin = -> Origin003
  Tip = -> Hole
FEATURE [PartDesign::CoordinateSystem] LCS_Attachment
  AttacherType = Attacher::AttachEngine3D
  AttachmentSupport = -> [DatumPlane001]
  MapMode = 5
FEATURE [PartDesign::CoordinateSystem] LCS_Screw
  AttacherType = Attacher::AttachEngine3D
  AttachmentSupport = -> [DatumPlane]
  MapMode = 5
  Placement = pos=(0,0,-2) rot=(0,0,1;0rad)
FEATURE [App::Part] Part  label="MirrorClip"
  Group = -> [Body,LCS_Attachment,LCS_Screw]
  Origin = -> Origin002
FEATURE [PartDesign::CoordinateSystem] LCS_Origin001
  AttacherType = Attacher::AttachEngine3D
  AttachmentSupport = -> [X_Axis004]
  MapMode = 2
FEATURE [Sketcher::SketchObject] Sketch003
  ArcFitTolerance = 0
  AttachmentSupport = -> [XZ_Plane005]
  FullyConstrained = true
  MakeInternals = false
  MapMode = 5
  Placement = pos=(0,0,0) rot=(1,0,0;1.5708rad)
  expr: Constraints[12] = <<Dimensions>>.bearing_D / 2 + <<Dimensions>>.clearance_tight_fit
  expr: Constraints[13] = <<Dimensions>>.bearing_housing_min_thickness
  expr: Constraints[14] = <<Dimensions>>.bearing_B - <<Dimensions>>.clearance_loose_fit
  expr: Constraints[15] = <<Dimensions>>.bearing_Da / 2
  expr: Constraints[17] = <<Dimensions>>.bearing_housing_diameter / 2
  sketch-geometry (6):
    g0: LineSegment StartX=-22.5 StartY=0 StartZ=0 EndX=-22.5 EndY=-8.75 EndZ=0
    g1: LineSegment StartX=-22.5 StartY=-8.75 StartZ=0 EndX=-10 EndY=-8.75 EndZ=0
    g2: LineSegment StartX=-10 StartY=-8.75 StartZ=0 EndX=-10 EndY=-6.75 EndZ=0
    g3: LineSegment StartX=-10 StartY=-6.75 StartZ=0 EndX=-11.15 EndY=-6.75 EndZ=0
    g4: LineSegment StartX=-11.15 StartY=-6.75 StartZ=0 EndX=-11.15 EndY=0 EndZ=0
    g5: LineSegment StartX=-22.5 StartY=0 StartZ=0 EndX=-11.15 EndY=0 EndZ=0
  constraints (18):
    c: PointOnObject(g0,g-1)
    c: Vertical(g0)
    c: Horizontal(g1)
    c: Coincident(g2,g1)
    c: Vertical(g2)
    c: Coincident(g3,g2)
    c: Horizontal(g3)
    c: Coincident(g4,g3)
    c: PointOnObject(g4,g-1)
    c: Vertical(g4)
    c: Coincident(g5,g0)
    c: Coincident(g5,g4)
    c: DistanceX(g4,g-1) = 11.15
    c: DistanceY(g2,g2) = 2
    c: DistanceY(g4,g4) = 6.75
    c: DistanceX(g1,g-1) = 10
    c: Coincident(g1,g0)
    c: DistanceX(g0,g-1) = 22.5
FEATURE [PartDesign::Revolution] Revolution
  Angle = 360
  Angle2 = 60
  Axis = (0,2e-16,1)
  Base = (0,0,0)
  Placement = pos=(0,0,0) rot=(1,0,0;1.5708rad)
  Profile = -> Sketch003
  ReferenceAxis = -> Sketch003 [V_Axis]
  Suppressed = false
  Type = 0
FEATURE [Sketcher::SketchObject] Sketch004
  ArcFitTolerance = 0
  AttachmentSupport = -> [XY_Plane005]
  FullyConstrained = true
  MakeInternals = false
  MapMode = 5
  expr: Constraints[1] = <<Dimensions>>.bearing_D / 4 + <<Dimensions>>.bearing_housing_diameter / 4
  expr: Constraints[2] = <<Dimensions>>.bearing_housing_screw_diameter
  sketch-geometry (1):
    g0: Circle CenterX=-16.75 CenterY=0 CenterZ=0 NormalX=0 NormalY=0 NormalZ=1 AngleXU=0 Radius=1.5
  constraints (3):
    c: PointOnObject(g0,g-1)
    c: Distance(g0,g-1) = 16.75
    c: Diameter(g0) = 3
FEATURE [PartDesign::Hole] Hole001  label="Hole_Attachment"
  BaseFeature = -> Revolution
  CustomThreadClearance = 0
  Depth = 5
  DepthType = 0
  Diameter = 3.4
  DrillForDepth = false
  DrillPoint = 0
  DrillPointAngle = 118
  HoleCutCountersinkAngle = 90
  HoleCutCustomValues = false
  HoleCutDepth = 4
  HoleCutDiameter = 3.9
  HoleCutType = 1
  ModelThread = false
  Placement = pos=(0,0,0) rot=(1,0,0;1.5708rad)
  Profile = -> Sketch004
  Suppressed = false
  Tapered = false
  TaperedAngle = 90
  ThreadClass = 0
  ThreadDepth = 5
  ThreadDepthType = 0
  ThreadDirection = 0
  ThreadFit = 0
  ThreadSize = 9
  ThreadType = 1
  Threaded = false
  UseCustomThreadClearance = false
  expr: Depth = <<Dimensions>>.bearing_housing_screw_length + <<Dimensions>>.screw_hole_extra_depth - <<Dimensions>>.frame_thickness
  expr: HoleCutDepth = <<Dimensions>>.bearing_housing_ti_L
  expr: HoleCutDiameter = <<Dimensions>>.bearing_housing_ti_D
  expr: ThreadSize = <<Dimensions>>.bearing_housing_screw_type
FEATURE [PartDesign::PolarPattern] PolarPattern
  Angle = 360
  Axis = -> Z_Axis005
  BaseFeature = -> Hole001
  Mode = 0
  Occurrences = 3
  Offset = 120
  Originals = -> [Hole001]
  Placement = pos=(0,0,0) rot=(1,0,0;1.5708rad)
  Suppressed = false
  TransformMode = 0
FEATURE [PartDesign::Body] Body001  label="BearingHousingBody"
  AllowCompound = false
  Group = -> [Sketch003,Revolution,Sketch004,Hole001,PolarPattern]
  Origin = -> Origin005
  Tip = -> PolarPattern
FEATURE [App::Part] BearingCover  label="BearingHousing"
  Group = -> [LCS_Origin001,Body001]
  Origin = -> Origin004
FEATURE [PartDesign::CoordinateSystem] LCS_Origin002  label="LCS_ClampBottom"
  AttacherType = Attacher::AttachEngine3D
  AttachmentSupport = -> [X_Axis006]
  MapMode = 2
FEATURE [Sketcher::SketchObject] Sketch005
  ArcFitTolerance = 0
  AttachmentSupport = -> [XZ_Plane007]
  FullyConstrained = true
  MakeInternals = false
  MapMode = 5
  Placement = pos=(0,0,0) rot=(1,0,0;1.5708rad)
  expr: Constraints[13] = <<Dimensions>>.bearing_Da / 2 - 2 * <<Dimensions>>.clearance_loose_fit
  expr: Constraints[14] = 10 mm
  expr: Constraints[15] = <<Dimensions>>.bearing_da / 2
  expr: Constraints[16] = <<Dimensions>>.clearance_loose_fit
  sketch-geometry (6):
    g0: LineSegment StartX=0 StartY=0 StartZ=0 EndX=0 EndY=10 EndZ=0
    g1: LineSegment StartX=0 StartY=10 StartZ=0 EndX=5 EndY=10 EndZ=0
    g2: LineSegment StartX=5 StartY=10 StartZ=0 EndX=5 EndY=9.75 EndZ=0
    g3: LineSegment StartX=5 StartY=9.75 StartZ=0 EndX=9.5 EndY=9.75 EndZ=0
    g4: LineSegment StartX=9.5 StartY=9.75 StartZ=0 EndX=9.5 EndY=0 EndZ=0
    g5: LineSegment StartX=9.5 StartY=0 StartZ=0 EndX=0 EndY=0 EndZ=0
  constraints (17):
    c: Coincident(g-1,g0)
    c: Coincident(g0,g1)
    c: Horizontal(g1)
    c: Coincident(g1,g2)
    c: Vertical(g2)
    c: Coincident(g2,g3)
    c: Horizontal(g3)
    c: Coincident(g3,g4)
    c: Vertical(g4)
    c: Coincident(g4,g5)
    c: Coincident(g5,g0)
    c: Horizontal(g5)
    c: Vertical(g0)
    c: DistanceX(g5,g5) = 9.5
    c: DistanceY(g0,g0) = 10
    c: DistanceX(g1,g1) = 5
    c: DistanceY(g2,g2) = 0.25
FEATURE [PartDesign::Revolution] Revolution001
  Angle = 360
  Angle2 = 60
  Axis = (0,2e-16,1)
  Base = (0,0,0)
  Placement = pos=(0,0,0) rot=(1,0,0;1.5708rad)
  Profile = -> Sketch005
  ReferenceAxis = -> Sketch005 [V_Axis]
  Reversed = true
  Suppressed = false
  Type = 0
FEATURE [PartDesign::CoordinateSystem] LCS_ClampTop
  AttacherType = Attacher::AttachEngine3D
  AttachmentOffset = pos=(0,0,10) rot=(0,0,1;0rad)
  AttachmentSupport = -> [LCS_Origin002]
  MapMode = 2
  Placement = pos=(0,0,10) rot=(0,0,1;0rad)
FEATURE [Sketcher::SketchObject] Sketch006
  ArcFitTolerance = 0
  AttachmentSupport = -> [XY_Plane007]
  FullyConstrained = true
  MakeInternals = false
  MapMode = 5
  expr: Constraints[1] = <<Dimensions>>.shaft_end_cover_screw_diameter
  sketch-geometry (1):
    g0: Circle CenterX=0 CenterY=0 CenterZ=0 NormalX=0 NormalY=0 NormalZ=1 AngleXU=0 Radius=1.5
  constraints (2):
    c: Coincident(g0,g-1)
    c: Diameter(g0) = 3
FEATURE [PartDesign::Hole] Hole002
  BaseFeature = -> Revolution001
  CustomThreadClearance = 0
  Depth = 54.4277
  DepthType = 1
  Diameter = 3.4
  DrillForDepth = false
  DrillPoint = 1
  DrillPointAngle = 118
  HoleCutCountersinkAngle = 90
  HoleCutCustomValues = false
  HoleCutDepth = 0
  HoleCutDiameter = 6.7
  HoleCutType = 5
  ModelThread = false
  Placement = pos=(0,0,0) rot=(1,0,0;1.5708rad)
  Profile = -> Sketch006
  Reversed = true
  Suppressed = false
  Tapered = false
  TaperedAngle = 90
  ThreadClass = 0
  ThreadDepth = 54.4277
  ThreadDepthType = 0
  ThreadDirection = 0
  ThreadFit = 0
  ThreadSize = 9
  ThreadType = 1
  Threaded = false
  UseCustomThreadClearance = false
  expr: ThreadSize = <<Dimensions>>.shaft_end_cover_screw_type
FEATURE [PartDesign::Body] Body002  label="Body"
  AllowCompound = false
  Group = -> [Sketch005,Revolution001,Sketch006,Hole002]
  Origin = -> Origin007
  Tip = -> Hole002
FEATURE [App::Part] BearingClamp  label="BearinEndCover"
  Group = -> [LCS_Origin002,Body002,LCS_ClampTop]
  Origin = -> Origin006
FEATURE [PartDesign::CoordinateSystem] LCS_Origin003  label="LCS_Top001"
  AttacherType = Attacher::AttachEngine3D
  AttachmentSupport = -> [X_Axis008]
  MapMode = 2
FEATURE [Part::FeaturePython] Spacer  label="M3x35x5.5-Spacer"  # WARN: FeaturePython — macro-defined, semantics opaque (R4)
  Diameter = 2
  Invert = false
  LeftHanded = false
  Length = 22
  LengthCustom = 35
  MatchOuter = false
  OffsetAngle = 0
  Thread = false
  Type = 0
  Width = 1
FEATURE [PartDesign::CoordinateSystem] LCS_Bottom001
  AttacherType = Attacher::AttachEngine3D
FEATURE [App::Part] Standoff
  Group = -> [LCS_Origin003,Spacer,LCS_Bottom001]
  Origin = -> Origin008
---- part Resources.FCStd = doc fcstd_cf5bf867b5fe ----
FCSTD DOCUMENT  (FreeCAD 0.21RUnknown)
Label: Resources
License: All rights reserved
LicenseURL: http://en.wikipedia.org/wiki/All_rights_reserved
objects: Spreadsheet::Sheet×3

FEATURE [Spreadsheet::Sheet] Spreadsheet  label="Dimensions"
  cells = A1='Name; B1='Dimension; C1='Constraints; D1='set by; A3='General; A4='Clearance Loose Fit; B4(clearance_loose_fit)==max(<<Config>>.clearance_loose_fit; 0 mm); C4='>= 0; D4='user; A5='Clearance Tight Fit; B5(clearance_tight_fit)==max(<<Config>>.clearance_tight_fit; 0 mm); C5='>= 0; D5='user; A6='Minimum Wall thickness; B6(minimum_wall_thickness)==max(<<Config>>.minimum_wall_thickness; 0 mm); C6='>= 0; D6='user; A7='View Center Horizontal Offset; B7(view_center_offset_hor)==max(<<Config>>.view_center_offset_hor; 0 mm); C7='>= 0; D7='user; A8='View Center Vertical Offset; B8(view_center_offset_vert)==max(<<Config>>.view_center_offset_vert; 0 mm); C8='>= 0; D8='user; A9='Spacing between Index arm and Frame; B9(index_arm_spacing)==max(<<Config>>.index_arm_spacing; 0 mm); C9='>= 0; D9='user; A10='Screw Hole Extra Depth; B10(screw_hole_extra_depth)==max(0 mm; Spreadsheet001.screw_hole_extra_depth); C10='>= 0; D10='user; A12='Handle; A13='Outer Width; B13(handle_outer_width)==max(<<Config>>.handle_width; minimum_wall_thickness); C13='>= Min wall thickness; D13='user; A14='Inner Width; B14(handle_inner_width)==max(handle_connector_screw_diameter + 2 * minimum_wall_thickness; handle_outer_width - handle_height / 6); C14='>= 2* Min wall thickness +  screw diameter; D14='calc; A15='Height; B15(handle_height)==max(<<Config>>.handle_height; minimum_wall_thickness); C15='>= Min wall thickness; D15='user; A16='Length; B16(handle_length)==max(<<Config>>.handle_length; minimum_wall_thickness); C16='>= Min wall thickness; D16='user; A17='Screw Type; B17(handle_screw_type)==<<Config>>.handle_screw_type; C17='TODO: restrict to M2.M3,M4,M6,M8; D17='user; A18='Connector Screw Diameter; B18(handle_connector_screw_diameter)==handle_screw_type == <<ConfiguartionTables>>.screws_name_m2 ? <<ConfiguartionTables>>.screws_ds_m2 : (handle_screw_type == <<ConfiguartionTables>>.screws_name_m3 ? <<ConfiguartionTables>>.screws_ds_m3 : (handle_screw_type == <<ConfiguartionTables>>.screws_name_m4 ? <<ConfiguartionTables>>.screws_ds_m4 : (handle_screw_type == <<ConfiguartionTables>>.screws_name_m6 ? <<ConfiguartionTables>>.screws_ds_m6 : (handle_screw_type == <<ConfiguartionTables>>.screws_name_m8 ? <<ConfiguartionTables>>.screws_ds_m8 : <<ConfiguartionTables>>.screws_ds_m3)))); C18='none; D18='calc; A19='Screw Countersink Diameter; B19(handle_countersink_diameter)==handle_screw_type == <<ConfiguartionTables>>.screws_name_m2 ? <<ConfiguartionTables>>.screws_dk_10642_m2 : (handle_screw_type == <<ConfiguartionTables>>.screws_name_m3 ? <<ConfiguartionTables>>.screws_dk_10642_m3 : (handle_screw_type == <<ConfiguartionTables>>.screws_name_m4 ? <<ConfiguartionTables>>.screws_dk_10642_m4 : (handle_screw_type == <<ConfiguartionTables>>.screws_name_m6 ? <<ConfiguartionTables>>.screws_dk_10642_m6 : (handle_screw_type == <<ConfiguartionTables>>.screws_name_m8 ? <<ConfiguartionTables>>.screws_dk_10642_m8 : <<ConfiguartionTables>>.screws_dk_10642_m3)))); C19='none; D19='calc; A20='Nut Width (S); B20(handle_nut_S)==handle_screw_type == <<ConfiguartionTables>>.screws_name_m2 ? <<ConfiguartionTables>>.nut_S_m2 : (handle_screw_type == <<ConfiguartionTables>>.screws_name_m3 ? <<ConfiguartionTables>>.nut_S_m3 : (handle_screw_type == <<ConfiguartionTables>>.screws_name_m4 ? <<ConfiguartionTables>>.nut_S_m4 : (handle_screw_type == <<ConfiguartionTables>>.screws_name_m6 ? <<ConfiguartionTables>>.nut_S_m6 : (handle_screw_type == <<ConfiguartionTables>>.screws_name_m8 ? <<ConfiguartionTables>>.nut_S_m8 : <<ConfiguartionTables>>.nut_S_m3)))); C20='none; D20='calc; A21='Nut Thickness (M); B21(handle_nut_M)==handle_screw_type == <<ConfiguartionTables>>.screws_name_m2 ? <<ConfiguartionTables>>.nut_M_m2 : (handle_screw_type == <<ConfiguartionTables>>.screws_name_m3 ? <<ConfiguartionTables>>.nut_M_m3 : (handle_screw_type == <<ConfiguartionTables>>.screws_name_m4 ? <<ConfiguartionTables>>.nut_M_m4 : (handle_screw_type == <<ConfiguartionTables>>.screws_name_m6 ? <<ConfiguartionTables>>.nut_M_m6 : (handle_screw_type == <<ConfiguartionTables>>.screws_name_m8 ? <<ConfiguartionTables>>.nut_M_m8 : <<ConfiguartionTables>>.nut_M_m3)))); C21='none; D21='calc; A22='Screw Length; B22(handle_screw_length)==max(0 mm; <<Config>>.handle_screw_length); C22='>= 0 ; D22='user; A23='Screw Hole Depth; B23(handle_screw_hole_depth)==handle_screw_length + screw_hole_extra_depth - frame_thickness; C23='none; D23='calc; A24='Handle Threaded Insert Diameter; B24(handle_ti_D)==handle_screw_type == <<ConfiguartionTables>>.screws_name_m2 ? <<ConfiguartionTables>>.ti_D_m2 : (handle_screw_type == <<ConfiguartionTables>>.screws_name_m3 ? <<ConfiguartionTables>>.ti_D_m3 : (handle_screw_type == <<ConfiguartionTables>>.screws_name_m4 ? <<ConfiguartionTables>>.ti_D_m4 : (handle_screw_type == <<ConfiguartionTables>>.screws_name_m6 ? <<ConfiguartionTables>>.ti_D_m6 : (handle_screw_type == <<ConfiguartionTables>>.screws_name_m8 ? <<ConfiguartionTables>>.ti_D_m8 : <<ConfiguartionTables>>.ti_D_m3)))); C24='none; D24='calc; A25='Handle Threaded Insert Depth; B25(handle_ti_L)==handle_screw_type == <<ConfiguartionTables>>.screws_name_m2 ? <<ConfiguartionTables>>.ti_L_m2 : (handle_screw_type == <<ConfiguartionTables>>.screws_name_m3 ? <<ConfiguartionTables>>.ti_L_m3 : (handle_screw_type == <<ConfiguartionTables>>.screws_name_m4 ? <<ConfiguartionTables>>.ti_L_m4 : (handle_screw_type == <<ConfiguartionTables>>.screws_name_m6 ? <<ConfiguartionTables>>.ti_L_m6 : (handle_screw_type == <<ConfiguartionTables>>.screws_name_m8 ? <<ConfiguartionTables>>.ti_L_m8 : <<ConfiguartionTables>>.ti_L_m3)))); C25='none; D25='calc; A27='Frame; A28='Width; B28(frame_width)==15 mm; A29='Thickness; B29(frame_thickness)==max(<<Config>>.frame_thickness; minimum_wall_thickness); C29='<= min wall thickness; D29='user; A32='Shaft Spacer Diameter; B32(spacer_diameter)==10 mm; A41='Mirrors; A42='Frame Thickness; B42(mirror_frame_thickness)==max(minimum_wall_thickness; <<Config>>.mirror_frame_thickness); C42='>= min wall thickness; D42='user; A43='Frame Width; B43(mirror_frame_width)==max(minimum_wall_thickness; <<Config>>.mirror_frame_width); C43='>= min wall thickness; D43='user; A44='Adjustment Screw type; B44(mirror_adjustment_screw_type)==<<Config>>.mirror_adjustment_screw_type; C44='TODO: restrict to M2.M3,M4,M6,M8; D44='user; A45='Adjustment Screw Diameter; B45(mirror_adjustment_screw_diameter)==mirror_adjustment_screw_type == <<ConfiguartionTables>>.screws_name_m2 ? <<ConfiguartionTables>>.screws_ds_m2 : (mirror_adjustment_screw_type == <<ConfiguartionTables>>.screws_name_m3 ? <<ConfiguartionTables>>.screws_ds_m3 : (mirror_adjustment_screw_type == <<ConfiguartionTables>>.screws_name_m4 ? <<ConfiguartionTables>>.screws_ds_m4 : (mirror_adjustment_screw_type == <<ConfiguartionTables>>.screws_name_m6 ? <<ConfiguartionTables>>.screws_ds_m6 : (mirror_adjustment_screw_type == <<ConfiguartionTables>>.screws_name_m8 ? <<ConfiguartionTables>>.screws_ds_m8 : <<ConfiguartionTables>>.screws_ds_m3)))); C45='none; D45='calc; A46='Adjustment Screw Threaded Insert Diameter; B46(mirror_adjustment_ti_D)==viewscope_screw_type == <<ConfiguartionTables>>.screws_name_m2 ? <<ConfiguartionTables>>.ti_D_m2 : (viewscope_screw_type == <<ConfiguartionTables>>.screws_name_m3 ? <<ConfiguartionTables>>.ti_D_m3 : (viewscope_screw_type == <<ConfiguartionTables>>.screws_name_m4 ? <<ConfiguartionTables>>.ti_D_m4 : (viewscope_screw_type == <<ConfiguartionTables>>.screws_name_m6 ? <<ConfiguartionTables>>.ti_D_m6 : (viewscope_screw_type == <<ConfiguartionTables>>.screws_name_m8 ? <<ConfiguartionTables>>.ti_D_m8 : <<ConfiguartionTables>>.ti_D_m3)))); C46='none; D46='calc; A47='Adjustment Screw Threaded Insert Depth; B47(mirror_adjustment_ti_L)==mirror_adjustment_screw_type == <<ConfiguartionTables>>.screws_name_m2 ? <<ConfiguartionTables>>.ti_L_m2 : (mirror_adjustment_screw_type == <<ConfiguartionTables>>.screws_name_m3 ? <<ConfiguartionTables>>.ti_L_m3 : (mirror_adjustment_screw_type == <<ConfiguartionTables>>.screws_name_m4 ? <<ConfiguartionTables>>.ti_L_m4 : (mirror_adjustment_screw_type == <<ConfiguartionTables>>.screws_name_m6 ? <<ConfiguartionTables>>.ti_L_m6 : (mirror_adjustment_screw_type == <<ConfiguartionTables>>.screws_name_m8 ? <<ConfiguartionTables>>.ti_L_m8 : <<ConfiguartionTables>>.ti_L_m3)))); C47='none; D47='calc; A49='Mirror Clip; A50='Clip Width; B50(mirror_clip_width)==max(<<Config>>.mirror_clip_width; mirror_adjustment_screw_diameter + 2 * minimum_wall_thickness); C50='>= screw hole diameter + 2* min wall thickness; D50='user; A51='Clip Thickness; B51(mirror_clip_thickness)==max(<<Config>>.mirror_clip_thickness; 0 mm); C51='>= 0; D51='user; A52='Minimum Bend Radius; B52(mirror_clip_minimum_bend_radius)==max(<<Config>>.mirror_clip_minimum_bend_radius; 0 mm); C52='>= 0; D52='user; A53='Mirror Edge Distance; B53(mirror_clip_edge_distance)==max(<<Config>>.mirror_clip_edge_distance; 0 mm); C53='>= 0; D53='user; A55='Horizon Mirror; A56='Mirror Width; B56(horizon_mirror_mirror_width)==max(<<Config>>.horizon_mirror_mirror_width; 0 mm); C56='>= 0; D56='user; A57='MIrror Height; B57(horizon_mirror_mirror_height)==max(<<Config>>.horizon_mirror_mirror_height; 0 mm); C57='>= 0; D57='user; A58='Mirror Thickness; B58(horizon_mirror_mirror_thickness)==max(<<Config>>.horizon_mirror_mirror_thickness; 0 mm); C58='>= 0; D58='user; A59='Base Width; B59(horizon_mirror_base_width)==3 mm; A60='Base Thickness; B60(horizon_mirror_base_thickness)==max(<<Config>>.horizon_mirror_base_thickness; minimum_wall_thickness); C60='>= min wall thickness; D60='user; A61='Frame Lip Width; B61(horizon_mirror_frame_lip_width)==max(<<Config>>.horizon_mirror_frame_lip_width; 0 mm); C61='>= 0mm; D61='user; A62='Attachment Screw Type; B62(horizon_mirror_screw_type)==<<Config>>.horizon_mirror_screw_type; C62='TODO: restrict to M2.M3,M4,M6,M8; D62='user; A63='Attachment Screw Diameter; B63(horizon_mirror_screw_diameter)==horizon_mirror_screw_type == <<ConfiguartionTables>>.screws_name_m2 ? <<ConfiguartionTables>>.screws_ds_m2 : (horizon_mirror_screw_type == <<ConfiguartionTables>>.screws_name_m3 ? <<ConfiguartionTables>>.screws_ds_m3 : (horizon_mirror_screw_type == <<ConfiguartionTables>>.screws_name_m4 ? <<ConfiguartionTables>>.screws_ds_m4 : (horizon_mirror_screw_type == <<ConfiguartionTables>>.screws_name_m6 ? <<ConfiguartionTables>>.screws_ds_m6 : (horizon_mirror_screw_type == <<ConfiguartionTables>>.screws_name_m8 ? <<ConfiguartionTables>>.screws_ds_m8 : <<ConfiguartionTables>>.screws_ds_m3)))); C63='none; D63='calc; A64='Connector Screw Countersink Diameter; B64(horizon_mirror_countersink_diameter)==horizon_mirror_screw_type == <<ConfiguartionTables>>.screws_name_m2 ? <<ConfiguartionTables>>.screws_dk_10642_m2 : (horizon_mirror_screw_type == <<ConfiguartionTables>>.screws_name_m3 ? <<ConfiguartionTables>>.screws_dk_10642_m3 : (horizon_mirror_screw_type == <<ConfiguartionTables>>.screws_name_m4 ? <<ConfiguartionTables>>.screws_dk_10642_m4 : (horizon_mirror_screw_type == <<ConfiguartionTables>>.screws_name_m6 ? <<ConfiguartionTables>>.screws_dk_10642_m6 : (horizon_mirror_screw_type == <<ConfiguartionTables>>.screws_name_m8 ? <<ConfiguartionTables>>.screws_dk_10642_m8 : <<ConfiguartionTables>>.screws_dk_10642_m3)))); C64='none; D64='calc; A65='Nut Width (S); B65(index_mirror_nut_S)==horizon_mirror_screw_type == <<ConfiguartionTables>>.screws_name_m2 ? <<ConfiguartionTables>>.nut_S_m2 : (horizon_mirror_screw_type == <<ConfiguartionTables>>.screws_name_m3 ? <<ConfiguartionTables>>.nut_S_m3 : (horizon_mirror_screw_type == <<ConfiguartionTables>>.screws_name_m4 ? <<ConfiguartionTables>>.nut_S_m4 : (horizon_mirror_screw_type == <<ConfiguartionTables>>.screws_name_m6 ? <<ConfiguartionTables>>.nut_S_m6 : (horizon_mirror_screw_type == <<ConfiguartionTables>>.screws_name_m8 ? <<ConfiguartionTables>>.nut_S_m8 : <<ConfiguartionTables>>.nut_S_m3)))); C65='none; D65='calc; A66='Offset; B66(horizon_mirror_offset)==80 mm; A67='Angle; B67(horizon_mirror_angle)==atan(view_center_offset_vert / horizon_mirror_offset) / 2; D67='calc; A68='Mirror Offset Origin; B68(horizon_mirror_mirror_offset)==view_center_offset_hor - horizon_mirror_mirror_height / 2; C68='none; D68='calc; A70='Index Mirror; A71='MIrror Width; B71(index_mirror_mirror_width)==max(<<Config>>.index_mirror_mirror_width; 0 mm); C71='>= 0; D71='user; A72='Mirror Height; B72(index_mirror_mirror_height)==max(<<Config>>.index_mirror_mirror_height; 0 mm); C72='>= 0; D72='user; A73='Mirror Thickness; B73(index_mirror_mirror_thickness)==max(<<Config>>.index_mirror_mirror_thickness; 0 mm); C73='>= 0; D73='user; A74='Base Diameter; B74(index_mirror_base_diameter)==index_mirror_mirror_width + 2 * mirror_frame_width; +232 more cells
FEATURE [Spreadsheet::Sheet] Spreadsheet001  label="Config"
  cells = A1='Name; B1='Value; C1='Description; A3='General; A4='Minimum Wall thickness; B4(minimum_wall_thickness)==0.5 mm; C4='General minimum Wall thickness. Walls get limited by this value; A5='Clearance Loose Fit; B5(clearance_loose_fit)==0.25 mm; C5='Clearance to achieve a loose fit (for interactions without tight tolerances). Does not apply to screws; A6='Clearance Tight Fit; B6(clearance_tight_fit)==0.15 mm; C6='Clearance to achieve a tight fit (for interactions with tight tolerances). Does not apply to screws; A7='View Center Horizontal Offset; B7(view_center_offset_hor)==30 mm; C7='Horizontal offset of the center of the view when looking through the scope. This is measured from the top of the frame; A8='View Center Vertical Offset; B8(view_center_offset_vert)==80 mm; C8='Vertical offset of the center of the view when looking through the scope. This is measured from the center of the shaft of the index arm; A9='Index Arm Space; B9(index_arm_spacing)==2 mm; C9='Spacing between index arm and frame; A10='Screw Hole Extra Depth; B10(screw_hole_extra_depth)==2 mm; C10='How much deeper is the hole than the actual screw length; A12='Frame; A13='Thickness; B13(frame_thickness)==2 mm; C13='Thickness of the frame; A17='Viewscope; A18='Collar Thickness; B18(viewscope_collar_thickness)==7.5 mm; C18='Thickness of the collar around the scope; A19='Collar Width; B19(viewscope_collar_width)==6 mm; C19='Width of the collar around the scope; A20='Inner Diameter; B20(viewscope_inner_diameter)==20 mm; C20='Minmum inner diameter of the scope; A21='Screw Type; B21(viewscope_screw_type)='M3; C21='Screw type to attach the view scope (Must be M2,M3,M4,M6 or M8); A22='Screw Head Support Thickness; B22(viewscope_screwhead_support_thickness)==4 mm; C22='Thickness of surface supporting the screwhead; A23='Thickness; B23(viewscope_wall_thickness)==1 mm; C23='Thickness of the scope itself; A24='Eyepiece Diameter; B24(viewscope_eye_diameter)==40 mm; C24='Diameter of the eyepiece; A28='Handle; A29='Screw Type; B29(handle_screw_type)='M3; C29='Screw type to attach the handle (Must be M2,M3,M4,M6 or M8); A30='Screw Length; B30(handle_screw_length)==10 mm; C30='Length of screw to attach handle; A31='Width; B31(handle_width)==10 mm; C31='Maximum width of the handle; A32='Length; B32(handle_length)==100 mm; C32='Length of the handle; A33='Height; B33(handle_height)==20 mm; C33='Height of the handle; A37='Mirrors; A38='Frame Thickness; B38(mirror_frame_thickness)==7 mm; C38='Thickness of the frames for both the index- and horizon mirror; A39='Frame Width; B39(mirror_frame_width)==3 mm; C39='Width of the frames for both the index- and horizon mirror; A40='Adjustment Screw Type; B40(mirror_adjustment_screw_type)='M3; C40='Type of the adjustment screws for the mirrors (Must be M2,M3,M4,M6 or M8); A42='Mirror Clip; A43='Clip Width; B43(mirror_clip_width)==6 mm; C43='WIdth of the spring clip to attach the mirrors; A44='Clip Thickness; B44(mirror_clip_thickness)==2 mm; C44='Thickness of the spring clip to attach the mirrors; A45='Minimum Bend Radius; B45(mirror_clip_minimum_bend_radius)==0.5 mm; C45='Minimum bend radius for the spring steel of the clip; A46='Mirror Edge Distance; B46(mirror_clip_edge_distance)==1 mm; A48='Index Mirror; A49='Mirror Width; B49(index_mirror_mirror_width)==50 mm; C49='Width of the index mirror; A50='Mirror Height; B50(index_mirror_mirror_height)==40 mm; C50='Height of the index mirror; A51='Mirror Thickness; B51(index_mirror_mirror_thickness)==3 mm; C51='Thickness of the index mirror; A52='Screw Type; B52(index_mirror_screw_type)='M3; C52='Type of the screws for attaching the mirror frame to the index arm (Must be M2,M3,M4,M6 or M8); A53='Base Thickness; B53(index_mirror_base_thickness)==1 mm; C53='Thickness of the base for the index mirror; A54='Screw Center Distance; B54(index_mirror_screw_center_distance)==18 mm; C54='Distance of attachmemt screws to shaft center; A56='Horizon Mirror; A57='Mirror Width; B57(horizon_mirror_mirror_width)==40 mm; C57='Width of the horizon mirror; A58='Mirror Height; B58(horizon_mirror_mirror_height)==50 mm; C58='Total Height of the horizon mirror. Half of this dimension is the actual mirror and the remaining half is just the glass; A59='Mirror Thickness; B59(horizon_mirror_mirror_thickness)==3 mm; C59='Thickness of the horizon mirror. The difference between the thickness of the glass and mirror are assumed to be insignificant; A60='Base Thickness; B60(horizon_mirror_base_thickness)==1 mm; C60='Thickness of the base for the horizon mirror; A61='Frame Lip Width; B61(horizon_mirror_frame_lip_width)==1 mm; C61='Width of the lip holding the horizon mirror in place; A62='Screw Type; B62(horizon_mirror_screw_type)='M3; C62='Type of the screws for attaching the mirror  to the frame (Must be M2,M3,M4,M6 or M8); A65='Bearing; A66='Type; B66(bearing_type)='608; C66='Type of bearing (Must be one of 608, 6000, 6001, 6002); A67='Housing DIameter; B67(bearing_housing_diameter)==45 mm; C67='Diameter of the housing for the bearing; A68='Housing Screw Type; B68(bearing_housing_screw_type)='M3; C68='Screw type to attach the bearing housing to the frame (Must be M2,M3,M4,M6 or M8); A69='Housing Screw Length; B69(bearing_housing_screw_length)==5 mm; C69='Length of screws to attach the bearing housing to the frame ; A70='Housing Minimum Thickness; B70(bearing_housing_min_thickness)==2 mm; C70='Minimum thickness of the bearing housing; A72='Shaft; A73='Base Thickness; B73(shaft_base_thickness)==1 mm; C73='Thickness of the base attaching the shaft to the index mirror and frame; A74='End Cover Screw Type; B74(shaft_end_cover_screw_type)='M3; C74='Screw type to attach the end cover to the shaft  (Must be M2,M3,M4,M6 or M8); A75='End Cover Screw Length; B75(shaft_end_cover_screw_length)==10 mm; C75='Length of screw to attach the end cover to the shaft; A78='Shades; A79='Spacing; B79(shade_spacing)==4 mm; C79='Spacing between filters in a set; A80='Frame Thickness; B80(shade_frame_thickness)==2 mm; C80='Thickness of frame (excluding thickness of the filter itself); A81='Shaft Screw Type; B81(shade_shaft_type)='M4; C81='Type of screw for shaft of the filter
FEATURE [Spreadsheet::Sheet] Spreadsheet002  label="ConfiguartionTables"
  BearingType = 0
  Type = 0
  bearing = 0
  cells = A1='Screws/Bolts; A2='Name; B2='Thread diameter; C2='Head diameter ISO 4762; D2='Head height ISO 10642; E2='Nut width (S); F2='Nut Thickness (M); G2='TI Depth; H2='TI Diameter; A4(screws_name_m2)='M2; B4(screws_ds_m2)==2 mm; C4(screws_dk_4762_m2)==3.8 mm; D4(screws_dk_10642_m2)==4.1 mm; E4(nut_S_m2)==4 mm; F4(nut_M_m2)==1.6 mm; G4(ti_L_m2)==4 mm; H4(ti_D_m2)==3.1 mm; A5(screws_name_m3)='M3; B5(screws_ds_m3)==3 mm; C5(screws_dk_4762_m3)==5.5 mm; D5(screws_dk_10642_m3)==6.72 mm; E5(nut_S_m3)==5.5 mm; F5(nut_M_m3)==2.4 mm; G5(ti_L_m3)==4 mm; H5(ti_D_m3)==3.9 mm; A6(screws_name_m4)='M4; B6(screws_ds_m4)==4 mm; C6(screws_dk_4762_m4)==7 mm; D6(screws_dk_10642_m4)==8.96 mm; E6(nut_S_m4)==7 mm; F6(nut_M_m4)==3.2 mm; G6(ti_L_m4)==5 mm; H6(ti_D_m4)==5.5 mm; A7(screws_name_m6)='M6; B7(screws_ds_m6)==6 mm; C7(screws_dk_4762_m6)==10 mm; D7(screws_dk_10642_m6)==13.44 mm; E7(nut_S_m6)==10 mm; F7(nut_M_m6)==5.2 mm; A8(screws_name_m8)='M8; B8(screws_ds_m8)==8 mm; C8(screws_dk_4762_m8)==13 mm; D8(screws_dk_10642_m8)==17.92 mm; E8(nut_S_m8)==13 mm; F8(nut_M_m8)==6.8 mm; M9='s; B16='Bearing; B17='Type; C17='bore diameter (d); D17='outside diameter (D); E17='Abutment diameter, shaft shoulder (da); F17='Housing shoulder diameter (Da); G17='Width (B); B18(bearing_type)==hiddenref(.bearing.String); C18(bearing_d)==.C19; D18(bearing_D)==.D19; E18(bearing_da)==.E19; F18(bearing_Da)==.F19; G18(bearing_B)==.G19; B19='608; C19==8 mm; D19==22 mm; E19==10 mm; F19==20 mm; G19==7 mm; B20='6000; C20==10 mm; D20==26 mm; E20==12 mm; F20==24 mm; G20==8 mm; B21='6001; C21==12 mm; D21==28 mm; E21==14 mm; F21==26 mm; G21==8 mm; B22='6002; C22==15 mm; D22==32 mm; E22==17 mm; F22==30 mm; G22==9 mm
  expr: .BearingType.Enum = cells[<<F4:|>>]
  expr: .Type.Enum = cells[<<F4:|>>]
  expr: .bearing.Enum = cells[<<B19:|>>]
  expr: .cells.Bind.C18.G18 = tuple(.cells; <<C>> + str(hiddenref(bearing) + 19); <<G>> + str(hiddenref(bearing) + 19))
  expr: BearingType = <<Config>>.bearing_type
---- part Scale.FCStd = doc fcstd_a2707baac5d1 ----
FCSTD DOCUMENT  (FreeCAD 1.0RUnknown)
Label: Scale
License: All rights reserved
LicenseURL: http://en.wikipedia.org/wiki/All_rights_reserved
objects: TechDraw::DrawViewPart×8, Sketcher::SketchObject×6, PartDesign::CoordinateSystem×6, PartDesign::Pad×2, PartDesign::Hole×2, Image::ImagePlane×2, PartDesign::Body×2, PartDesign::Plane×2, App::Part×2, App::Link×1, TechDraw::DrawSVGTemplate×1, PartDesign::AdditivePipe×1, PartDesign::SubtractivePipe×1, TechDraw::DrawPage×1
note: 40 computed .brp shape members not serialized (recipe doc carries the construction recipe); baked Part::Feature solids carry a one-line shape summary decoded from their .brp
EXTERNAL_REF file=Resources.FCStd obj=Spreadsheet

FEATURE [Sketcher::SketchObject] Sketch003
  ArcFitTolerance = 0
  AttachmentSupport = -> [XY_Plane009]
  FullyConstrained = true
  MakeInternals = false
  MapMode = 5
  expr: Constraints[6] = <<Dimensions>>.scale_width
  expr: Constraints[7] = <<Dimensions>>.scale_outer_radius
  expr: Constraints[8] = <<Dimensions>>.scale_angle + 2 * <<Dimensions>>.scale_extra_angle
  expr: Constraints[9] = <<Dimensions>>.scale_angle + 2 * <<Dimensions>>.scale_extra_angle
  sketch-geometry (4):
    g0: ArcOfCircle CenterX=1.5e-15 CenterY=0 CenterZ=0 NormalX=0 NormalY=0 NormalZ=1 AngleXU=0 Radius=180 StartAngle=3.97062 EndAngle=5.45415
    g1: LineSegment StartX=-121.606 StartY=-132.71 StartZ=0 EndX=-114.85 EndY=-125.337 EndZ=0
    g2: ArcOfCircle CenterX=-1.3e-15 CenterY=0 CenterZ=0 NormalX=0 NormalY=0 NormalZ=1 AngleXU=0 Radius=170 StartAngle=3.97062 EndAngle=5.45415
    g3: LineSegment StartX=114.85 StartY=-125.337 StartZ=0 EndX=121.606 EndY=-132.71 EndZ=0
  constraints (12):
    c: Coincident(g1,g0)
    c: Coincident(g2,g1)
    c: Coincident(g3,g2)
    c: Coincident(g3,g0)
    c: Symmetric(g2,g1,g-2)
    c: Symmetric(g0,g0,g-2)
    c: Distance(g1) = 10
    c: Radius(g0) = 180
    c: Angle(g2) = 1.48353
    c: Angle(g0) = 1.48353
    c: PointOnObject(g0,g-1)
    c: PointOnObject(g2,g-1)
FEATURE [PartDesign::Pad] Pad002
  Direction = (0,0,1)
  Length = 2
  Length2 = 10
  Profile = -> Sketch003
  ReferenceAxis = -> Sketch003 [N_Axis]
  Suppressed = false
  Type = 0
  expr: Length = <<Dimensions>>.scale_thickness
FEATURE [PartDesign::CoordinateSystem] LCS_Origin002
  AttacherType = Attacher::AttachEngine3D
  AttachmentSupport = -> [X_Axis008]
  MapMode = 2
FEATURE [Sketcher::SketchObject] Sketch  label="AttachmentHoles"
  ArcFitTolerance = 0
  AttachmentOffset = pos=(0,0,2) rot=(0,0,1;0rad)
  AttachmentSupport = -> [XY_Plane009]
  FullyConstrained = true
  MakeInternals = false
  MapMode = 5
  Placement = pos=(0,0,2) rot=(0,0,1;0rad)
  expr: .AttachmentOffset.Base.z = <<Dimensions>>.scale_thickness
  expr: Constraints[11] = <<Dimensions>>.scale_angle / 2
  expr: Constraints[12] = <<Dimensions>>.scale_attachment_screw_head_diameter / 2 + 2 mm
  expr: Constraints[2] = <<Dimensions>>.scale_attachment_screw_diameter
  expr: Constraints[8] = <<Dimensions>>.scale_outer_radius - <<Dimensions>>.scale_width / 2
  sketch-geometry (12):
    g0: Circle CenterX=-110.068 CenterY=-136.052 CenterZ=0 NormalX=0 NormalY=0 NormalZ=1 AngleXU=0 Radius=1.5
    g1: Circle CenterX=110.068 CenterY=-136.052 CenterZ=0 NormalX=0 NormalY=0 NormalZ=1 AngleXU=0 Radius=1.5
    g2: LineSegment [constr] StartX=0 StartY=0 StartZ=0 EndX=0 EndY=-175 EndZ=0
    g3: LineSegment [constr] StartX=0 StartY=0 StartZ=0 EndX=-106.533 EndY=-138.837 EndZ=0
    g4: LineSegment [constr] StartX=0 StartY=0 StartZ=0 EndX=-110.068 EndY=-136.052 EndZ=0
    g5: Circle CenterX=-39.34 CenterY=-170.521 CenterZ=0 NormalX=0 NormalY=0 NormalZ=1 AngleXU=0 Radius=1.5
    g6: Circle CenterX=39.34 CenterY=-170.521 CenterZ=0 NormalX=0 NormalY=0 NormalZ=1 AngleXU=0 Radius=1.5
    g7: LineSegment [constr] StartX=-39.34 StartY=-170.521 StartZ=0 EndX=0 EndY=0 EndZ=0
    g8: LineSegment [constr] StartX=39.34 StartY=-170.521 StartZ=0 EndX=0 EndY=0 EndZ=0
    g9: LineSegment [constr] StartX=-110.068 StartY=-136.052 StartZ=0 EndX=-39.34 EndY=-170.521 EndZ=0
    g10: LineSegment [constr] StartX=-39.34 StartY=-170.521 StartZ=0 EndX=39.34 EndY=-170.521 EndZ=0
    g11: LineSegment [constr] StartX=39.34 StartY=-170.521 StartZ=0 EndX=110.068 EndY=-136.052 EndZ=0
  constraints (29):
    c: Symmetric(g1,g0,g-2)
    c: Equal(g0,g1)
    c: Diameter(g0) = 3
    c: Coincident(g2,g-1)
    c: PointOnObject(g2,g-2)
    c: Coincident(g3,g2)
    c: Coincident(g4,g2)
    c: Coincident(g4,g0)
    c: Distance(g2) = 175
    c: Equal(g3,g2)
    c: Equal(g4,g2)
    c: Angle(g3,g2) = 0.654498
    c: Distance(g0,g3) = 4.5
    c: Equal(g5,g6)
    c: Equal(g6,g0)
    c: Coincident(g7,g5)
    c: Coincident(g8,g6)
    c: Coincident(g7,g2)
    c: Coincident(g2,g8)
    c: Equal(g4,g7)
    c: Equal(g7,g8)
    c: Coincident(g9,g0)
    c: Coincident(g9,g5)
    c: Coincident(g10,g5)
    c: Coincident(g10,g6)
    c: Horizontal(g10)
    c: Coincident(g11,g6)
    c: Coincident(g11,g1)
    c: Equal(g9,g10)
FEATURE [PartDesign::Hole] Hole
  BaseFeature = -> Pad002
  CustomThreadClearance = 0
  Depth = 471.953
  DepthType = 1
  Diameter = 3.2
  DrillForDepth = false
  DrillPoint = 1
  DrillPointAngle = 118
  HoleCutCountersinkAngle = 90
  HoleCutCustomValues = false
  HoleCutDepth = 0
  HoleCutDiameter = 6.1
  HoleCutType = 2
  ModelThread = false
  Profile = -> Sketch
  Suppressed = false
  Tapered = false
  TaperedAngle = 90
  ThreadClass = 0
  ThreadDepth = 471.953
  ThreadDepthType = 0
  ThreadDirection = 0
  ThreadFit = 1
  ThreadSize = 9
  ThreadType = 2
  Threaded = false
  UseCustomThreadClearance = false
FEATURE [App::Link] Link  label="Dimensions"
  LinkedObject = -> <external Resources.FCStd>#Spreadsheet
FEATURE [PartDesign::CoordinateSystem] LCS_Screw1
  AttacherType = Attacher::AttachEngine3D
  AttachmentSupport = -> [Sketch]
  MapMode = 11
  Placement = pos=(-110.068,-136.052,2) rot=(0,0,1;1.5708rad)
FEATURE [PartDesign::CoordinateSystem] LCS_Screw2  label="LCS_Screw4"
  AttacherType = Attacher::AttachEngine3D
  AttachmentSupport = -> [Sketch]
  MapMode = 11
  Placement = pos=(110.068,-136.052,2) rot=(0,0,1;1.5708rad)
FEATURE [PartDesign::CoordinateSystem] LCS_Origin  label="LCS_OriginTop"
  AttacherType = Attacher::AttachEngine3D
  AttachmentOffset = pos=(0,0,2) rot=(0,0,1;0rad)
  AttachmentSupport = -> [X_Axis010]
  MapMode = 2
  Placement = pos=(0,0,2) rot=(0,0,1;0rad)
  expr: .AttachmentOffset.Base.z = <<Dimensions>>.scale_thickness
FEATURE [TechDraw::DrawSVGTemplate] Template
  Height = 210
  Orientation = 1
  Template = /app/share/Mod/TechDraw/Templates/A4_Landscape_blank.svg
  Width = 297
FEATURE [Image::ImagePlane] large_scale  label="main_scale"
  Placement = pos=(0.07,-158.3,2.01) rot=(0,0,1;0rad)
  XSize = 213.043
  YSize = 43.3071
  expr: .Placement.Base.z = <<Dimensions>>.scale_thickness + 0.01 mm
FEATURE [Image::ImagePlane] vernier_scale
  Placement = pos=(0,-183.7,2.01) rot=(0,0,1;0rad)
  XSize = 26.6701
  YSize = 8.31852
  expr: .Placement.Base.z = <<Dimensions>>.scale_thickness + 0.01 mm
FEATURE [Sketcher::SketchObject] Sketch006
  ArcFitTolerance = 0
  AttachmentSupport = -> [YZ_Plane009]
  ExternalGeometry = -> [Sketch003]
  FullyConstrained = true
  MakeInternals = false
  MapMode = 5
  Placement = pos=(0,0,0) rot=(0.57735,0.57735,0.57735;2.0944rad)
  sketch-geometry (4):
    g0: LineSegment StartX=-181 StartY=0.92265 StartZ=0 EndX=-180 EndY=1.5 EndZ=0
    g1: LineSegment StartX=-180 StartY=1.5 StartZ=0 EndX=-180 EndY=-5e-14 EndZ=0
    g2: LineSegment StartX=-180 StartY=-5e-14 StartZ=0 EndX=-181 EndY=0.57735 EndZ=0
    g3: LineSegment StartX=-181 StartY=0.57735 StartZ=0 EndX=-181 EndY=0.92265 EndZ=0
  constraints (11):
    c: Coincident(g0,g1)
    c: Coincident(g1,g2)
    c: Coincident(g2,g3)
    c: Coincident(g3,g0)
    c: Vertical(g1)
    c: Vertical(g3)
    c: Coincident(g1,g-3)
    c: Distance(g1) = 1.5
    c: DistanceX(g0,g0) = 1
    c: Equal(g0,g2)
    c: Angle(g1,g2) = 1.0472
FEATURE [PartDesign::AdditivePipe] AdditivePipe
  AuxilleryCurvelinear = true
  AuxillerySpineTangent = false
  BaseFeature = -> Hole
  Binormal = (0,0,0)
  Mode = 0
  Profile = -> Sketch006
  Spine = -> Sketch003 [Edge1]
  SpineTangent = false
  Suppressed = false
  Transformation = 0
  Transition = 0
FEATURE [PartDesign::Body] Body003  label="MainScaleBody"
  AllowCompound = false
  Group = -> [Sketch003,Pad002,Sketch,Hole,Sketch006,AdditivePipe]
  Origin = -> Origin009
  Tip = -> AdditivePipe
FEATURE [PartDesign::Plane] DatumPlane  label="Plane_Bottom"
  AttachmentOffset = pos=(0,0,-0.5) rot=(0,0,1;0rad)
  AttachmentSupport = -> [XY_Plane]
  Length = 60
  MapMode = 5
  Placement = pos=(0,0,-0.5) rot=(0,0,1;0rad)
  ResizeMode = 0
  Width = 60
FEATURE [Sketcher::SketchObject] Sketch004
  ArcFitTolerance = 0
  AttachmentSupport = -> [DatumPlane]
  FullyConstrained = true
  MakeInternals = false
  MapMode = 5
  Placement = pos=(0,0,-0.5) rot=(0,0,1;0rad)
  expr: Constraints[11] = <<Dimensions>>.scale_outer_radius
  expr: Constraints[6] = <<Dimensions>>.vernier_scale_width
  expr: Constraints[7] = <<Dimensions>>.vernier_scale_angle
  sketch-geometry (4):
    g0: ArcOfCircle CenterX=-2.36e-14 CenterY=0 CenterZ=0 NormalX=0 NormalY=0 NormalZ=1 AngleXU=0 Radius=180 StartAngle=4.58149 EndAngle=4.84329
    g1: ArcOfCircle CenterX=-2.36e-14 CenterY=0 CenterZ=0 NormalX=0 NormalY=0 NormalZ=1 AngleXU=0 Radius=190 StartAngle=4.58149 EndAngle=4.84329
    g2: LineSegment StartX=-23.4947 StartY=-178.46 StartZ=0 EndX=-24.8 EndY=-188.375 EndZ=0
    g3: LineSegment StartX=23.4947 StartY=-178.46 StartZ=0 EndX=24.8 EndY=-188.375 EndZ=0
  constraints (12):
    c: Coincident(g2,g0)
    c: Coincident(g2,g1)
    c: Coincident(g3,g0)
    c: Coincident(g3,g1)
    c: Perpendicular(g0,g2)
    c: Perpendicular(g0,g3)
    c: Distance(g2) = 10
    c: Angle(g1) = 0.261799
    c: Symmetric(g1,g1,g-2)
    c: Coincident(g0,g1)
    c: Coincident(g0,g-1)
    c: Radius(g0) = 180
FEATURE [PartDesign::Plane] DatumPlane001  label="Plane_Top"
  AttachmentOffset = pos=(0,0,2) rot=(0,0,1;0rad)
  AttachmentSupport = -> [XY_Plane]
  Length = 60
  MapMode = 5
  Placement = pos=(0,0,2) rot=(0,0,1;0rad)
  ResizeMode = 0
  Width = 60
  expr: .AttachmentOffset.Base.z = <<Dimensions>>.scale_thickness
FEATURE [PartDesign::Pad] Pad
  Direction = (0,0,1)
  Length = 2
  Length2 = 10
  Placement = pos=(0,0,-0.5) rot=(0,0,1;0rad)
  Profile = -> Sketch004
  ReferenceAxis = -> Sketch004 [N_Axis]
  Suppressed = false
  Type = 3
  UpToFace = -> DatumPlane001 [Plane]
  expr: Length = <<Dimensions>>.scale_thickness
FEATURE [Sketcher::SketchObject] Sketch005
  ArcFitTolerance = 0
  AttachmentSupport = -> [DatumPlane001]
  ExternalGeometry = -> [Sketch004]
  FullyConstrained = true
  MakeInternals = false
  MapMode = 5
  Placement = pos=(0,0,2) rot=(0,0,1;0rad)
  expr: Constraints[0] = <<Dimensions>>.scale_attachment_screw_diameter
  expr: Constraints[7] = <<Dimensions>>.vernier_scale_width / 2
  sketch-geometry (3):
    g0: Circle CenterX=-19.1818 CenterY=-184.003 CenterZ=0 NormalX=0 NormalY=0 NormalZ=1 AngleXU=0 Radius=1.5
    g1: Circle CenterX=19.1818 CenterY=-184.003 CenterZ=0 NormalX=0 NormalY=0 NormalZ=1 AngleXU=0 Radius=1.5
    g2: ArcOfCircle [constr] CenterX=-2.36e-14 CenterY=0 CenterZ=0 NormalX=0 NormalY=0 NormalZ=1 AngleXU=0 Radius=185 StartAngle=4.58149 EndAngle=4.84329
  constraints (8):
    c: Diameter(g1) = 3
    c: Equal(g0,g1)
    c: PointOnObject(g2,g-6)
    c: Symmetric(g-5,g-4,g2)
    c: Coincident(g2,g-5)
    c: PointOnObject(g0,g2)
    c: Symmetric(g0,g1,g-2)
    c: Distance(g0,g2) = 5
FEATURE [PartDesign::Hole] Hole001
  BaseFeature = -> Pad
  CustomThreadClearance = 0
  Depth = 25
  DepthType = 0
  Diameter = 3.4
  DrillForDepth = false
  DrillPoint = 1
  DrillPointAngle = 118
  HoleCutCountersinkAngle = 90
  HoleCutCustomValues = false
  HoleCutDepth = 0
  HoleCutDiameter = 6.1
  HoleCutType = 0
  ModelThread = false
  Placement = pos=(0,0,-0.5) rot=(0,0,1;0rad)
  Profile = -> Sketch005
  Suppressed = false
  Tapered = false
  TaperedAngle = 90
  ThreadClass = 0
  ThreadDepth = 25
  ThreadDepthType = 0
  ThreadDirection = 0
  ThreadFit = 0
  ThreadSize = 9
  ThreadType = 1
  Threaded = false
  UseCustomThreadClearance = false
FEATURE [Sketcher::SketchObject] Sketch007
  ArcFitTolerance = 0
  AttachmentSupport = -> [YZ_Plane]
  ExternalGeometry = -> [Sketch004,DatumPlane001]
  FullyConstrained = true
  MakeInternals = false
  MapMode = 5
  Placement = pos=(0,0,0) rot=(0.57735,0.57735,0.57735;2.0944rad)
  expr: Constraints[13] = 0.5 mm - <<Dimensions>>.clearance_loose_fit
  expr: Constraints[4] = 1.5 mm + 2 * <<Dimensions>>.clearance_loose_fit
  expr: Constraints[8] = 1 mm + <<Dimensions>>.clearance_loose_fit
  sketch-geometry (5):
    g0: LineSegment StartX=-180 StartY=-0.25 StartZ=0 EndX=-181.25 EndY=0.471688 EndZ=0
    g1: LineSegment StartX=-181.25 StartY=0.471688 StartZ=0 EndX=-181.25 EndY=1.02831 EndZ=0
    g2: LineSegment StartX=-181.25 StartY=1.02831 StartZ=0 EndX=-180 EndY=1.75 EndZ=0
    g3: LineSegment StartX=-180 StartY=-0.25 StartZ=0 EndX=-180 EndY=1.75 EndZ=0
    g4: GeomPoint [constr] X=-180 Y=2 Z=0
  constraints (14):
    c: Coincident(g1,g0)
    c: Coincident(g2,g1)
    c: Coincident(g3,g2)
    c: Vertical(g3)
    c: DistanceY(g3,g3) = 2
    c: Angle(g3,g0) = 1.0472
    c: Vertical(g1)
    c: Angle(g2,g3) = 1.0472
    c: DistanceX(g1,g2) = 1.25
    c: Coincident(g0,g3)
    c: PointOnObject(g-3,g3)
    c: PointOnObject(g4,g-4)
    c: Vertical(g4,g2)
    c: DistanceY(g2,g4) = 0.25
FEATURE [PartDesign::SubtractivePipe] SubtractivePipe
  AuxilleryCurvelinear = true
  AuxillerySpineTangent = false
  BaseFeature = -> Hole001
  Binormal = (0,0,0)
  Mode = 0
  Placement = pos=(0,0,-0.5) rot=(0,0,1;0rad)
  Profile = -> Sketch007
  Spine = -> Sketch004 [Edge2]
  SpineTangent = false
  Suppressed = false
  Transformation = 0
  Transition = 0
FEATURE [PartDesign::Body] Body  label="VernierScaleBody"
  AllowCompound = false
  Group = -> [DatumPlane001,DatumPlane,Sketch004,Pad,Sketch005,Hole001,Sketch007,SubtractivePipe]
  Origin = -> Origin
  Tip = -> SubtractivePipe
FEATURE [TechDraw::DrawViewPart] View001  label="Small1"
  CoarseView = false
  Direction = (0,0,1)
  Focus = 100
  HardHidden = false
  IsoCount = 0
  IsoHidden = false
  IsoVisible = false
  LockPosition = false
  Perspective = false
  Rotation = 0
  ScaleType = 0
  ScrubCount = 0
  SeamHidden = false
  SeamVisible = false
  SmoothHidden = false
  SmoothVisible = true
  Source = -> [Body]
  X = 148.5
  XDirection = (1,0,0)
  Y = 35.7651
  expr: Y = 30 mm + 1 mm * (<<VernierScaleBody>>.Shape.BoundBox.YMax - <<VernierScaleBody>>.Shape.BoundBox.YMin) / 2
FEATURE [TechDraw::DrawViewPart] View004  label="Small2"
  CoarseView = false
  Direction = (0,0,1)
  Focus = 100
  HardHidden = false
  IsoCount = 0
  IsoHidden = false
  IsoVisible = false
  LockPosition = false
  Perspective = false
  Rotation = 0
  ScaleType = 0
  ScrubCount = 0
  SeamHidden = false
  SeamVisible = false
  SmoothHidden = false
  SmoothVisible = true
  Source = -> [Body]
  X = 148.5
  XDirection = (1,0,0)
  Y = 75.7651
  expr: Y = <<Small1>>.Y + 40 mm
FEATURE [TechDraw::DrawViewPart] View005  label="Small3"
  CoarseView = false
  Direction = (0,0,1)
  Focus = 100
  HardHidden = false
  IsoCount = 0
  IsoHidden = false
  IsoVisible = false
  LockPosition = false
  Perspective = false
  Rotation = 0
  ScaleType = 0
  ScrubCount = 0
  SeamHidden = false
  SeamVisible = false
  SmoothHidden = false
  SmoothVisible = true
  Source = -> [Body]
  X = 148.5
  XDirection = (1,0,0)
  Y = 115.765
  expr: Y = <<Small2>>.Y + 40 mm
FEATURE [TechDraw::DrawViewPart] View006  label="Small4"
  CoarseView = false
  Direction = (0,0,1)
  Focus = 100
  HardHidden = false
  IsoCount = 0
  IsoHidden = false
  IsoVisible = false
  LockPosition = false
  Perspective = false
  Rotation = 0
  ScaleType = 0
  ScrubCount = 0
  SeamHidden = false
  SeamVisible = false
  SmoothHidden = false
  SmoothVisible = true
  Source = -> [Body]
  X = 148.5
  XDirection = (1,0,0)
  Y = 155.765
  expr: Y = <<Small3>>.Y + 40 mm
FEATURE [App::Part] Part  label="VernierScale"
  Group = -> [Body,vernier_scale,LCS_Origin]
  Origin = -> Origin010
FEATURE [PartDesign::CoordinateSystem] LCS_Screw3  label="LCS_Screw2"
  AttacherType = Attacher::AttachEngine3D
  AttachmentSupport = -> [Sketch]
  MapMode = 11
  Placement = pos=(-39.34,-170.521,2) rot=(0,0,1;1.5708rad)
FEATURE [PartDesign::CoordinateSystem] LCS_Screw004  label="LCS_Screw3"
  AttacherType = Attacher::AttachEngine3D
  AttachmentSupport = -> [Sketch]
  MapMode = 11
  Placement = pos=(39.34,-170.521,2) rot=(0,0,1;1.5708rad)
FEATURE [App::Part] Part002  label="MainScale"
  Group = -> [Body003,LCS_Origin002,LCS_Screw1,LCS_Screw2,large_scale,LCS_Screw3,LCS_Screw004]
  Origin = -> Origin008
FEATURE [TechDraw::DrawViewPart] View  label="Large4"
  CoarseView = false
  Direction = (0,0,1)
  Focus = 100
  HardHidden = false
  IsoCount = 0
  IsoHidden = false
  IsoVisible = false
  LockPosition = false
  Perspective = false
  Rotation = 0
  ScaleType = 0
  ScrubCount = 0
  SeamHidden = false
  SeamVisible = false
  SmoothHidden = false
  SmoothVisible = true
  Source = -> [Part002]
  X = 148.5
  XDirection = (1,0,0)
  Y = 157.831
  expr: Y = <<Large3>>.Y + 40 mm
FEATURE [TechDraw::DrawViewPart] View002  label="Large2"
  CoarseView = false
  Direction = (0,0,1)
  Focus = 100
  HardHidden = false
  IsoCount = 0
  IsoHidden = false
  IsoVisible = false
  LockPosition = false
  Perspective = false
  Rotation = 0
  ScaleType = 0
  ScrubCount = 0
  SeamHidden = false
  SeamVisible = false
  SmoothHidden = false
  SmoothVisible = true
  Source = -> [Part002]
  X = 148.5
  XDirection = (1,0,0)
  Y = 77.8314
  expr: Y = <<Large1>>.Y + 40 mm
FEATURE [TechDraw::DrawViewPart] View003  label="Large3"
  CoarseView = false
  Direction = (0,0,1)
  Focus = 100
  HardHidden = false
  IsoCount = 0
  IsoHidden = false
  IsoVisible = false
  LockPosition = true
  Perspective = false
  Rotation = 0
  ScaleType = 0
  ScrubCount = 0
  SeamHidden = false
  SeamVisible = false
  SmoothHidden = false
  SmoothVisible = true
  Source = -> [Part002]
  X = 148.5
  XDirection = (1,0,0)
  Y = 117.831
  expr: Y = <<Large2>>.Y + 40 mm
FEATURE [TechDraw::DrawViewPart] View007  label="Large1"
  CoarseView = false
  Direction = (0,0,1)
  Focus = 100
  HardHidden = false
  IsoCount = 0
  IsoHidden = false
  IsoVisible = false
  LockPosition = false
  Perspective = false
  Rotation = 0
  ScaleType = 0
  ScrubCount = 0
  SeamHidden = false
  SeamVisible = false
  SmoothHidden = false
  SmoothVisible = true
  Source = -> [Part002]
  X = 148.5
  XDirection = (1,0,0)
  Y = 37.8314
  expr: Y = 10 mm + 1 mm * (<<MainScaleBody>>.Shape.BoundBox.YMax - <<MainScaleBody>>.Shape.BoundBox.YMin) / 2
FEATURE [TechDraw::DrawPage] Page  label="ScaleBackground"
  KeepUpdated = true
  NextBalloonIndex = 1
  ProjectionType = 0
  Template = -> Template
  Views = -> [View,View001,View002,View003,View004,View005,View006,View007]
---- part Shadeset.FCStd = doc fcstd_564eb966e311 ----
FCSTD DOCUMENT  (FreeCAD 1.0RUnknown)
Label: Shadeset
License: All rights reserved
LicenseURL: http://en.wikipedia.org/wiki/All_rights_reserved
objects: Sketcher::SketchObject×8, PartDesign::CoordinateSystem×7, PartDesign::Plane×5, PartDesign::Hole×5, App::Link×4, App::DocumentObjectGroup×3, Part::FeaturePython×3, PartDesign::Pad×3, PartDesign::Body×3, App::FeaturePython×1, PartDesign::Pocket×1, PartDesign::Mirrored×1, App::Part×1
note: 63 computed .brp shape members not serialized (recipe doc carries the construction recipe); baked Part::Feature solids carry a one-line shape summary decoded from their .brp
EXTERNAL_REF file=Resources.FCStd obj=Spreadsheet
EXTERNAL_REF file=Shade.FCStd obj=Local_CS001
EXTERNAL_REF file=Shade.FCStd obj=Body003
EXTERNAL_REF file=Shade.FCStd obj=FilterFrameBottom_LCS_ShaftTop
EXTERNAL_REF file=Shade.FCStd obj=Local_CS
EXTERNAL_REF file=Shade.FCStd obj=Assembly

FEATURE [App::Link] Link  label="Dimensions"
  LinkedObject = -> <external Resources.FCStd>#Spreadsheet
FEATURE [PartDesign::CoordinateSystem] LCS_Origin
  AttacherType = Attacher::AttachEngine3D
  AttachmentSupport = -> [X_Axis]
  MapMode = 2
FEATURE [App::DocumentObjectGroup] Constraints
FEATURE [App::FeaturePython] Variables  # WARN: FeaturePython — macro-defined, semantics opaque (R4)
  Type = App::PropertyContainer
FEATURE [App::DocumentObjectGroup] Configurations
FEATURE [PartDesign::Plane] DatumPlane  label="PlaneSideInner"
  AttachmentOffset = pos=(0,0,9.25) rot=(0,0,1;0rad)
  AttachmentSupport = -> [YZ_Plane001]
  Length = 60
  MapMode = 5
  Placement = pos=(9.25,0,0) rot=(0.57735,0.57735,0.57735;2.0944rad)
  ResizeMode = 0
  Width = 60
  expr: .AttachmentOffset.Base.z = (1 + <<Dimensions>>.shade_amount) * <<Dimensions>>.shade_spacer_length / 2 + <<Dimensions>>.clearance_loose_fit
FEATURE [PartDesign::CoordinateSystem] Local_CS001  label="LCS_Origin001"
  AttacherType = Attacher::AttachEngine3D
  AttachmentSupport = -> [X_Axis001]
  MapMode = 2
FEATURE [App::Link] Attachment  label="Attachment001"
  AttachedBy = #Local_CS001
  AttachedTo = Parent Assembly#LCS_Origin
  LinkedObject = -> Body
  SolverId = Asm4EE
  expr: Placement = LCS_Origin.Placement * AttachmentOffset * Local_CS001.Placement ^ -1
FEATURE [App::Link] Spacer
  AttachedBy = #Local_CS001
  AttachedTo = Attachment#Local_CS
  LinkPlacement = pos=(3.25,0,7) rot=(0.707107,0,0.707107;3.14159rad)
  LinkedObject = -> <external Shade.FCStd>#Body003
  Placement = pos=(3.25,0,7) rot=(0.707107,0,0.707107;3.14159rad)
  SolverId = Asm4EE
  expr: Placement = Attachment.Placement * Local_CS.Placement * AttachmentOffset * Shade#Local_CS001.Placement ^ -1
FEATURE [Part::FeaturePython] Screw  label="M4x20-Screw"  # WARN: FeaturePython — macro-defined, semantics opaque (R4)
  AttachedBy = Origin
  AttachedTo = Attachment#Local_CS003
  Diameter = 6
  Invert = false
  LeftHanded = false
  Length = 7
  LengthCustom = 20
  MatchOuter = false
  OffsetAngle = 0
  Placement = pos=(11.25,0,7) rot=(0.707107,0,0.707107;3.14159rad)
  SolverId = Asm4EE
  Thread = false
  Type = 76
  expr: Placement = Attachment.Placement * Local_CS003.Placement * AttachmentOffset
FEATURE [Part::FeaturePython] Nut  label="M4-Nut"  # WARN: FeaturePython — macro-defined, semantics opaque (R4)
  AttachedBy = Origin
  AttachedTo = Attachment#Local_CS002
  Diameter = 6
  Invert = false
  LeftHanded = false
  MatchOuter = false
  OffsetAngle = 0
  Placement = pos=(-10.75,0,7) rot=(0,1,0;4.71239rad)
  SolverId = Asm4EE
  Thread = false
  Type = 31
  expr: Placement = Attachment.Placement * Local_CS002.Placement * AttachmentOffset
FEATURE [App::Link] Filter  label="Shade"
  AttachedBy = #FilterFrameBottom_LCS_ShaftTop
  AttachedTo = Spacer#Local_CS
  AttachmentOffset = pos=(0,0,0) rot=(0,0,1;3.14159rad)
  LinkPlacement = pos=(-2.75,0,7) rot=(0,-1,0;4.71239rad)
  LinkedObject = -> <external Shade.FCStd>#Assembly
  Placement = pos=(-2.75,0,7) rot=(0,-1,0;4.71239rad)
  SolverId = Asm4EE
  expr: Placement = Spacer.Placement * Shade#Local_CS.Placement * AttachmentOffset * Shade#FilterFrameBottom_LCS_ShaftTop.Placement ^ -1
FEATURE [PartDesign::Plane] DatumPlane001  label="PlaneSideOuter"
  AttachmentOffset = pos=(0,0,2) rot=(0,0,1;0rad)
  AttachmentSupport = -> [DatumPlane]
  Length = 60
  MapMode = 5
  Placement = pos=(11.25,0,0) rot=(0.57735,0.57735,0.57735;2.0944rad)
  ResizeMode = 0
  Width = 60
FEATURE [Sketcher::SketchObject] Sketch002  label="SketchHole"
  ArcFitTolerance = 0
  AttachmentSupport = -> [DatumPlane001]
  FullyConstrained = true
  MakeInternals = false
  MapMode = 5
  Placement = pos=(11.25,0,0) rot=(0.57735,0.57735,0.57735;2.0944rad)
  expr: Constraints[1] = <<Dimensions>>.shade_shaft_diameter
  expr: Constraints[2] = <<Dimensions>>.shade_shaft_diameter + 2 mm + 1 mm
  sketch-geometry (1):
    g0: Circle CenterX=0 CenterY=7 CenterZ=0 NormalX=0 NormalY=0 NormalZ=1 AngleXU=0 Radius=2
  constraints (3):
    c: PointOnObject(g0,g-2)
    c: Diameter(g0) = 4
    c: DistanceY(g-1,g0) = 7
FEATURE [Sketcher::SketchObject] Sketch001  label="SketchBase"
  ArcFitTolerance = 0
  AttachmentSupport = -> [YZ_Plane001]
  ExternalGeometry = -> [Sketch002]
  FullyConstrained = true
  MakeInternals = false
  MapMode = 5
  Placement = pos=(0,0,0) rot=(0.57735,0.57735,0.57735;2.0944rad)
  sketch-geometry (6):
    g0: LineSegment StartX=-15 StartY=0 StartZ=0 EndX=15 EndY=0 EndZ=0
    g1: ArcOfCircle CenterX=-1.3e-15 CenterY=7 CenterZ=0 NormalX=0 NormalY=0 NormalZ=1 AngleXU=0 Radius=5 StartAngle=0 EndAngle=3.14159
    g2: LineSegment StartX=-5 StartY=7 StartZ=0 EndX=-15 EndY=7 EndZ=0
    g3: LineSegment StartX=-15 StartY=7 StartZ=0 EndX=-15 EndY=0 EndZ=0
    g4: LineSegment StartX=5 StartY=7 StartZ=0 EndX=15 EndY=7 EndZ=0
    g5: LineSegment StartX=15 StartY=7 StartZ=0 EndX=15 EndY=0 EndZ=0
  constraints (18):
    c: Coincident(g1,g-3)
    c: Coincident(g2,g3)
    c: Coincident(g3,g0)
    c: Vertical(g3)
    c: Coincident(g4,g5)
    c: Coincident(g5,g0)
    c: Coincident(g4,g1)
    c: Coincident(g2,g1)
    c: Horizontal(g2)
    c: Perpendicular(g1,g2)
    c: Perpendicular(g1,g4)
    c: Horizontal(g1,g1)
    c: Diameter(g1) = 10
    c: Distance(g2) = 10
    c: Equal(g2,g4)
    c: Vertical(g5)
    c: PointOnObject(g0,g-1)
    c: PointOnObject(g0,g-1)
FEATURE [PartDesign::CoordinateSystem] Local_CS  label="LCS_ShaftEnd"
  AttacherType = Attacher::AttachEngine3D
  AttachmentOffset = pos=(0,0,-2) rot=(0,0,1;0rad)
  AttachmentSupport = -> [Sketch002]
  MapMode = 11
  Placement = pos=(9.25,0,7) rot=(0.707107,0,0.707107;3.14159rad)
FEATURE [PartDesign::CoordinateSystem] Local_CS002  label="LCS_Nut"
  AttacherType = Attacher::AttachEngine3D
  AttachmentOffset = pos=(0,0,-20) rot=(1,0,0;3.14159rad)
  AttachmentSupport = -> [Local_CS]
  MapMode = 5
  Placement = pos=(-10.75,0,7) rot=(0,1,0;4.71239rad)
  expr: .AttachmentOffset.Base.z = -(<<Dimensions>>.shade_amount + 1) * <<Dimensions>>.shade_spacer_length - 2 mm
FEATURE [PartDesign::CoordinateSystem] Local_CS003  label="LCS_Bolt"
  AttacherType = Attacher::AttachEngine3D
  AttachmentSupport = -> [Sketch002]
  MapMode = 11
  Placement = pos=(11.25,0,7) rot=(0.707107,0,0.707107;3.14159rad)
FEATURE [PartDesign::Pad] Pad001
  Direction = (1,0,0)
  Length = 10
  Length2 = 10
  Offset = 2
  Placement = pos=(0,0,0) rot=(1,1,1;2.0944rad)
  Profile = -> Sketch001
  ReferenceAxis = -> Sketch001 [N_Axis]
  Suppressed = false
  Type = 3
  UpToFace = -> DatumPlane
FEATURE [Sketcher::SketchObject] Sketch003
  ArcFitTolerance = 0
  AttachmentSupport = -> [YZ_Plane001]
  ExternalGeometry = -> [Sketch001]
  FullyConstrained = true
  MakeInternals = false
  MapMode = 5
  Placement = pos=(0,0,0) rot=(0.57735,0.57735,0.57735;2.0944rad)
  sketch-geometry (1):
    g0: Circle CenterX=0 CenterY=7 CenterZ=0 NormalX=0 NormalY=0 NormalZ=1 AngleXU=0 Radius=5
  constraints (2):
    c: Coincident(g0,g-3)
    c: PointOnObject(g-3,g0)
FEATURE [PartDesign::Pocket] Pocket
  BaseFeature = -> Pad001
  Direction = (-1,0,0)
  Length = 0
  Length2 = 5
  Placement = pos=(0,0,0) rot=(1,1,1;2.0944rad)
  Profile = -> Sketch003
  ReferenceAxis = -> Sketch003 [N_Axis]
  Suppressed = false
  Type = 3
  UpToFace = -> DatumPlane
FEATURE [PartDesign::Mirrored] Mirrored
  BaseFeature = -> Pocket
  MirrorPlane = -> YZ_Plane001
  Originals = -> [Pad001,Pocket]
  Placement = pos=(0,0,0) rot=(1,1,1;2.0944rad)
  Refine = true
  Suppressed = false
  TransformMode = 0
FEATURE [PartDesign::Plane] DatumPlane002  label="PlaneBaseTop"
  AttachmentOffset = pos=(0,0,2) rot=(0,0,1;0rad)
  AttachmentSupport = -> [XY_Plane001]
  Length = 60
  MapMode = 2
  Placement = pos=(0,0,2) rot=(0,0,1;0rad)
  ResizeMode = 0
  Width = 60
FEATURE [Sketcher::SketchObject] Sketch004  label="SketchAttachmentHoles"
  ArcFitTolerance = 0
  AttachmentSupport = -> [DatumPlane002]
  FullyConstrained = true
  MakeInternals = false
  MapMode = 5
  Placement = pos=(0,0,2) rot=(0,0,1;0rad)
  sketch-geometry (2):
    g0: Circle CenterX=-6e-16 CenterY=-10 CenterZ=0 NormalX=0 NormalY=0 NormalZ=1 AngleXU=0 Radius=1.5
    g1: Circle CenterX=0 CenterY=10 CenterZ=0 NormalX=0 NormalY=0 NormalZ=1 AngleXU=0 Radius=1.5
  constraints (5):
    c: Symmetric(g0,g1,g-1)
    c: Equal(g1,g0)
    c: Diameter(g1) = 3
    c: Distance(g-1,g1) = 10
    c: PointOnObject(g1,g-2)
FEATURE [PartDesign::Hole] Hole
  BaseFeature = -> Mirrored
  CustomThreadClearance = 0
  Depth = 25
  DepthType = 0
  Diameter = 3.4
  DrillForDepth = false
  DrillPoint = 1
  DrillPointAngle = 118
  HoleCutCountersinkAngle = 90
  HoleCutCustomValues = false
  HoleCutDepth = 0
  HoleCutDiameter = 6
  HoleCutType = 0
  ModelThread = false
  Placement = pos=(0,0,0) rot=(1,1,1;2.0944rad)
  Profile = -> Sketch004
  Suppressed = false
  Tapered = false
  TaperedAngle = 90
  ThreadClass = 0
  ThreadDepth = 25
  ThreadDepthType = 0
  ThreadDirection = 0
  ThreadFit = 0
  ThreadSize = 9
  ThreadType = 1
  Threaded = false
  UseCustomThreadClearance = false
FEATURE [PartDesign::Hole] Hole001
  BaseFeature = -> Hole
  CustomThreadClearance = 0
  Depth = 25
  DepthType = 0
  Diameter = 4.5
  DrillForDepth = false
  DrillPoint = 1
  DrillPointAngle = 118
  HoleCutCountersinkAngle = 90
  HoleCutCustomValues = false
  HoleCutDepth = 0
  HoleCutDiameter = 6.1
  HoleCutType = 0
  ModelThread = false
  Placement = pos=(0,0,0) rot=(1,1,1;2.0944rad)
  Profile = -> Sketch002
  Suppressed = false
  Tapered = false
  TaperedAngle = 90
  ThreadClass = 0
  ThreadDepth = 25
  ThreadDepthType = 0
  ThreadDirection = 0
  ThreadFit = 0
  ThreadSize = 11
  ThreadType = 1
  Threaded = false
  UseCustomThreadClearance = false
FEATURE [Sketcher::SketchObject] Sketch005
  ArcFitTolerance = 0
  AttachmentSupport = -> [XY_Plane002]
  FullyConstrained = true
  MakeInternals = false
  MapMode = 5
  sketch-geometry (4):
    g0: LineSegment StartX=-8.25 StartY=15 StartZ=0 EndX=8.25 EndY=15 EndZ=0
    g1: LineSegment StartX=8.25 StartY=15 StartZ=0 EndX=8.25 EndY=-15 EndZ=0
    g2: LineSegment StartX=8.25 StartY=-15 StartZ=0 EndX=-8.25 EndY=-15 EndZ=0
    g3: LineSegment StartX=-8.25 StartY=-15 StartZ=0 EndX=-8.25 EndY=15 EndZ=0
  constraints (11):
    c: Coincident(g0,g1)
    c: Coincident(g1,g2)
    c: Coincident(g2,g3)
    c: Coincident(g3,g0)
    c: Horizontal(g0)
    c: Horizontal(g2)
    c: Vertical(g1)
    c: Vertical(g3)
    c: Symmetric(g1,g0,g-1)
    c: Distance(g2) = 16.5
    c: Distance(g3) = 30
FEATURE [Sketcher::SketchObject] Sketch006
  ArcFitTolerance = 0
  AttachmentSupport = -> [XY_Plane002]
  FullyConstrained = true
  MakeInternals = false
  MapMode = 5
  sketch-geometry (2):
    g0: Circle CenterX=0 CenterY=10 CenterZ=0 NormalX=0 NormalY=0 NormalZ=1 AngleXU=0 Radius=1.5
    g1: Circle CenterX=0 CenterY=-10 CenterZ=0 NormalX=0 NormalY=0 NormalZ=1 AngleXU=0 Radius=1.5
  constraints (5):
    c: Symmetric(g0,g1,g-1)
    c: Equal(g1,g0)
    c: Diameter(g1) = 3
    c: Distance(g0,g1) = 20
    c: PointOnObject(g0,g-2)
FEATURE [PartDesign::CoordinateSystem] Local_CS004  label="LCS_Bottom"
  AttacherType = Attacher::AttachEngine3D
  AttachmentSupport = -> [X_Axis002]
  MapMode = 2
FEATURE [PartDesign::Plane] DatumPlane003  label="Plane_Top"
  AttachmentOffset = pos=(0,0,1) rot=(0,0,1;0rad)
  AttachmentSupport = -> [XY_Plane002]
  Length = 60
  MapMode = 5
  Placement = pos=(0,0,1) rot=(0,0,1;0rad)
  ResizeMode = 0
  Width = 60
FEATURE [PartDesign::Pad] Pad002
  Direction = (0,0,1)
  Length = 10
  Length2 = 10
  Profile = -> Sketch005
  ReferenceAxis = -> Sketch005 [N_Axis]
  Suppressed = false
  Type = 3
  UpToFace = -> DatumPlane003 [Plane]
FEATURE [PartDesign::Hole] Hole002
  BaseFeature = -> Pad002
  CustomThreadClearance = 0
  Depth = 25
  DepthType = 0
  Diameter = 3.4
  DrillForDepth = false
  DrillPoint = 1
  DrillPointAngle = 118
  HoleCutCountersinkAngle = 90
  HoleCutCustomValues = false
  HoleCutDepth = 0
  HoleCutDiameter = 6.1
  HoleCutType = 0
  ModelThread = false
  Profile = -> Sketch006
  Reversed = true
  Suppressed = false
  Tapered = false
  TaperedAngle = 90
  ThreadClass = 0
  ThreadDepth = 25
  ThreadDepthType = 0
  ThreadDirection = 0
  ThreadFit = 0
  ThreadSize = 9
  ThreadType = 1
  Threaded = false
  UseCustomThreadClearance = false
FEATURE [PartDesign::Body] Body001  label="OffsetBlockIndexShade"
  AllowCompound = false
  Group = -> [Sketch005,Sketch006,Pad002,Hole002,Local_CS004,DatumPlane003]
  Origin = -> Origin002
  Tip = -> Hole002
FEATURE [Sketcher::SketchObject] Sketch007
  ArcFitTolerance = 0
  AttachmentSupport = -> [XY_Plane003]
  FullyConstrained = true
  MakeInternals = false
  MapMode = 5
  sketch-geometry (2):
    g0: Circle CenterX=0 CenterY=10 CenterZ=0 NormalX=0 NormalY=0 NormalZ=1 AngleXU=0 Radius=1.5
    g1: Circle CenterX=0 CenterY=-10 CenterZ=0 NormalX=0 NormalY=0 NormalZ=1 AngleXU=0 Radius=1.5
  constraints (5):
    c: Equal(g0,g1)
    c: Diameter(g0) = 3
    c: Symmetric(g1,g0,g-1)
    c: Distance(g0,g1) = 20
    c: PointOnObject(g0,g-2)
FEATURE [Sketcher::SketchObject] Sketch008
  ArcFitTolerance = 0
  AttachmentSupport = -> [XY_Plane003]
  FullyConstrained = true
  MakeInternals = false
  MapMode = 5
  sketch-geometry (4):
    g0: LineSegment StartX=-8.25 StartY=15 StartZ=0 EndX=8.25 EndY=15 EndZ=0
    g1: LineSegment StartX=8.25 StartY=15 StartZ=0 EndX=8.25 EndY=-15 EndZ=0
    g2: LineSegment StartX=8.25 StartY=-15 StartZ=0 EndX=-8.25 EndY=-15 EndZ=0
    g3: LineSegment StartX=-8.25 StartY=-15 StartZ=0 EndX=-8.25 EndY=15 EndZ=0
  constraints (11):
    c: Coincident(g0,g1)
    c: Coincident(g1,g2)
    c: Coincident(g2,g3)
    c: Coincident(g3,g0)
    c: Horizontal(g0)
    c: Horizontal(g2)
    c: Vertical(g1)
    c: Vertical(g3)
    c: Symmetric(g1,g0,g-1)
    c: Distance(g3) = 30
    c: Distance(g0) = 16.5
FEATURE [PartDesign::Plane] DatumPlane004  label="Plane_Top001"
  AttachmentOffset = pos=(0,0,10) rot=(0,0,1;0rad)
  AttachmentSupport = -> [XY_Plane003]
  Length = 60
  MapMode = 5
  Placement = pos=(0,0,10) rot=(0,0,1;0rad)
  ResizeMode = 0
  Width = 60
FEATURE [PartDesign::Pad] Pad003
  Direction = (0,0,1)
  Length = 10
  Length2 = 10
  Profile = -> Sketch008
  ReferenceAxis = -> Sketch008 [N_Axis]
  Suppressed = false
  Type = 3
  UpToFace = -> DatumPlane004 [Plane]
FEATURE [PartDesign::Hole] Hole003
  BaseFeature = -> Pad003
  CustomThreadClearance = 0
  Depth = 25
  DepthType = 0
  Diameter = 3.4
  DrillForDepth = false
  DrillPoint = 1
  DrillPointAngle = 118
  HoleCutCountersinkAngle = 90
  HoleCutCustomValues = false
  HoleCutDepth = 0
  HoleCutDiameter = 6.1
  HoleCutType = 0
  ModelThread = false
  Profile = -> Sketch007
  Reversed = true
  Suppressed = false
  Tapered = false
  TaperedAngle = 90
  ThreadClass = 0
  ThreadDepth = 25
  ThreadDepthType = 0
  ThreadDirection = 0
  ThreadFit = 0
  ThreadSize = 9
  ThreadType = 1
  Threaded = false
  UseCustomThreadClearance = false
FEATURE [PartDesign::CoordinateSystem] Local_CS005  label="LCS_Bottom001"
  AttacherType = Attacher::AttachEngine3D
  AttachmentSupport = -> [X_Axis003]
  MapMode = 2
FEATURE [PartDesign::Body] OffsetBlockHorizonShade
  AllowCompound = false
  Group = -> [Sketch007,Sketch008,Pad003,Hole003,Local_CS005,DatumPlane004]
  Origin = -> Origin003
  Tip = -> Hole003
FEATURE [PartDesign::Hole] Hole004
  BaseFeature = -> Hole001
  CustomThreadClearance = 0
  Depth = 25
  DepthType = 0
  Diameter = 6
  DrillForDepth = false
  DrillPoint = 1
  DrillPointAngle = 118
  HoleCutCountersinkAngle = 90
  HoleCutCustomValues = false
  HoleCutDepth = 0
  HoleCutDiameter = 6.1
  HoleCutType = 0
  ModelThread = false
  Placement = pos=(0,0,0) rot=(1,1,1;2.0944rad)
  Profile = -> Sketch004
  Reversed = true
  Suppressed = false
  Tapered = false
  TaperedAngle = 90
  ThreadClass = 0
  ThreadDepth = 25
  ThreadDepthType = 0
  ThreadDirection = 0
  ThreadFit = 0
  ThreadSize = 0
  ThreadType = 0
  Threaded = false
  UseCustomThreadClearance = false
FEATURE [PartDesign::Body] Body  label="Attachment"
  AllowCompound = false
  Group = -> [DatumPlane,DatumPlane001,DatumPlane002,Sketch001,Sketch002,Pad001,Sketch003,Pocket,Mirrored,Hole,Sketch004,Local_CS,Local_CS001,Local_CS002,Local_CS003,Hole001,Hole004]
  Origin = -> Origin001
  Tip = -> Hole004
FEATURE [App::DocumentObjectGroup] Parts
  Group = -> [Body,Body001,OffsetBlockHorizonShade]
FEATURE [Part::FeaturePython] Linear_Filter  label="Linear_Shade"  # Draft array (typed FeaturePython)
  ArrayType = Linear Array
  Axis = -> X_Axis
  AxisPlacement = pos=(0,0,0) rot=(0.57735,0.57735,0.57735;2.0944rad)
  Count = 2
  Index = 1
  LinearStep = -6
  PlacementList = 2 placements: [(-2.75,-2.22045e-15,7),(-8.75,-1.55431e-15,7)]
  Placer = pos=(0,0,-6) rot=(0,0,1;0rad)
  ScaleList = (2) [(1,1,1),(1,1,1)]
  Scaler = 1
  ShowElement = false
  SourceObject = -> Filter
  expr: .Placer.Base.z = LinearStep * Index
  expr: Count = <<Dimensions>>.shade_amount
  expr: LinearStep = -<<Dimensions>>.shade_spacer_length
FEATURE [App::Part] Assembly
  AssemblyType = Part::Link
  Group = -> [LCS_Origin,Constraints,Variables,Configurations,Attachment,Spacer,Screw,Nut,Filter,Linear_Filter]
  Origin = -> Origin
  Type = Assembly
---- part Viewscope.FCStd = doc fcstd_d52af45adea2 ----
FCSTD DOCUMENT  (FreeCAD 1.0RUnknown)
Label: Viewscope
License: All rights reserved
LicenseURL: http://en.wikipedia.org/wiki/All_rights_reserved
objects: PartDesign::CoordinateSystem×7, Sketcher::SketchObject×4, App::Link×4, App::Part×4, App::DocumentObjectGroup×3, PartDesign::Body×3, PartDesign::Hole×3, PartDesign::Pad×2, PartDesign::SubShapeBinder×2, Part::FeaturePython×2, App::FeaturePython×1, PartDesign::Revolution×1
note: 40 computed .brp shape members not serialized (recipe doc carries the construction recipe); baked Part::Feature solids carry a one-line shape summary decoded from their .brp
EXTERNAL_REF file=Resources.FCStd obj=Spreadsheet
EXTERNAL_REF file=Sextant.FCStd obj=Assembly

FEATURE [Sketcher::SketchObject] Sketch002
  ArcFitTolerance = 0
  AttachmentSupport = -> [XZ_Plane007]
  FullyConstrained = true
  MakeInternals = false
  MapMode = 5
  Placement = pos=(0,0,0) rot=(1,0,0;1.5708rad)
  expr: Constraints[30] = <<Dimensions>>.viewscope_wall_thickness
  expr: Constraints[35] = <<Dimensions>>.viewscope_inner_diameter / 2
  expr: Constraints[8] = <<Dimensions>>.viewscope_eye_diameter / 2
  sketch-geometry (12):
    g0: LineSegment StartX=-66.0863 StartY=11 StartZ=0 EndX=-17.5885 EndY=11 EndZ=0
    g1: LineSegment StartX=-17.5885 StartY=11 StartZ=0 EndX=0 EndY=21.1547 EndZ=0
    g2: LineSegment StartX=-66.2626 StartY=10 StartZ=0 EndX=-17.3205 EndY=10 EndZ=0
    g3: LineSegment StartX=-17.3205 StartY=10 StartZ=0 EndX=0 EndY=20 EndZ=0
    g4: LineSegment StartX=0 StartY=21.1547 StartZ=0 EndX=0 EndY=20 EndZ=0
    g5: LineSegment [constr] StartX=0 StartY=20 StartZ=0 EndX=-0.5 EndY=20.866 EndZ=0
    g6: LineSegment StartX=-66.0863 StartY=11 StartZ=0 EndX=-80 EndY=16.0642 EndZ=0
    g7: LineSegment StartX=-66.2626 StartY=10 StartZ=0 EndX=-80 EndY=15 EndZ=0
    g8: LineSegment StartX=-80 StartY=16.0642 StartZ=0 EndX=-80 EndY=15 EndZ=0
    g9: LineSegment [constr] StartX=-80 StartY=15 StartZ=0 EndX=-80 EndY=0 EndZ=0
    g10: LineSegment [constr] StartX=-66.0863 StartY=11 StartZ=0 EndX=-66.0863 EndY=10 EndZ=0
    g11: LineSegment [constr] StartX=-80 StartY=15 StartZ=0 EndX=-79.658 EndY=15.9397 EndZ=0
  constraints (36):
    c: Horizontal(g0)
    c: Coincident(g1,g0)
    c: Horizontal(g2)
    c: Coincident(g3,g2)
    c: Coincident(g4,g1)
    c: Coincident(g4,g3)
    c: Vertical(g4)
    c: PointOnObject(g3,g-2)
    c: Distance(g-1,g3) = 20
    c: Angle(g3,g-2) = 1.0472
    c: Coincident(g5,g3)
    c: PointOnObject(g5,g1)
    c: Perpendicular(g1,g5)
    c: Parallel(g1,g3)
    c: Coincident(g6,g0)
    c: Coincident(g8,g6)
    c: Coincident(g8,g7)
    c: DistanceX(g6,g1) = 80
    c: Coincident(g7,g2)
    c: Vertical(g8)
    c: Coincident(g9,g8)
    c: Vertical(g9)
    c: Angle(g9,g7) = 1.22173
    c: Parallel(g6,g7)
    c: Coincident(g10,g0)
    c: Coincident(g11,g7)
    c: PointOnObject(g11,g6)
    c: Perpendicular(g6,g11)
    c: PointOnObject(g10,g2)
    c: Perpendicular(g2,g10)
    c: Distance(g10) = 1
    c: Equal(g10,g11)
    c: Equal(g10,g5)
    c: DistanceY(g9,g9) = 15
    c: PointOnObject(g9,g-1)
    c: DistanceY(g2) = 10
FEATURE [PartDesign::CoordinateSystem] LCS_Origin
  AttacherType = Attacher::AttachEngine3D
  AttachmentSupport = -> [X_Axis]
  MapMode = 2
FEATURE [App::DocumentObjectGroup] Constraints
FEATURE [App::FeaturePython] Variables  # WARN: FeaturePython — macro-defined, semantics opaque (R4)
  Type = App::PropertyContainer
FEATURE [App::DocumentObjectGroup] Configurations
FEATURE [PartDesign::CoordinateSystem] LCS_Origin001
  AttacherType = Attacher::AttachEngine3D
  AttachmentSupport = -> [X_Axis008]
  MapMode = 2
FEATURE [Sketcher::SketchObject] Sketch
  ArcFitTolerance = 0
  AttachmentSupport = -> [YZ_Plane009]
  FullyConstrained = true
  MakeInternals = false
  MapMode = 5
  Placement = pos=(0,0,0) rot=(0.57735,0.57735,0.57735;2.0944rad)
  expr: Constraints[15] = <<Dimensions>>.view_center_offset_hor - <<Dimensions>>.viewscope_collar_gap / 2
  expr: Constraints[16] = <<Dimensions>>.viewscope_collar_width
  expr: Constraints[8] = <<Dimensions>>.viewscope_inner_diameter / 2 + <<Dimensions>>.viewscope_wall_thickness + <<Dimensions>>.clearance_tight_fit
  sketch-geometry (6):
    g0: LineSegment StartX=-18.15 StartY=28.85 StartZ=0 EndX=-18.15 EndY=0 EndZ=0
    g1: LineSegment StartX=-18.15 StartY=28.85 StartZ=0 EndX=-11.15 EndY=28.85 EndZ=0
    g2: LineSegment StartX=18.15 StartY=0 StartZ=0 EndX=18.15 EndY=28.85 EndZ=0
    g3: LineSegment StartX=18.15 StartY=28.85 StartZ=0 EndX=11.15 EndY=28.85 EndZ=0
    g4: ArcOfCircle CenterX=0 CenterY=28.85 CenterZ=0 NormalX=0 NormalY=0 NormalZ=1 AngleXU=0 Radius=11.15 StartAngle=3.14159 EndAngle=6.28319
    g5: LineSegment StartX=-18.15 StartY=0 StartZ=0 EndX=18.15 EndY=0 EndZ=0
  constraints (19):
    c: PointOnObject(g0,g-1)
    c: Vertical(g0)
    c: Coincident(g1,g0)
    c: PointOnObject(g2,g-1)
    c: Vertical(g2)
    c: Coincident(g3,g2)
    c: PointOnObject(g4,g-2)
    c: Coincident(g4,g1)
    c: Radius(g4) = 11.15
    c: Perpendicular(g4,g1)
    c: Coincident(g4,g3)
    c: Perpendicular(g4,g3)
    c: Horizontal(g1)
    c: Horizontal(g3)
    c: Equal(g1,g3)
    c: DistanceY(g-1,g4) = 28.85
    c: DistanceX(g3,g3) = 7
    c: Coincident(g5,g0)
    c: Coincident(g2,g5)
FEATURE [PartDesign::Pad] Pad
  Direction = (1,0,0)
  Length = 7.5
  Length2 = 10
  Midplane = true
  Placement = pos=(0,0,0) rot=(1,1,1;2.0944rad)
  Profile = -> Sketch
  ReferenceAxis = -> Sketch [N_Axis]
  Suppressed = false
  Type = 0
  expr: Length = <<Dimensions>>.viewscope_collar_thickness
FEATURE [Sketcher::SketchObject] Sketch003
  ArcFitTolerance = 0
  AttachmentSupport = -> [YZ_Plane011]
  FullyConstrained = true
  MakeInternals = false
  MapMode = 5
  Placement = pos=(0,0,0) rot=(0.57735,0.57735,0.57735;2.0944rad)
  expr: Constraints[3] = <<Dimensions>>.viewscope_inner_diameter / 2 + <<Dimensions>>.viewscope_wall_thickness + <<Dimensions>>.clearance_tight_fit
  expr: Constraints[4] = <<Dimensions>>.viewscope_collar_width
  expr: Constraints[8] = <<Dimensions>>.viewscope_collar_gap / 2
  sketch-geometry (7):
    g0: ArcOfCircle CenterX=0 CenterY=0 CenterZ=0 NormalX=0 NormalY=0 NormalZ=1 AngleXU=0 Radius=11.15 StartAngle=0.103323 EndAngle=3.03827
    g1: LineSegment StartX=-18.0905 StartY=1.15 StartZ=0 EndX=-11.0905 EndY=1.15 EndZ=0
    g2: LineSegment StartX=11.0905 StartY=1.15 StartZ=0 EndX=18.0905 EndY=1.15 EndZ=0
    g3: ArcOfCircle CenterX=0 CenterY=0 CenterZ=0 NormalX=0 NormalY=0 NormalZ=1 AngleXU=0 Radius=18.1271 StartAngle=0.0634837 EndAngle=1.0472
    g4: LineSegment StartX=-9.06353 StartY=15.6985 StartZ=0 EndX=9.06353 EndY=15.6985 EndZ=0
    g5: ArcOfCircle CenterX=0 CenterY=0 CenterZ=0 NormalX=0 NormalY=0 NormalZ=1 AngleXU=0 Radius=18.1271 StartAngle=2.0944 EndAngle=3.07811
    g6: LineSegment [constr] StartX=-9.06353 StartY=15.6985 StartZ=0 EndX=0 EndY=20.9313 EndZ=0
  constraints (20):
    c: Coincident(g0,g-1)
    c: Horizontal(g1)
    c: Coincident(g2,g0)
    c: Radius(g0) = 11.15
    c: Distance(g1) = 7
    c: Coincident(g3,g0)
    c: Coincident(g5,g1)
    c: Coincident(g3,g2)
    c: DistanceY(g0,g1) = 1.15
    c: Tangent(g2,g1)
    c: Coincident(g1,g0)
    c: Horizontal(g4)
    c: Equal(g3,g5)
    c: Coincident(g3,g4)
    c: Coincident(g5,g4)
    c: Coincident(g3,g5)
    c: Coincident(g6,g4)
    c: PointOnObject(g6,g-2)
    c: Tangent(g5,g6)
    c: Angle(g4,g6) = 0.523599
FEATURE [PartDesign::Pad] Pad001
  Direction = (1,0,0)
  Length = 7.5
  Length2 = 10
  Midplane = true
  Placement = pos=(0,0,0) rot=(1,1,1;2.0944rad)
  Profile = -> Sketch003
  ReferenceAxis = -> Sketch003 [N_Axis]
  Suppressed = false
  Type = 0
  expr: Length = <<Dimensions>>.viewscope_collar_thickness
FEATURE [PartDesign::Revolution] Revolution
  Angle = 360
  Angle2 = 60
  Axis = (1,0,0)
  Base = (0,0,0)
  Placement = pos=(0,0,0) rot=(1,0,0;1.5708rad)
  Profile = -> Sketch002
  ReferenceAxis = -> Sketch002 [H_Axis]
  Suppressed = false
  Type = 0
FEATURE [PartDesign::Body] Body002
  AllowCompound = false
  Group = -> [Sketch002,Revolution]
  Origin = -> Origin007
  Tip = -> Revolution
FEATURE [App::Link] ClampBottom  label="ClampBottom001"
  AttachedBy = #LCS_Origin001
  AttachedTo = Parent Assembly#LCS_Origin
  LinkedObject = -> HolderBottom
  SolverId = Asm4EE
  expr: Placement = LCS_Origin.Placement * AttachmentOffset * LCS_Origin001.Placement ^ -1
FEATURE [PartDesign::CoordinateSystem] LCS_Center
  AttacherType = Attacher::AttachEngine3D
  AttachmentSupport = -> [Sketch]
  MapMode = 12
  Placement = pos=(0,0,28.85) rot=(0,0,-1;1.5708rad)
FEATURE [PartDesign::CoordinateSystem] LCS_Clamp1  label="LCS_Collar"
  AttacherType = Attacher::AttachEngine3D
  AttachmentSupport = -> [Revolution]
  MapMode = 45
  Placement = pos=(-41.8374,-1e-16,1.8e-15) rot=(0.57735,0.57735,0.57735;2.0944rad)
FEATURE [App::Part] Part001  label="Viewscope"
  Group = -> [Body002,LCS_Clamp1]
  Origin = -> Origin006
FEATURE [App::Link] Viewscope  label="Viewscope001"
  AttachedBy = #LCS_Clamp1
  AttachedTo = ClampBottom#LCS_Center
  AttachmentOffset = pos=(0,0,0) rot=(0,-0.707107,-0.707107;3.14159rad)
  LinkPlacement = pos=(41.8374,1.52e-14,28.85) rot=(0,0,1;0rad)
  LinkedObject = -> Part001
  Placement = pos=(41.8374,1.52e-14,28.85) rot=(0,0,1;0rad)
  SolverId = Asm4EE
  expr: Placement = ClampBottom.Placement * LCS_Center.Placement * AttachmentOffset * LCS_Clamp1.Placement ^ -1
FEATURE [Sketcher::SketchObject] Sketch004
  ArcFitTolerance = 0
  AttachmentSupport = -> [XY_Plane011]
  FullyConstrained = true
  MakeInternals = false
  MapMode = 5
  expr: .Constraints.hole_distance = <<Dimensions>>.viewscope_inner_diameter + 2 * <<Dimensions>>.viewscope_wall_thickness + <<Dimensions>>.viewscope_collar_width
  expr: Constraints[1] = <<Dimensions>>.viewscope_screw_diameter
  sketch-geometry (2):
    g0: Circle CenterX=0 CenterY=14.5 CenterZ=0 NormalX=0 NormalY=0 NormalZ=1 AngleXU=0 Radius=1.5
    g1: Circle CenterX=0 CenterY=-14.5 CenterZ=0 NormalX=0 NormalY=0 NormalZ=1 AngleXU=0 Radius=1.5
  constraints (5):
    c: Equal(g0,g1)
    c: Diameter(g0) = 3
    c: PointOnObject(g1,g-2)
    c: Distance(g0,g1) = 29  'hole_distance'
    c: Symmetric(g1,g0,g-1)
FEATURE [PartDesign::SubShapeBinder] Binder
  BindCopyOnChange = 0
  BindMode = 0
  ClaimChildren = false
  Context = -> HolderBottom [Body.Binder.]
  Fuse = false
  MakeFace = true
  OffsetFill = false
  OffsetIntersection = false
  OffsetJoinType = 0
  OffsetOpenResult = false
  PartialLoad = false
  Relative = true
  Support = -> [Part[Body_2.Hole.Sketch004.]]
  _Version = 2
FEATURE [PartDesign::Hole] Hole001
  BaseFeature = -> Pad
  CustomThreadClearance = 0
  Depth = 94.9755
  DepthType = 1
  Diameter = 3.4
  DrillForDepth = false
  DrillPoint = 1
  DrillPointAngle = 118
  HoleCutCountersinkAngle = 90
  HoleCutCustomValues = false
  HoleCutDepth = 4
  HoleCutDiameter = 3.9
  HoleCutType = 3
  ModelThread = false
  Placement = pos=(0,0,0) rot=(1,1,1;2.0944rad)
  Profile = -> Binder
  Reversed = true
  Suppressed = false
  Tapered = false
  TaperedAngle = 90
  ThreadClass = 0
  ThreadDepth = 94.8812
  ThreadDepthType = 0
  ThreadDirection = 0
  ThreadFit = 0
  ThreadSize = 9
  ThreadType = 1
  Threaded = false
  UseCustomThreadClearance = false
  expr: HoleCutDepth = <<Dimensions>>.viewscope_ti_L
  expr: HoleCutDiameter = <<Dimensions>>.viewscope_ti_D
  expr: ThreadSize = <<Dimensions>>.viewscope_screw_type
FEATURE [App::Link] CollarTop  label="CollarTop001"
  AttachedBy = #LCS_Origin002
  AttachedTo = ClampBottom#LCS_Center
  AttachmentOffset = pos=(0,0,0) rot=(0,0,1;1.5708rad)
  LinkPlacement = pos=(0,0,28.85) rot=(0,0,1;0rad)
  LinkedObject = -> Part
  Placement = pos=(0,0,28.85) rot=(0,0,1;0rad)
  SolverId = Asm4EE
  expr: Placement = ClampBottom.Placement * LCS_Center.Placement * AttachmentOffset * LCS_Origin002.Placement ^ -1
FEATURE [PartDesign::CoordinateSystem] LCS_Origin002
  AttacherType = Attacher::AttachEngine3D
  AttachmentSupport = -> [X_Axis011]
  MapMode = 2
FEATURE [App::Link] Link  label="Dimensions"
  LinkedObject = -> <external Resources.FCStd>#Spreadsheet
FEATURE [PartDesign::SubShapeBinder] Binder001
  BindCopyOnChange = 0
  BindMode = 0
  ClaimChildren = false
  Context = -> <external Sextant.FCStd>#Assembly [Viewscope.CollarTop.Body_2.Binder001.]
  Fuse = false
  MakeFace = true
  OffsetFill = false
  OffsetIntersection = false
  OffsetJoinType = 0
  OffsetOpenResult = false
  PartialLoad = false
  Placement = pos=(0,0,18) rot=(0,0,1;0rad)
  Relative = true
  Support = -> [Sketch004]
  _Version = 2
  expr: .Placement.Base.z = <<Dimensions>>.viewscope_collar_outer_diameter / 2
FEATURE [PartDesign::Hole] Hole
  BaseFeature = -> Pad001
  CustomThreadClearance = 0
  Depth = 82.1542
  DepthType = 1
  Diameter = 3.4
  DrillForDepth = false
  DrillPoint = 1
  DrillPointAngle = 90
  HoleCutCountersinkAngle = 90
  HoleCutCustomValues = false
  HoleCutDepth = 12.85
  HoleCutDiameter = 6
  HoleCutType = 3
  ModelThread = false
  Placement = pos=(0,0,0) rot=(1,1,1;2.0944rad)
  Profile = -> Binder001
  Suppressed = false
  Tapered = false
  TaperedAngle = 90
  ThreadClass = 0
  ThreadDepth = 82.034
  ThreadDepthType = 0
  ThreadDirection = 0
  ThreadFit = 0
  ThreadSize = 9
  ThreadType = 1
  Threaded = false
  UseCustomThreadClearance = false
  expr: HoleCutDepth = <<Dimensions>>.viewscope_collar_outer_diameter / 2 - <<Dimensions>>.viewscope_collar_gap / 2 - <<Dimensions>>.viewscope_screwhead_support_thickness
  expr: HoleCutDiameter = <<Dimensions>>.viewscope_screw_head_diameter + 2 * <<Dimensions>>.clearance_loose_fit
  expr: ThreadSize = <<Dimensions>>.viewscope_screw_type
FEATURE [PartDesign::Body] Body_2  label="CollarBottomBody"
  AllowCompound = false
  Group = -> [Sketch003,Pad001,Sketch004,Binder001,Hole]
  Origin = -> Origin011
  Tip = -> Hole
FEATURE [PartDesign::CoordinateSystem] LCS_test  label="LCS_Bolt1"
  AttacherType = Attacher::AttachEngine3D
  AttachmentOffset = pos=(0,0,5.15) rot=(0,0,1;0rad)
  AttachmentSupport = -> [Sketch004]
  MapMode = 11
  Placement = pos=(0,-14.5,5.15) rot=(0,0,1;1.5708rad)
  expr: .AttachmentOffset.Base.z = <<Dimensions>>.viewscope_collar_gap / 2 + <<Dimensions>>.viewscope_screwhead_support_thickness
FEATURE [PartDesign::CoordinateSystem] LCS_Bolt2
  AttacherType = Attacher::AttachEngine3D
  AttachmentOffset = pos=(0,0,5.15) rot=(0,0,1;0rad)
  AttachmentSupport = -> [Sketch004]
  MapMode = 11
  Placement = pos=(0,14.5,5.15) rot=(0,0,1;1.5708rad)
  expr: .AttachmentOffset.Base.z = <<Dimensions>>.viewscope_collar_gap / 2 + <<Dimensions>>.viewscope_screwhead_support_thickness
FEATURE [App::Part] Part  label="CollarTop"
  Group = -> [Body_2,LCS_Origin002,LCS_test,LCS_Bolt2]
  Origin = -> Origin010
FEATURE [PartDesign::Hole] Hole002
  BaseFeature = -> Hole001
  CustomThreadClearance = 0
  Depth = 94.9755
  DepthType = 1
  Diameter = 3.4
  DrillForDepth = false
  DrillPoint = 1
  DrillPointAngle = 118
  HoleCutCountersinkAngle = 90
  HoleCutCustomValues = false
  HoleCutDepth = 4
  HoleCutDiameter = 3.9
  HoleCutType = 3
  ModelThread = false
  Placement = pos=(0,0,0) rot=(1,1,1;2.0944rad)
  Profile = -> Hole001 [Edge8,Edge28]
  Suppressed = false
  Tapered = false
  TaperedAngle = 90
  ThreadClass = 0
  ThreadDepth = 94.8812
  ThreadDepthType = 0
  ThreadDirection = 0
  ThreadFit = 0
  ThreadSize = 9
  ThreadType = 1
  Threaded = false
  UseCustomThreadClearance = false
  expr: HoleCutDepth = <<Dimensions>>.viewscope_ti_L
  expr: HoleCutDiameter = <<Dimensions>>.viewscope_ti_D
  expr: ThreadSize = <<Dimensions>>.viewscope_screw_type
FEATURE [PartDesign::Body] Body
  AllowCompound = false
  Group = -> [Sketch,Pad,Binder,Hole001,Hole002]
  Origin = -> Origin009
  Tip = -> Hole002
FEATURE [App::Part] HolderBottom  label="CollarBottom"
  Group = -> [LCS_Origin001,Body,LCS_Center]
  Origin = -> Origin008
FEATURE [App::DocumentObjectGroup] Parts
  Group = -> [Part001,HolderBottom,Part]
FEATURE [Part::FeaturePython] Screw  label="M3x10-Screw001"  # WARN: FeaturePython — macro-defined, semantics opaque (R4)
  AttachedBy = Origin
  AttachedTo = CollarTop#LCS_test
  Diameter = 3
  Invert = false
  LeftHanded = false
  Length = 1
  LengthCustom = 10
  MatchOuter = false
  OffsetAngle = 0
  Placement = pos=(0,-14.5,34) rot=(0,0,1;1.5708rad)
  SolverId = Asm4EE
  Thread = false
  Type = 50
  expr: Diameter = <<Dimensions>>.viewscope_screw_type
  expr: Placement = CollarTop.Placement * LCS_test.Placement * AttachmentOffset
FEATURE [Part::FeaturePython] Screw001  label="M3x10-Screw"  # WARN: FeaturePython — macro-defined, semantics opaque (R4)
  AttachedBy = Origin
  AttachedTo = CollarTop#LCS_Bolt2
  Diameter = 3
  Invert = false
  LeftHanded = false
  Length = 1
  LengthCustom = 10
  MatchOuter = false
  OffsetAngle = 0
  Placement = pos=(0,14.5,34) rot=(0,0,1;1.5708rad)
  SolverId = Asm4EE
  Thread = false
  Type = 50
  expr: Diameter = <<Dimensions>>.viewscope_screw_type
  expr: Placement = CollarTop.Placement * LCS_Bolt2.Placement * AttachmentOffset
FEATURE [App::Part] Assembly
  AssemblyType = Part::Link
  Group = -> [LCS_Origin,Constraints,Variables,Configurations,ClampBottom,Viewscope,CollarTop,Screw,Screw001]
  Origin = -> Origin
  Type = Assembly
